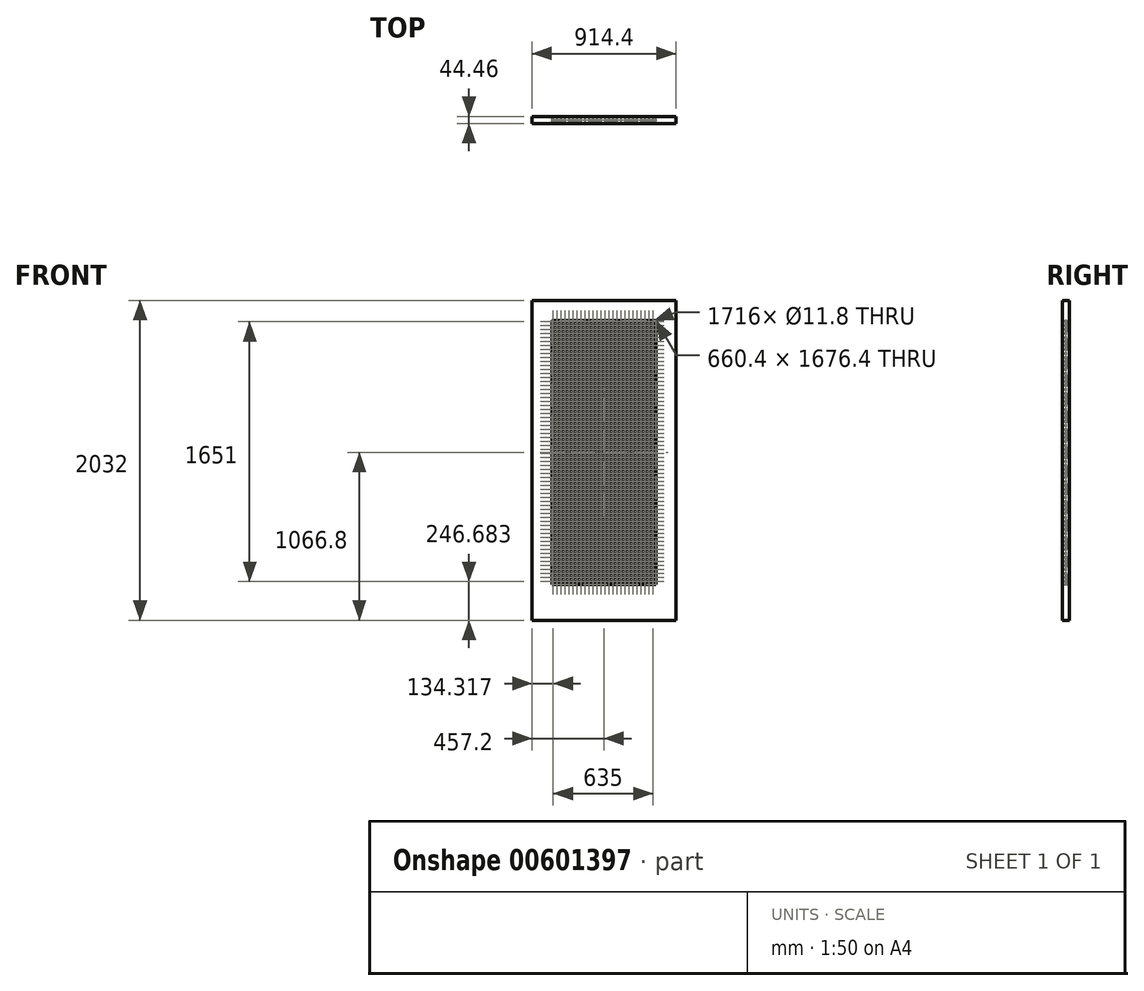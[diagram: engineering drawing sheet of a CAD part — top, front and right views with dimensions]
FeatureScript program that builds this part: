
annotation { "Feature Type Name" : "Feature", "Feature Type Description" : "" }
export const myFeature = defineFeature(function(context is Context, id is Id, definition is map)
    precondition{}
    {
        {
            var Q0;
            Q0=qCreatedBy(makeId("Front.planeOp"),FACE);
            var sketch = newSketch(context, id + "F0", { "sketchPlane" : qUnion([Q0])});
            skLineSegment(sketch, "E0.bottom", {"start": v(-457.2, 965.2) * mm, "end": v(457.2, 965.2) * mm});
            skLineSegment(sketch, "E0.top", {"start": v(-457.2, -1066.8) * mm, "end": v(457.2, -1066.8) * mm});
            skLineSegment(sketch, "E0.left", {"start": v(-457.2, 965.2) * mm, "end": v(-457.2, -1066.8) * mm});
            skLineSegment(sketch, "E0.right", {"start": v(457.2, 965.2) * mm, "end": v(457.2, -1066.8) * mm});
            skPoint(sketch, "E0.middle", {"position": v(0, 0) * mm});
            skLineSegment(sketch, "E1.bottom", {"start": v(-330.2, 838.2) * mm, "end": v(330.2, 838.2) * mm});
            skLineSegment(sketch, "E1.top", {"start": v(-330.2, -838.2) * mm, "end": v(330.2, -838.2) * mm});
            skLineSegment(sketch, "E1.left", {"start": v(-330.2, 838.2) * mm, "end": v(-330.2, -838.2) * mm});
            skLineSegment(sketch, "E1.right", {"start": v(330.2, 838.2) * mm, "end": v(330.2, -838.2) * mm});
            skSolve(sketch);
        }
        {
            var Q0;
            Q0=makeQuery(id+"F0.imprint","IMPRINT",FACE,{"disambiguationData":[TD([[makeQuery(id+"F0.imprint","IMPRINT",EDGE,{"derivedFrom":sQuery(id+"F0.wireOp",EDGE,"E1.bottom")}),-1.0]])]});
            extrude(context, id + "F1", {"entities" : qUnion([Q0]), "endBound" : BoundingType.SYMMETRIC, "oppositeDirection" : true, "depth" : 6.35 * mm, "offsetDistance" : 25.4 * mm});
        }
        {
            var Q0;
            Q0=makeQuery(id+"F1.opExtrude","CAP_FACE",FACE,{"disambiguationData":[OSD([sQuery(id+"F0.wireOp",EDGE,"E1.bottom"),sQuery(id+"F0.wireOp",EDGE,"E1.top"),sQuery(id+"F0.wireOp",EDGE,"E1.left"),sQuery(id+"F0.wireOp",EDGE,"E1.right")])],"isStart":true});
            var sketch = newSketch(context, id + "F2", { "sketchPlane" : qUnion([Q0])});
            skCircle(sketch, "E2.cCircle", {"center": v(-322.88, 830.88) * mm, "radius": 4.34 * mm, "construction": true});
            skLineSegment(sketch, "E2.0", {"start": v(-324.87, 836.02) * mm, "end": v(-319.43, 835.17) * mm});
            skLineSegment(sketch, "E2.1", {"start": v(-319.43, 835.17) * mm, "end": v(-317.44, 830.03) * mm});
            skLineSegment(sketch, "E2.2", {"start": v(-317.44, 830.03) * mm, "end": v(-320.9, 825.74) * mm});
            skLineSegment(sketch, "E2.3", {"start": v(-320.9, 825.74) * mm, "end": v(-326.34, 826.6) * mm});
            skLineSegment(sketch, "E2.4", {"start": v(-326.34, 826.6) * mm, "end": v(-328.33, 831.73) * mm});
            skLineSegment(sketch, "E2.5", {"start": v(-328.33, 831.73) * mm, "end": v(-324.87, 836.02) * mm});
            skPoint(sketch, "E2.0.midPoint", {"position": v(-322.15, 835.6) * mm});
            skCircle(sketch, "E3", {"center": v(-322.88, 830.88) * mm, "radius": 5.9 * mm});
            skCircle(sketch, "E4", {"center": v(-322.88, 830.88) * mm, "radius": 4.86 * mm});
            skCircle(sketch, "E5.0.1.0", {"center": v(-322.88, 805.48) * mm, "radius": 5.9 * mm});
            skCircle(sketch, "E5.0.2.0", {"center": v(-322.88, 780.08) * mm, "radius": 5.9 * mm});
            skCircle(sketch, "E5.0.3.0", {"center": v(-322.88, 754.68) * mm, "radius": 5.9 * mm});
            skCircle(sketch, "E5.0.4.0", {"center": v(-322.88, 729.28) * mm, "radius": 5.9 * mm});
            skCircle(sketch, "E5.0.5.0", {"center": v(-322.88, 703.88) * mm, "radius": 5.9 * mm});
            skCircle(sketch, "E5.0.6.0", {"center": v(-322.88, 678.48) * mm, "radius": 5.9 * mm});
            skCircle(sketch, "E5.0.7.0", {"center": v(-322.88, 653.08) * mm, "radius": 5.9 * mm});
            skCircle(sketch, "E5.0.8.0", {"center": v(-322.88, 627.68) * mm, "radius": 5.9 * mm});
            skCircle(sketch, "E5.0.9.0", {"center": v(-322.88, 602.28) * mm, "radius": 5.9 * mm});
            skCircle(sketch, "E5.0.10.0", {"center": v(-322.88, 576.88) * mm, "radius": 5.9 * mm});
            skCircle(sketch, "E5.0.11.0", {"center": v(-322.88, 551.48) * mm, "radius": 5.9 * mm});
            skCircle(sketch, "E5.0.12.0", {"center": v(-322.88, 526.08) * mm, "radius": 5.9 * mm});
            skCircle(sketch, "E5.0.13.0", {"center": v(-322.88, 500.68) * mm, "radius": 5.9 * mm});
            skCircle(sketch, "E5.0.14.0", {"center": v(-322.88, 475.28) * mm, "radius": 5.9 * mm});
            skCircle(sketch, "E5.0.15.0", {"center": v(-322.88, 449.88) * mm, "radius": 5.9 * mm});
            skCircle(sketch, "E5.0.16.0", {"center": v(-322.88, 424.48) * mm, "radius": 5.9 * mm});
            skCircle(sketch, "E5.0.17.0", {"center": v(-322.88, 399.08) * mm, "radius": 5.9 * mm});
            skCircle(sketch, "E5.0.18.0", {"center": v(-322.88, 373.68) * mm, "radius": 5.9 * mm});
            skCircle(sketch, "E5.0.19.0", {"center": v(-322.88, 348.28) * mm, "radius": 5.9 * mm});
            skCircle(sketch, "E5.0.20.0", {"center": v(-322.88, 322.88) * mm, "radius": 5.9 * mm});
            skCircle(sketch, "E5.0.21.0", {"center": v(-322.88, 297.48) * mm, "radius": 5.9 * mm});
            skCircle(sketch, "E5.0.22.0", {"center": v(-322.88, 272.08) * mm, "radius": 5.9 * mm});
            skCircle(sketch, "E5.0.23.0", {"center": v(-322.88, 246.68) * mm, "radius": 5.9 * mm});
            skCircle(sketch, "E5.0.24.0", {"center": v(-322.88, 221.28) * mm, "radius": 5.9 * mm});
            skCircle(sketch, "E5.1.0.0", {"center": v(-297.48, 830.88) * mm, "radius": 5.9 * mm});
            skCircle(sketch, "E5.1.1.0", {"center": v(-297.48, 805.48) * mm, "radius": 5.9 * mm});
            skCircle(sketch, "E5.1.2.0", {"center": v(-297.48, 780.08) * mm, "radius": 5.9 * mm});
            skCircle(sketch, "E5.1.3.0", {"center": v(-297.48, 754.68) * mm, "radius": 5.9 * mm});
            skCircle(sketch, "E5.1.4.0", {"center": v(-297.48, 729.28) * mm, "radius": 5.9 * mm});
            skCircle(sketch, "E5.1.5.0", {"center": v(-297.48, 703.88) * mm, "radius": 5.9 * mm});
            skCircle(sketch, "E5.1.6.0", {"center": v(-297.48, 678.48) * mm, "radius": 5.9 * mm});
            skCircle(sketch, "E5.1.7.0", {"center": v(-297.48, 653.08) * mm, "radius": 5.9 * mm});
            skCircle(sketch, "E5.1.8.0", {"center": v(-297.48, 627.68) * mm, "radius": 5.9 * mm});
            skCircle(sketch, "E5.1.9.0", {"center": v(-297.48, 602.28) * mm, "radius": 5.9 * mm});
            skCircle(sketch, "E5.1.10.0", {"center": v(-297.48, 576.88) * mm, "radius": 5.9 * mm});
            skCircle(sketch, "E5.1.11.0", {"center": v(-297.48, 551.48) * mm, "radius": 5.9 * mm});
            skCircle(sketch, "E5.1.12.0", {"center": v(-297.48, 526.08) * mm, "radius": 5.9 * mm});
            skCircle(sketch, "E5.1.13.0", {"center": v(-297.48, 500.68) * mm, "radius": 5.9 * mm});
            skCircle(sketch, "E5.1.14.0", {"center": v(-297.48, 475.28) * mm, "radius": 5.9 * mm});
            skCircle(sketch, "E5.1.15.0", {"center": v(-297.48, 449.88) * mm, "radius": 5.9 * mm});
            skCircle(sketch, "E5.1.16.0", {"center": v(-297.48, 424.48) * mm, "radius": 5.9 * mm});
            skCircle(sketch, "E5.1.17.0", {"center": v(-297.48, 399.08) * mm, "radius": 5.9 * mm});
            skCircle(sketch, "E5.1.18.0", {"center": v(-297.48, 373.68) * mm, "radius": 5.9 * mm});
            skCircle(sketch, "E5.1.19.0", {"center": v(-297.48, 348.28) * mm, "radius": 5.9 * mm});
            skCircle(sketch, "E5.1.20.0", {"center": v(-297.48, 322.88) * mm, "radius": 5.9 * mm});
            skCircle(sketch, "E5.1.21.0", {"center": v(-297.48, 297.48) * mm, "radius": 5.9 * mm});
            skCircle(sketch, "E5.1.22.0", {"center": v(-297.48, 272.08) * mm, "radius": 5.9 * mm});
            skCircle(sketch, "E5.1.23.0", {"center": v(-297.48, 246.68) * mm, "radius": 5.9 * mm});
            skCircle(sketch, "E5.1.24.0", {"center": v(-297.48, 221.28) * mm, "radius": 5.9 * mm});
            skCircle(sketch, "E5.2.0.0", {"center": v(-272.08, 830.88) * mm, "radius": 5.9 * mm});
            skCircle(sketch, "E5.2.1.0", {"center": v(-272.08, 805.48) * mm, "radius": 5.9 * mm});
            skCircle(sketch, "E5.2.2.0", {"center": v(-272.08, 780.08) * mm, "radius": 5.9 * mm});
            skCircle(sketch, "E5.2.3.0", {"center": v(-272.08, 754.68) * mm, "radius": 5.9 * mm});
            skCircle(sketch, "E5.2.4.0", {"center": v(-272.08, 729.28) * mm, "radius": 5.9 * mm});
            skCircle(sketch, "E5.2.5.0", {"center": v(-272.08, 703.88) * mm, "radius": 5.9 * mm});
            skCircle(sketch, "E5.2.6.0", {"center": v(-272.08, 678.48) * mm, "radius": 5.9 * mm});
            skCircle(sketch, "E5.2.7.0", {"center": v(-272.08, 653.08) * mm, "radius": 5.9 * mm});
            skCircle(sketch, "E5.2.8.0", {"center": v(-272.08, 627.68) * mm, "radius": 5.9 * mm});
            skCircle(sketch, "E5.2.9.0", {"center": v(-272.08, 602.28) * mm, "radius": 5.9 * mm});
            skCircle(sketch, "E5.2.10.0", {"center": v(-272.08, 576.88) * mm, "radius": 5.9 * mm});
            skCircle(sketch, "E5.2.11.0", {"center": v(-272.08, 551.48) * mm, "radius": 5.9 * mm});
            skCircle(sketch, "E5.2.12.0", {"center": v(-272.08, 526.08) * mm, "radius": 5.9 * mm});
            skCircle(sketch, "E5.2.13.0", {"center": v(-272.08, 500.68) * mm, "radius": 5.9 * mm});
            skCircle(sketch, "E5.2.14.0", {"center": v(-272.08, 475.28) * mm, "radius": 5.9 * mm});
            skCircle(sketch, "E5.2.15.0", {"center": v(-272.08, 449.88) * mm, "radius": 5.9 * mm});
            skCircle(sketch, "E5.2.16.0", {"center": v(-272.08, 424.48) * mm, "radius": 5.9 * mm});
            skCircle(sketch, "E5.2.17.0", {"center": v(-272.08, 399.08) * mm, "radius": 5.9 * mm});
            skCircle(sketch, "E5.2.18.0", {"center": v(-272.08, 373.68) * mm, "radius": 5.9 * mm});
            skCircle(sketch, "E5.2.19.0", {"center": v(-272.08, 348.28) * mm, "radius": 5.9 * mm});
            skCircle(sketch, "E5.2.20.0", {"center": v(-272.08, 322.88) * mm, "radius": 5.9 * mm});
            skCircle(sketch, "E5.2.21.0", {"center": v(-272.08, 297.48) * mm, "radius": 5.9 * mm});
            skCircle(sketch, "E5.2.22.0", {"center": v(-272.08, 272.08) * mm, "radius": 5.9 * mm});
            skCircle(sketch, "E5.2.23.0", {"center": v(-272.08, 246.68) * mm, "radius": 5.9 * mm});
            skCircle(sketch, "E5.2.24.0", {"center": v(-272.08, 221.28) * mm, "radius": 5.9 * mm});
            skCircle(sketch, "E5.3.0.0", {"center": v(-246.68, 830.88) * mm, "radius": 5.9 * mm});
            skCircle(sketch, "E5.3.1.0", {"center": v(-246.68, 805.48) * mm, "radius": 5.9 * mm});
            skCircle(sketch, "E5.3.2.0", {"center": v(-246.68, 780.08) * mm, "radius": 5.9 * mm});
            skCircle(sketch, "E5.3.3.0", {"center": v(-246.68, 754.68) * mm, "radius": 5.9 * mm});
            skCircle(sketch, "E5.3.4.0", {"center": v(-246.68, 729.28) * mm, "radius": 5.9 * mm});
            skCircle(sketch, "E5.3.5.0", {"center": v(-246.68, 703.88) * mm, "radius": 5.9 * mm});
            skCircle(sketch, "E5.3.6.0", {"center": v(-246.68, 678.48) * mm, "radius": 5.9 * mm});
            skCircle(sketch, "E5.3.7.0", {"center": v(-246.68, 653.08) * mm, "radius": 5.9 * mm});
            skCircle(sketch, "E5.3.8.0", {"center": v(-246.68, 627.68) * mm, "radius": 5.9 * mm});
            skCircle(sketch, "E5.3.9.0", {"center": v(-246.68, 602.28) * mm, "radius": 5.9 * mm});
            skCircle(sketch, "E5.3.10.0", {"center": v(-246.68, 576.88) * mm, "radius": 5.9 * mm});
            skCircle(sketch, "E5.3.11.0", {"center": v(-246.68, 551.48) * mm, "radius": 5.9 * mm});
            skCircle(sketch, "E5.3.12.0", {"center": v(-246.68, 526.08) * mm, "radius": 5.9 * mm});
            skCircle(sketch, "E5.3.13.0", {"center": v(-246.68, 500.68) * mm, "radius": 5.9 * mm});
            skCircle(sketch, "E5.3.14.0", {"center": v(-246.68, 475.28) * mm, "radius": 5.9 * mm});
            skCircle(sketch, "E5.3.15.0", {"center": v(-246.68, 449.88) * mm, "radius": 5.9 * mm});
            skCircle(sketch, "E5.3.16.0", {"center": v(-246.68, 424.48) * mm, "radius": 5.9 * mm});
            skCircle(sketch, "E5.3.17.0", {"center": v(-246.68, 399.08) * mm, "radius": 5.9 * mm});
            skCircle(sketch, "E5.3.18.0", {"center": v(-246.68, 373.68) * mm, "radius": 5.9 * mm});
            skCircle(sketch, "E5.3.19.0", {"center": v(-246.68, 348.28) * mm, "radius": 5.9 * mm});
            skCircle(sketch, "E5.3.20.0", {"center": v(-246.68, 322.88) * mm, "radius": 5.9 * mm});
            skCircle(sketch, "E5.3.21.0", {"center": v(-246.68, 297.48) * mm, "radius": 5.9 * mm});
            skCircle(sketch, "E5.3.22.0", {"center": v(-246.68, 272.08) * mm, "radius": 5.9 * mm});
            skCircle(sketch, "E5.3.23.0", {"center": v(-246.68, 246.68) * mm, "radius": 5.9 * mm});
            skCircle(sketch, "E5.3.24.0", {"center": v(-246.68, 221.28) * mm, "radius": 5.9 * mm});
            skCircle(sketch, "E5.4.0.0", {"center": v(-221.28, 830.88) * mm, "radius": 5.9 * mm});
            skCircle(sketch, "E5.4.1.0", {"center": v(-221.28, 805.48) * mm, "radius": 5.9 * mm});
            skCircle(sketch, "E5.4.2.0", {"center": v(-221.28, 780.08) * mm, "radius": 5.9 * mm});
            skCircle(sketch, "E5.4.3.0", {"center": v(-221.28, 754.68) * mm, "radius": 5.9 * mm});
            skCircle(sketch, "E5.4.4.0", {"center": v(-221.28, 729.28) * mm, "radius": 5.9 * mm});
            skCircle(sketch, "E5.4.5.0", {"center": v(-221.28, 703.88) * mm, "radius": 5.9 * mm});
            skCircle(sketch, "E5.4.6.0", {"center": v(-221.28, 678.48) * mm, "radius": 5.9 * mm});
            skCircle(sketch, "E5.4.7.0", {"center": v(-221.28, 653.08) * mm, "radius": 5.9 * mm});
            skCircle(sketch, "E5.4.8.0", {"center": v(-221.28, 627.68) * mm, "radius": 5.9 * mm});
            skCircle(sketch, "E5.4.9.0", {"center": v(-221.28, 602.28) * mm, "radius": 5.9 * mm});
            skCircle(sketch, "E5.4.10.0", {"center": v(-221.28, 576.88) * mm, "radius": 5.9 * mm});
            skCircle(sketch, "E5.4.11.0", {"center": v(-221.28, 551.48) * mm, "radius": 5.9 * mm});
            skCircle(sketch, "E5.4.12.0", {"center": v(-221.28, 526.08) * mm, "radius": 5.9 * mm});
            skCircle(sketch, "E5.4.13.0", {"center": v(-221.28, 500.68) * mm, "radius": 5.9 * mm});
            skCircle(sketch, "E5.4.14.0", {"center": v(-221.28, 475.28) * mm, "radius": 5.9 * mm});
            skCircle(sketch, "E5.4.15.0", {"center": v(-221.28, 449.88) * mm, "radius": 5.9 * mm});
            skCircle(sketch, "E5.4.16.0", {"center": v(-221.28, 424.48) * mm, "radius": 5.9 * mm});
            skCircle(sketch, "E5.4.17.0", {"center": v(-221.28, 399.08) * mm, "radius": 5.9 * mm});
            skCircle(sketch, "E5.4.18.0", {"center": v(-221.28, 373.68) * mm, "radius": 5.9 * mm});
            skCircle(sketch, "E5.4.19.0", {"center": v(-221.28, 348.28) * mm, "radius": 5.9 * mm});
            skCircle(sketch, "E5.4.20.0", {"center": v(-221.28, 322.88) * mm, "radius": 5.9 * mm});
            skCircle(sketch, "E5.4.21.0", {"center": v(-221.28, 297.48) * mm, "radius": 5.9 * mm});
            skCircle(sketch, "E5.4.22.0", {"center": v(-221.28, 272.08) * mm, "radius": 5.9 * mm});
            skCircle(sketch, "E5.4.23.0", {"center": v(-221.28, 246.68) * mm, "radius": 5.9 * mm});
            skCircle(sketch, "E5.4.24.0", {"center": v(-221.28, 221.28) * mm, "radius": 5.9 * mm});
            skCircle(sketch, "E5.5.0.0", {"center": v(-195.88, 830.88) * mm, "radius": 5.9 * mm});
            skCircle(sketch, "E5.5.1.0", {"center": v(-195.88, 805.48) * mm, "radius": 5.9 * mm});
            skCircle(sketch, "E5.5.2.0", {"center": v(-195.88, 780.08) * mm, "radius": 5.9 * mm});
            skCircle(sketch, "E5.5.3.0", {"center": v(-195.88, 754.68) * mm, "radius": 5.9 * mm});
            skCircle(sketch, "E5.5.4.0", {"center": v(-195.88, 729.28) * mm, "radius": 5.9 * mm});
            skCircle(sketch, "E5.5.5.0", {"center": v(-195.88, 703.88) * mm, "radius": 5.9 * mm});
            skCircle(sketch, "E5.5.6.0", {"center": v(-195.88, 678.48) * mm, "radius": 5.9 * mm});
            skCircle(sketch, "E5.5.7.0", {"center": v(-195.88, 653.08) * mm, "radius": 5.9 * mm});
            skCircle(sketch, "E5.5.8.0", {"center": v(-195.88, 627.68) * mm, "radius": 5.9 * mm});
            skCircle(sketch, "E5.5.9.0", {"center": v(-195.88, 602.28) * mm, "radius": 5.9 * mm});
            skCircle(sketch, "E5.5.10.0", {"center": v(-195.88, 576.88) * mm, "radius": 5.9 * mm});
            skCircle(sketch, "E5.5.11.0", {"center": v(-195.88, 551.48) * mm, "radius": 5.9 * mm});
            skCircle(sketch, "E5.5.12.0", {"center": v(-195.88, 526.08) * mm, "radius": 5.9 * mm});
            skCircle(sketch, "E5.5.13.0", {"center": v(-195.88, 500.68) * mm, "radius": 5.9 * mm});
            skCircle(sketch, "E5.5.14.0", {"center": v(-195.88, 475.28) * mm, "radius": 5.9 * mm});
            skCircle(sketch, "E5.5.15.0", {"center": v(-195.88, 449.88) * mm, "radius": 5.9 * mm});
            skCircle(sketch, "E5.5.16.0", {"center": v(-195.88, 424.48) * mm, "radius": 5.9 * mm});
            skCircle(sketch, "E5.5.17.0", {"center": v(-195.88, 399.08) * mm, "radius": 5.9 * mm});
            skCircle(sketch, "E5.5.18.0", {"center": v(-195.88, 373.68) * mm, "radius": 5.9 * mm});
            skCircle(sketch, "E5.5.19.0", {"center": v(-195.88, 348.28) * mm, "radius": 5.9 * mm});
            skCircle(sketch, "E5.5.20.0", {"center": v(-195.88, 322.88) * mm, "radius": 5.9 * mm});
            skCircle(sketch, "E5.5.21.0", {"center": v(-195.88, 297.48) * mm, "radius": 5.9 * mm});
            skCircle(sketch, "E5.5.22.0", {"center": v(-195.88, 272.08) * mm, "radius": 5.9 * mm});
            skCircle(sketch, "E5.5.23.0", {"center": v(-195.88, 246.68) * mm, "radius": 5.9 * mm});
            skCircle(sketch, "E5.5.24.0", {"center": v(-195.88, 221.28) * mm, "radius": 5.9 * mm});
            skCircle(sketch, "E5.6.0.0", {"center": v(-170.48, 830.88) * mm, "radius": 5.9 * mm});
            skCircle(sketch, "E5.6.1.0", {"center": v(-170.48, 805.48) * mm, "radius": 5.9 * mm});
            skCircle(sketch, "E5.6.2.0", {"center": v(-170.48, 780.08) * mm, "radius": 5.9 * mm});
            skCircle(sketch, "E5.6.3.0", {"center": v(-170.48, 754.68) * mm, "radius": 5.9 * mm});
            skCircle(sketch, "E5.6.4.0", {"center": v(-170.48, 729.28) * mm, "radius": 5.9 * mm});
            skCircle(sketch, "E5.6.5.0", {"center": v(-170.48, 703.88) * mm, "radius": 5.9 * mm});
            skCircle(sketch, "E5.6.6.0", {"center": v(-170.48, 678.48) * mm, "radius": 5.9 * mm});
            skCircle(sketch, "E5.6.7.0", {"center": v(-170.48, 653.08) * mm, "radius": 5.9 * mm});
            skCircle(sketch, "E5.6.8.0", {"center": v(-170.48, 627.68) * mm, "radius": 5.9 * mm});
            skCircle(sketch, "E5.6.9.0", {"center": v(-170.48, 602.28) * mm, "radius": 5.9 * mm});
            skCircle(sketch, "E5.6.10.0", {"center": v(-170.48, 576.88) * mm, "radius": 5.9 * mm});
            skCircle(sketch, "E5.6.11.0", {"center": v(-170.48, 551.48) * mm, "radius": 5.9 * mm});
            skCircle(sketch, "E5.6.12.0", {"center": v(-170.48, 526.08) * mm, "radius": 5.9 * mm});
            skCircle(sketch, "E5.6.13.0", {"center": v(-170.48, 500.68) * mm, "radius": 5.9 * mm});
            skCircle(sketch, "E5.6.14.0", {"center": v(-170.48, 475.28) * mm, "radius": 5.9 * mm});
            skCircle(sketch, "E5.6.15.0", {"center": v(-170.48, 449.88) * mm, "radius": 5.9 * mm});
            skCircle(sketch, "E5.6.16.0", {"center": v(-170.48, 424.48) * mm, "radius": 5.9 * mm});
            skCircle(sketch, "E5.6.17.0", {"center": v(-170.48, 399.08) * mm, "radius": 5.9 * mm});
            skCircle(sketch, "E5.6.18.0", {"center": v(-170.48, 373.68) * mm, "radius": 5.9 * mm});
            skCircle(sketch, "E5.6.19.0", {"center": v(-170.48, 348.28) * mm, "radius": 5.9 * mm});
            skCircle(sketch, "E5.6.20.0", {"center": v(-170.48, 322.88) * mm, "radius": 5.9 * mm});
            skCircle(sketch, "E5.6.21.0", {"center": v(-170.48, 297.48) * mm, "radius": 5.9 * mm});
            skCircle(sketch, "E5.6.22.0", {"center": v(-170.48, 272.08) * mm, "radius": 5.9 * mm});
            skCircle(sketch, "E5.6.23.0", {"center": v(-170.48, 246.68) * mm, "radius": 5.9 * mm});
            skCircle(sketch, "E5.6.24.0", {"center": v(-170.48, 221.28) * mm, "radius": 5.9 * mm});
            skCircle(sketch, "E5.7.0.0", {"center": v(-145.08, 830.88) * mm, "radius": 5.9 * mm});
            skCircle(sketch, "E5.7.1.0", {"center": v(-145.08, 805.48) * mm, "radius": 5.9 * mm});
            skCircle(sketch, "E5.7.2.0", {"center": v(-145.08, 780.08) * mm, "radius": 5.9 * mm});
            skCircle(sketch, "E5.7.3.0", {"center": v(-145.08, 754.68) * mm, "radius": 5.9 * mm});
            skCircle(sketch, "E5.7.4.0", {"center": v(-145.08, 729.28) * mm, "radius": 5.9 * mm});
            skCircle(sketch, "E5.7.5.0", {"center": v(-145.08, 703.88) * mm, "radius": 5.9 * mm});
            skCircle(sketch, "E5.7.6.0", {"center": v(-145.08, 678.48) * mm, "radius": 5.9 * mm});
            skCircle(sketch, "E5.7.7.0", {"center": v(-145.08, 653.08) * mm, "radius": 5.9 * mm});
            skCircle(sketch, "E5.7.8.0", {"center": v(-145.08, 627.68) * mm, "radius": 5.9 * mm});
            skCircle(sketch, "E5.7.9.0", {"center": v(-145.08, 602.28) * mm, "radius": 5.9 * mm});
            skCircle(sketch, "E5.7.10.0", {"center": v(-145.08, 576.88) * mm, "radius": 5.9 * mm});
            skCircle(sketch, "E5.7.11.0", {"center": v(-145.08, 551.48) * mm, "radius": 5.9 * mm});
            skCircle(sketch, "E5.7.12.0", {"center": v(-145.08, 526.08) * mm, "radius": 5.9 * mm});
            skCircle(sketch, "E5.7.13.0", {"center": v(-145.08, 500.68) * mm, "radius": 5.9 * mm});
            skCircle(sketch, "E5.7.14.0", {"center": v(-145.08, 475.28) * mm, "radius": 5.9 * mm});
            skCircle(sketch, "E5.7.15.0", {"center": v(-145.08, 449.88) * mm, "radius": 5.9 * mm});
            skCircle(sketch, "E5.7.16.0", {"center": v(-145.08, 424.48) * mm, "radius": 5.9 * mm});
            skCircle(sketch, "E5.7.17.0", {"center": v(-145.08, 399.08) * mm, "radius": 5.9 * mm});
            skCircle(sketch, "E5.7.18.0", {"center": v(-145.08, 373.68) * mm, "radius": 5.9 * mm});
            skCircle(sketch, "E5.7.19.0", {"center": v(-145.08, 348.28) * mm, "radius": 5.9 * mm});
            skCircle(sketch, "E5.7.20.0", {"center": v(-145.08, 322.88) * mm, "radius": 5.9 * mm});
            skCircle(sketch, "E5.7.21.0", {"center": v(-145.08, 297.48) * mm, "radius": 5.9 * mm});
            skCircle(sketch, "E5.7.22.0", {"center": v(-145.08, 272.08) * mm, "radius": 5.9 * mm});
            skCircle(sketch, "E5.7.23.0", {"center": v(-145.08, 246.68) * mm, "radius": 5.9 * mm});
            skCircle(sketch, "E5.7.24.0", {"center": v(-145.08, 221.28) * mm, "radius": 5.9 * mm});
            skCircle(sketch, "E5.8.0.0", {"center": v(-119.68, 830.88) * mm, "radius": 5.9 * mm});
            skCircle(sketch, "E5.8.1.0", {"center": v(-119.68, 805.48) * mm, "radius": 5.9 * mm});
            skCircle(sketch, "E5.8.2.0", {"center": v(-119.68, 780.08) * mm, "radius": 5.9 * mm});
            skCircle(sketch, "E5.8.3.0", {"center": v(-119.68, 754.68) * mm, "radius": 5.9 * mm});
            skCircle(sketch, "E5.8.4.0", {"center": v(-119.68, 729.28) * mm, "radius": 5.9 * mm});
            skCircle(sketch, "E5.8.5.0", {"center": v(-119.68, 703.88) * mm, "radius": 5.9 * mm});
            skCircle(sketch, "E5.8.6.0", {"center": v(-119.68, 678.48) * mm, "radius": 5.9 * mm});
            skCircle(sketch, "E5.8.7.0", {"center": v(-119.68, 653.08) * mm, "radius": 5.9 * mm});
            skCircle(sketch, "E5.8.8.0", {"center": v(-119.68, 627.68) * mm, "radius": 5.9 * mm});
            skCircle(sketch, "E5.8.9.0", {"center": v(-119.68, 602.28) * mm, "radius": 5.9 * mm});
            skCircle(sketch, "E5.8.10.0", {"center": v(-119.68, 576.88) * mm, "radius": 5.9 * mm});
            skCircle(sketch, "E5.8.11.0", {"center": v(-119.68, 551.48) * mm, "radius": 5.9 * mm});
            skCircle(sketch, "E5.8.12.0", {"center": v(-119.68, 526.08) * mm, "radius": 5.9 * mm});
            skCircle(sketch, "E5.8.13.0", {"center": v(-119.68, 500.68) * mm, "radius": 5.9 * mm});
            skCircle(sketch, "E5.8.14.0", {"center": v(-119.68, 475.28) * mm, "radius": 5.9 * mm});
            skCircle(sketch, "E5.8.15.0", {"center": v(-119.68, 449.88) * mm, "radius": 5.9 * mm});
            skCircle(sketch, "E5.8.16.0", {"center": v(-119.68, 424.48) * mm, "radius": 5.9 * mm});
            skCircle(sketch, "E5.8.17.0", {"center": v(-119.68, 399.08) * mm, "radius": 5.9 * mm});
            skCircle(sketch, "E5.8.18.0", {"center": v(-119.68, 373.68) * mm, "radius": 5.9 * mm});
            skCircle(sketch, "E5.8.19.0", {"center": v(-119.68, 348.28) * mm, "radius": 5.9 * mm});
            skCircle(sketch, "E5.8.20.0", {"center": v(-119.68, 322.88) * mm, "radius": 5.9 * mm});
            skCircle(sketch, "E5.8.21.0", {"center": v(-119.68, 297.48) * mm, "radius": 5.9 * mm});
            skCircle(sketch, "E5.8.22.0", {"center": v(-119.68, 272.08) * mm, "radius": 5.9 * mm});
            skCircle(sketch, "E5.8.23.0", {"center": v(-119.68, 246.68) * mm, "radius": 5.9 * mm});
            skCircle(sketch, "E5.8.24.0", {"center": v(-119.68, 221.28) * mm, "radius": 5.9 * mm});
            skCircle(sketch, "E5.9.0.0", {"center": v(-94.28, 830.88) * mm, "radius": 5.9 * mm});
            skCircle(sketch, "E5.9.1.0", {"center": v(-94.28, 805.48) * mm, "radius": 5.9 * mm});
            skCircle(sketch, "E5.9.2.0", {"center": v(-94.28, 780.08) * mm, "radius": 5.9 * mm});
            skCircle(sketch, "E5.9.3.0", {"center": v(-94.28, 754.68) * mm, "radius": 5.9 * mm});
            skCircle(sketch, "E5.9.4.0", {"center": v(-94.28, 729.28) * mm, "radius": 5.9 * mm});
            skCircle(sketch, "E5.9.5.0", {"center": v(-94.28, 703.88) * mm, "radius": 5.9 * mm});
            skCircle(sketch, "E5.9.6.0", {"center": v(-94.28, 678.48) * mm, "radius": 5.9 * mm});
            skCircle(sketch, "E5.9.7.0", {"center": v(-94.28, 653.08) * mm, "radius": 5.9 * mm});
            skCircle(sketch, "E5.9.8.0", {"center": v(-94.28, 627.68) * mm, "radius": 5.9 * mm});
            skCircle(sketch, "E5.9.9.0", {"center": v(-94.28, 602.28) * mm, "radius": 5.9 * mm});
            skCircle(sketch, "E5.9.10.0", {"center": v(-94.28, 576.88) * mm, "radius": 5.9 * mm});
            skCircle(sketch, "E5.9.11.0", {"center": v(-94.28, 551.48) * mm, "radius": 5.9 * mm});
            skCircle(sketch, "E5.9.12.0", {"center": v(-94.28, 526.08) * mm, "radius": 5.9 * mm});
            skCircle(sketch, "E5.9.13.0", {"center": v(-94.28, 500.68) * mm, "radius": 5.9 * mm});
            skCircle(sketch, "E5.9.14.0", {"center": v(-94.28, 475.28) * mm, "radius": 5.9 * mm});
            skCircle(sketch, "E5.9.15.0", {"center": v(-94.28, 449.88) * mm, "radius": 5.9 * mm});
            skCircle(sketch, "E5.9.16.0", {"center": v(-94.28, 424.48) * mm, "radius": 5.9 * mm});
            skCircle(sketch, "E5.9.17.0", {"center": v(-94.28, 399.08) * mm, "radius": 5.9 * mm});
            skCircle(sketch, "E5.9.18.0", {"center": v(-94.28, 373.68) * mm, "radius": 5.9 * mm});
            skCircle(sketch, "E5.9.19.0", {"center": v(-94.28, 348.28) * mm, "radius": 5.9 * mm});
            skCircle(sketch, "E5.9.20.0", {"center": v(-94.28, 322.88) * mm, "radius": 5.9 * mm});
            skCircle(sketch, "E5.9.21.0", {"center": v(-94.28, 297.48) * mm, "radius": 5.9 * mm});
            skCircle(sketch, "E5.9.22.0", {"center": v(-94.28, 272.08) * mm, "radius": 5.9 * mm});
            skCircle(sketch, "E5.9.23.0", {"center": v(-94.28, 246.68) * mm, "radius": 5.9 * mm});
            skCircle(sketch, "E5.9.24.0", {"center": v(-94.28, 221.28) * mm, "radius": 5.9 * mm});
            skCircle(sketch, "E5.10.0.0", {"center": v(-68.88, 830.88) * mm, "radius": 5.9 * mm});
            skCircle(sketch, "E5.10.1.0", {"center": v(-68.88, 805.48) * mm, "radius": 5.9 * mm});
            skCircle(sketch, "E5.10.2.0", {"center": v(-68.88, 780.08) * mm, "radius": 5.9 * mm});
            skCircle(sketch, "E5.10.3.0", {"center": v(-68.88, 754.68) * mm, "radius": 5.9 * mm});
            skCircle(sketch, "E5.10.4.0", {"center": v(-68.88, 729.28) * mm, "radius": 5.9 * mm});
            skCircle(sketch, "E5.10.5.0", {"center": v(-68.88, 703.88) * mm, "radius": 5.9 * mm});
            skCircle(sketch, "E5.10.6.0", {"center": v(-68.88, 678.48) * mm, "radius": 5.9 * mm});
            skCircle(sketch, "E5.10.7.0", {"center": v(-68.88, 653.08) * mm, "radius": 5.9 * mm});
            skCircle(sketch, "E5.10.8.0", {"center": v(-68.88, 627.68) * mm, "radius": 5.9 * mm});
            skCircle(sketch, "E5.10.9.0", {"center": v(-68.88, 602.28) * mm, "radius": 5.9 * mm});
            skCircle(sketch, "E5.10.10.0", {"center": v(-68.88, 576.88) * mm, "radius": 5.9 * mm});
            skCircle(sketch, "E5.10.11.0", {"center": v(-68.88, 551.48) * mm, "radius": 5.9 * mm});
            skCircle(sketch, "E5.10.12.0", {"center": v(-68.88, 526.08) * mm, "radius": 5.9 * mm});
            skCircle(sketch, "E5.10.13.0", {"center": v(-68.88, 500.68) * mm, "radius": 5.9 * mm});
            skCircle(sketch, "E5.10.14.0", {"center": v(-68.88, 475.28) * mm, "radius": 5.9 * mm});
            skCircle(sketch, "E5.10.15.0", {"center": v(-68.88, 449.88) * mm, "radius": 5.9 * mm});
            skCircle(sketch, "E5.10.16.0", {"center": v(-68.88, 424.48) * mm, "radius": 5.9 * mm});
            skCircle(sketch, "E5.10.17.0", {"center": v(-68.88, 399.08) * mm, "radius": 5.9 * mm});
            skCircle(sketch, "E5.10.18.0", {"center": v(-68.88, 373.68) * mm, "radius": 5.9 * mm});
            skCircle(sketch, "E5.10.19.0", {"center": v(-68.88, 348.28) * mm, "radius": 5.9 * mm});
            skCircle(sketch, "E5.10.20.0", {"center": v(-68.88, 322.88) * mm, "radius": 5.9 * mm});
            skCircle(sketch, "E5.10.21.0", {"center": v(-68.88, 297.48) * mm, "radius": 5.9 * mm});
            skCircle(sketch, "E5.10.22.0", {"center": v(-68.88, 272.08) * mm, "radius": 5.9 * mm});
            skCircle(sketch, "E5.10.23.0", {"center": v(-68.88, 246.68) * mm, "radius": 5.9 * mm});
            skCircle(sketch, "E5.10.24.0", {"center": v(-68.88, 221.28) * mm, "radius": 5.9 * mm});
            skCircle(sketch, "E5.11.0.0", {"center": v(-43.48, 830.88) * mm, "radius": 5.9 * mm});
            skCircle(sketch, "E5.11.1.0", {"center": v(-43.48, 805.48) * mm, "radius": 5.9 * mm});
            skCircle(sketch, "E5.11.2.0", {"center": v(-43.48, 780.08) * mm, "radius": 5.9 * mm});
            skCircle(sketch, "E5.11.3.0", {"center": v(-43.48, 754.68) * mm, "radius": 5.9 * mm});
            skCircle(sketch, "E5.11.4.0", {"center": v(-43.48, 729.28) * mm, "radius": 5.9 * mm});
            skCircle(sketch, "E5.11.5.0", {"center": v(-43.48, 703.88) * mm, "radius": 5.9 * mm});
            skCircle(sketch, "E5.11.6.0", {"center": v(-43.48, 678.48) * mm, "radius": 5.9 * mm});
            skCircle(sketch, "E5.11.7.0", {"center": v(-43.48, 653.08) * mm, "radius": 5.9 * mm});
            skCircle(sketch, "E5.11.8.0", {"center": v(-43.48, 627.68) * mm, "radius": 5.9 * mm});
            skCircle(sketch, "E5.11.9.0", {"center": v(-43.48, 602.28) * mm, "radius": 5.9 * mm});
            skCircle(sketch, "E5.11.10.0", {"center": v(-43.48, 576.88) * mm, "radius": 5.9 * mm});
            skCircle(sketch, "E5.11.11.0", {"center": v(-43.48, 551.48) * mm, "radius": 5.9 * mm});
            skCircle(sketch, "E5.11.12.0", {"center": v(-43.48, 526.08) * mm, "radius": 5.9 * mm});
            skCircle(sketch, "E5.11.13.0", {"center": v(-43.48, 500.68) * mm, "radius": 5.9 * mm});
            skCircle(sketch, "E5.11.14.0", {"center": v(-43.48, 475.28) * mm, "radius": 5.9 * mm});
            skCircle(sketch, "E5.11.15.0", {"center": v(-43.48, 449.88) * mm, "radius": 5.9 * mm});
            skCircle(sketch, "E5.11.16.0", {"center": v(-43.48, 424.48) * mm, "radius": 5.9 * mm});
            skCircle(sketch, "E5.11.17.0", {"center": v(-43.48, 399.08) * mm, "radius": 5.9 * mm});
            skCircle(sketch, "E5.11.18.0", {"center": v(-43.48, 373.68) * mm, "radius": 5.9 * mm});
            skCircle(sketch, "E5.11.19.0", {"center": v(-43.48, 348.28) * mm, "radius": 5.9 * mm});
            skCircle(sketch, "E5.11.20.0", {"center": v(-43.48, 322.88) * mm, "radius": 5.9 * mm});
            skCircle(sketch, "E5.11.21.0", {"center": v(-43.48, 297.48) * mm, "radius": 5.9 * mm});
            skCircle(sketch, "E5.11.22.0", {"center": v(-43.48, 272.08) * mm, "radius": 5.9 * mm});
            skCircle(sketch, "E5.11.23.0", {"center": v(-43.48, 246.68) * mm, "radius": 5.9 * mm});
            skCircle(sketch, "E5.11.24.0", {"center": v(-43.48, 221.28) * mm, "radius": 5.9 * mm});
            skCircle(sketch, "E5.12.0.0", {"center": v(-18.08, 830.88) * mm, "radius": 5.9 * mm});
            skCircle(sketch, "E5.12.1.0", {"center": v(-18.08, 805.48) * mm, "radius": 5.9 * mm});
            skCircle(sketch, "E5.12.2.0", {"center": v(-18.08, 780.08) * mm, "radius": 5.9 * mm});
            skCircle(sketch, "E5.12.3.0", {"center": v(-18.08, 754.68) * mm, "radius": 5.9 * mm});
            skCircle(sketch, "E5.12.4.0", {"center": v(-18.08, 729.28) * mm, "radius": 5.9 * mm});
            skCircle(sketch, "E5.12.5.0", {"center": v(-18.08, 703.88) * mm, "radius": 5.9 * mm});
            skCircle(sketch, "E5.12.6.0", {"center": v(-18.08, 678.48) * mm, "radius": 5.9 * mm});
            skCircle(sketch, "E5.12.7.0", {"center": v(-18.08, 653.08) * mm, "radius": 5.9 * mm});
            skCircle(sketch, "E5.12.8.0", {"center": v(-18.08, 627.68) * mm, "radius": 5.9 * mm});
            skCircle(sketch, "E5.12.9.0", {"center": v(-18.08, 602.28) * mm, "radius": 5.9 * mm});
            skCircle(sketch, "E5.12.10.0", {"center": v(-18.08, 576.88) * mm, "radius": 5.9 * mm});
            skCircle(sketch, "E5.12.11.0", {"center": v(-18.08, 551.48) * mm, "radius": 5.9 * mm});
            skCircle(sketch, "E5.12.12.0", {"center": v(-18.08, 526.08) * mm, "radius": 5.9 * mm});
            skCircle(sketch, "E5.12.13.0", {"center": v(-18.08, 500.68) * mm, "radius": 5.9 * mm});
            skCircle(sketch, "E5.12.14.0", {"center": v(-18.08, 475.28) * mm, "radius": 5.9 * mm});
            skCircle(sketch, "E5.12.15.0", {"center": v(-18.08, 449.88) * mm, "radius": 5.9 * mm});
            skCircle(sketch, "E5.12.16.0", {"center": v(-18.08, 424.48) * mm, "radius": 5.9 * mm});
            skCircle(sketch, "E5.12.17.0", {"center": v(-18.08, 399.08) * mm, "radius": 5.9 * mm});
            skCircle(sketch, "E5.12.18.0", {"center": v(-18.08, 373.68) * mm, "radius": 5.9 * mm});
            skCircle(sketch, "E5.12.19.0", {"center": v(-18.08, 348.28) * mm, "radius": 5.9 * mm});
            skCircle(sketch, "E5.12.20.0", {"center": v(-18.08, 322.88) * mm, "radius": 5.9 * mm});
            skCircle(sketch, "E5.12.21.0", {"center": v(-18.08, 297.48) * mm, "radius": 5.9 * mm});
            skCircle(sketch, "E5.12.22.0", {"center": v(-18.08, 272.08) * mm, "radius": 5.9 * mm});
            skCircle(sketch, "E5.12.23.0", {"center": v(-18.08, 246.68) * mm, "radius": 5.9 * mm});
            skCircle(sketch, "E5.12.24.0", {"center": v(-18.08, 221.28) * mm, "radius": 5.9 * mm});
            skCircle(sketch, "E5.13.0.0", {"center": v(7.32, 830.88) * mm, "radius": 5.9 * mm});
            skCircle(sketch, "E5.13.1.0", {"center": v(7.32, 805.48) * mm, "radius": 5.9 * mm});
            skCircle(sketch, "E5.13.2.0", {"center": v(7.32, 780.08) * mm, "radius": 5.9 * mm});
            skCircle(sketch, "E5.13.3.0", {"center": v(7.32, 754.68) * mm, "radius": 5.9 * mm});
            skCircle(sketch, "E5.13.4.0", {"center": v(7.32, 729.28) * mm, "radius": 5.9 * mm});
            skCircle(sketch, "E5.13.5.0", {"center": v(7.32, 703.88) * mm, "radius": 5.9 * mm});
            skCircle(sketch, "E5.13.6.0", {"center": v(7.32, 678.48) * mm, "radius": 5.9 * mm});
            skCircle(sketch, "E5.13.7.0", {"center": v(7.32, 653.08) * mm, "radius": 5.9 * mm});
            skCircle(sketch, "E5.13.8.0", {"center": v(7.32, 627.68) * mm, "radius": 5.9 * mm});
            skCircle(sketch, "E5.13.9.0", {"center": v(7.32, 602.28) * mm, "radius": 5.9 * mm});
            skCircle(sketch, "E5.13.10.0", {"center": v(7.32, 576.88) * mm, "radius": 5.9 * mm});
            skCircle(sketch, "E5.13.11.0", {"center": v(7.32, 551.48) * mm, "radius": 5.9 * mm});
            skCircle(sketch, "E5.13.12.0", {"center": v(7.32, 526.08) * mm, "radius": 5.9 * mm});
            skCircle(sketch, "E5.13.13.0", {"center": v(7.32, 500.68) * mm, "radius": 5.9 * mm});
            skCircle(sketch, "E5.13.14.0", {"center": v(7.32, 475.28) * mm, "radius": 5.9 * mm});
            skCircle(sketch, "E5.13.15.0", {"center": v(7.32, 449.88) * mm, "radius": 5.9 * mm});
            skCircle(sketch, "E5.13.16.0", {"center": v(7.32, 424.48) * mm, "radius": 5.9 * mm});
            skCircle(sketch, "E5.13.17.0", {"center": v(7.32, 399.08) * mm, "radius": 5.9 * mm});
            skCircle(sketch, "E5.13.18.0", {"center": v(7.32, 373.68) * mm, "radius": 5.9 * mm});
            skCircle(sketch, "E5.13.19.0", {"center": v(7.32, 348.28) * mm, "radius": 5.9 * mm});
            skCircle(sketch, "E5.13.20.0", {"center": v(7.32, 322.88) * mm, "radius": 5.9 * mm});
            skCircle(sketch, "E5.13.21.0", {"center": v(7.32, 297.48) * mm, "radius": 5.9 * mm});
            skCircle(sketch, "E5.13.22.0", {"center": v(7.32, 272.08) * mm, "radius": 5.9 * mm});
            skCircle(sketch, "E5.13.23.0", {"center": v(7.32, 246.68) * mm, "radius": 5.9 * mm});
            skCircle(sketch, "E5.13.24.0", {"center": v(7.32, 221.28) * mm, "radius": 5.9 * mm});
            skCircle(sketch, "E5.14.0.0", {"center": v(32.72, 830.88) * mm, "radius": 5.9 * mm});
            skCircle(sketch, "E5.14.1.0", {"center": v(32.72, 805.48) * mm, "radius": 5.9 * mm});
            skCircle(sketch, "E5.14.2.0", {"center": v(32.72, 780.08) * mm, "radius": 5.9 * mm});
            skCircle(sketch, "E5.14.3.0", {"center": v(32.72, 754.68) * mm, "radius": 5.9 * mm});
            skCircle(sketch, "E5.14.4.0", {"center": v(32.72, 729.28) * mm, "radius": 5.9 * mm});
            skCircle(sketch, "E5.14.5.0", {"center": v(32.72, 703.88) * mm, "radius": 5.9 * mm});
            skCircle(sketch, "E5.14.6.0", {"center": v(32.72, 678.48) * mm, "radius": 5.9 * mm});
            skCircle(sketch, "E5.14.7.0", {"center": v(32.72, 653.08) * mm, "radius": 5.9 * mm});
            skCircle(sketch, "E5.14.8.0", {"center": v(32.72, 627.68) * mm, "radius": 5.9 * mm});
            skCircle(sketch, "E5.14.9.0", {"center": v(32.72, 602.28) * mm, "radius": 5.9 * mm});
            skCircle(sketch, "E5.14.10.0", {"center": v(32.72, 576.88) * mm, "radius": 5.9 * mm});
            skCircle(sketch, "E5.14.11.0", {"center": v(32.72, 551.48) * mm, "radius": 5.9 * mm});
            skCircle(sketch, "E5.14.12.0", {"center": v(32.72, 526.08) * mm, "radius": 5.9 * mm});
            skCircle(sketch, "E5.14.13.0", {"center": v(32.72, 500.68) * mm, "radius": 5.9 * mm});
            skCircle(sketch, "E5.14.14.0", {"center": v(32.72, 475.28) * mm, "radius": 5.9 * mm});
            skCircle(sketch, "E5.14.15.0", {"center": v(32.72, 449.88) * mm, "radius": 5.9 * mm});
            skCircle(sketch, "E5.14.16.0", {"center": v(32.72, 424.48) * mm, "radius": 5.9 * mm});
            skCircle(sketch, "E5.14.17.0", {"center": v(32.72, 399.08) * mm, "radius": 5.9 * mm});
            skCircle(sketch, "E5.14.18.0", {"center": v(32.72, 373.68) * mm, "radius": 5.9 * mm});
            skCircle(sketch, "E5.14.19.0", {"center": v(32.72, 348.28) * mm, "radius": 5.9 * mm});
            skCircle(sketch, "E5.14.20.0", {"center": v(32.72, 322.88) * mm, "radius": 5.9 * mm});
            skCircle(sketch, "E5.14.21.0", {"center": v(32.72, 297.48) * mm, "radius": 5.9 * mm});
            skCircle(sketch, "E5.14.22.0", {"center": v(32.72, 272.08) * mm, "radius": 5.9 * mm});
            skCircle(sketch, "E5.14.23.0", {"center": v(32.72, 246.68) * mm, "radius": 5.9 * mm});
            skCircle(sketch, "E5.14.24.0", {"center": v(32.72, 221.28) * mm, "radius": 5.9 * mm});
            skCircle(sketch, "E5.15.0.0", {"center": v(58.12, 830.88) * mm, "radius": 5.9 * mm});
            skCircle(sketch, "E5.15.1.0", {"center": v(58.12, 805.48) * mm, "radius": 5.9 * mm});
            skCircle(sketch, "E5.15.2.0", {"center": v(58.12, 780.08) * mm, "radius": 5.9 * mm});
            skCircle(sketch, "E5.15.3.0", {"center": v(58.12, 754.68) * mm, "radius": 5.9 * mm});
            skCircle(sketch, "E5.15.4.0", {"center": v(58.12, 729.28) * mm, "radius": 5.9 * mm});
            skCircle(sketch, "E5.15.5.0", {"center": v(58.12, 703.88) * mm, "radius": 5.9 * mm});
            skCircle(sketch, "E5.15.6.0", {"center": v(58.12, 678.48) * mm, "radius": 5.9 * mm});
            skCircle(sketch, "E5.15.7.0", {"center": v(58.12, 653.08) * mm, "radius": 5.9 * mm});
            skCircle(sketch, "E5.15.8.0", {"center": v(58.12, 627.68) * mm, "radius": 5.9 * mm});
            skCircle(sketch, "E5.15.9.0", {"center": v(58.12, 602.28) * mm, "radius": 5.9 * mm});
            skCircle(sketch, "E5.15.10.0", {"center": v(58.12, 576.88) * mm, "radius": 5.9 * mm});
            skCircle(sketch, "E5.15.11.0", {"center": v(58.12, 551.48) * mm, "radius": 5.9 * mm});
            skCircle(sketch, "E5.15.12.0", {"center": v(58.12, 526.08) * mm, "radius": 5.9 * mm});
            skCircle(sketch, "E5.15.13.0", {"center": v(58.12, 500.68) * mm, "radius": 5.9 * mm});
            skCircle(sketch, "E5.15.14.0", {"center": v(58.12, 475.28) * mm, "radius": 5.9 * mm});
            skCircle(sketch, "E5.15.15.0", {"center": v(58.12, 449.88) * mm, "radius": 5.9 * mm});
            skCircle(sketch, "E5.15.16.0", {"center": v(58.12, 424.48) * mm, "radius": 5.9 * mm});
            skCircle(sketch, "E5.15.17.0", {"center": v(58.12, 399.08) * mm, "radius": 5.9 * mm});
            skCircle(sketch, "E5.15.18.0", {"center": v(58.12, 373.68) * mm, "radius": 5.9 * mm});
            skCircle(sketch, "E5.15.19.0", {"center": v(58.12, 348.28) * mm, "radius": 5.9 * mm});
            skCircle(sketch, "E5.15.20.0", {"center": v(58.12, 322.88) * mm, "radius": 5.9 * mm});
            skCircle(sketch, "E5.15.21.0", {"center": v(58.12, 297.48) * mm, "radius": 5.9 * mm});
            skCircle(sketch, "E5.15.22.0", {"center": v(58.12, 272.08) * mm, "radius": 5.9 * mm});
            skCircle(sketch, "E5.15.23.0", {"center": v(58.12, 246.68) * mm, "radius": 5.9 * mm});
            skCircle(sketch, "E5.15.24.0", {"center": v(58.12, 221.28) * mm, "radius": 5.9 * mm});
            skCircle(sketch, "E5.16.0.0", {"center": v(83.52, 830.88) * mm, "radius": 5.9 * mm});
            skCircle(sketch, "E5.16.1.0", {"center": v(83.52, 805.48) * mm, "radius": 5.9 * mm});
            skCircle(sketch, "E5.16.2.0", {"center": v(83.52, 780.08) * mm, "radius": 5.9 * mm});
            skCircle(sketch, "E5.16.3.0", {"center": v(83.52, 754.68) * mm, "radius": 5.9 * mm});
            skCircle(sketch, "E5.16.4.0", {"center": v(83.52, 729.28) * mm, "radius": 5.9 * mm});
            skCircle(sketch, "E5.16.5.0", {"center": v(83.52, 703.88) * mm, "radius": 5.9 * mm});
            skCircle(sketch, "E5.16.6.0", {"center": v(83.52, 678.48) * mm, "radius": 5.9 * mm});
            skCircle(sketch, "E5.16.7.0", {"center": v(83.52, 653.08) * mm, "radius": 5.9 * mm});
            skCircle(sketch, "E5.16.8.0", {"center": v(83.52, 627.68) * mm, "radius": 5.9 * mm});
            skCircle(sketch, "E5.16.9.0", {"center": v(83.52, 602.28) * mm, "radius": 5.9 * mm});
            skCircle(sketch, "E5.16.10.0", {"center": v(83.52, 576.88) * mm, "radius": 5.9 * mm});
            skCircle(sketch, "E5.16.11.0", {"center": v(83.52, 551.48) * mm, "radius": 5.9 * mm});
            skCircle(sketch, "E5.16.12.0", {"center": v(83.52, 526.08) * mm, "radius": 5.9 * mm});
            skCircle(sketch, "E5.16.13.0", {"center": v(83.52, 500.68) * mm, "radius": 5.9 * mm});
            skCircle(sketch, "E5.16.14.0", {"center": v(83.52, 475.28) * mm, "radius": 5.9 * mm});
            skCircle(sketch, "E5.16.15.0", {"center": v(83.52, 449.88) * mm, "radius": 5.9 * mm});
            skCircle(sketch, "E5.16.16.0", {"center": v(83.52, 424.48) * mm, "radius": 5.9 * mm});
            skCircle(sketch, "E5.16.17.0", {"center": v(83.52, 399.08) * mm, "radius": 5.9 * mm});
            skCircle(sketch, "E5.16.18.0", {"center": v(83.52, 373.68) * mm, "radius": 5.9 * mm});
            skCircle(sketch, "E5.16.19.0", {"center": v(83.52, 348.28) * mm, "radius": 5.9 * mm});
            skCircle(sketch, "E5.16.20.0", {"center": v(83.52, 322.88) * mm, "radius": 5.9 * mm});
            skCircle(sketch, "E5.16.21.0", {"center": v(83.52, 297.48) * mm, "radius": 5.9 * mm});
            skCircle(sketch, "E5.16.22.0", {"center": v(83.52, 272.08) * mm, "radius": 5.9 * mm});
            skCircle(sketch, "E5.16.23.0", {"center": v(83.52, 246.68) * mm, "radius": 5.9 * mm});
            skCircle(sketch, "E5.16.24.0", {"center": v(83.52, 221.28) * mm, "radius": 5.9 * mm});
            skCircle(sketch, "E5.17.0.0", {"center": v(108.92, 830.88) * mm, "radius": 5.9 * mm});
            skCircle(sketch, "E5.17.1.0", {"center": v(108.92, 805.48) * mm, "radius": 5.9 * mm});
            skCircle(sketch, "E5.17.2.0", {"center": v(108.92, 780.08) * mm, "radius": 5.9 * mm});
            skCircle(sketch, "E5.17.3.0", {"center": v(108.92, 754.68) * mm, "radius": 5.9 * mm});
            skCircle(sketch, "E5.17.4.0", {"center": v(108.92, 729.28) * mm, "radius": 5.9 * mm});
            skCircle(sketch, "E5.17.5.0", {"center": v(108.92, 703.88) * mm, "radius": 5.9 * mm});
            skCircle(sketch, "E5.17.6.0", {"center": v(108.92, 678.48) * mm, "radius": 5.9 * mm});
            skCircle(sketch, "E5.17.7.0", {"center": v(108.92, 653.08) * mm, "radius": 5.9 * mm});
            skCircle(sketch, "E5.17.8.0", {"center": v(108.92, 627.68) * mm, "radius": 5.9 * mm});
            skCircle(sketch, "E5.17.9.0", {"center": v(108.92, 602.28) * mm, "radius": 5.9 * mm});
            skCircle(sketch, "E5.17.10.0", {"center": v(108.92, 576.88) * mm, "radius": 5.9 * mm});
            skCircle(sketch, "E5.17.11.0", {"center": v(108.92, 551.48) * mm, "radius": 5.9 * mm});
            skCircle(sketch, "E5.17.12.0", {"center": v(108.92, 526.08) * mm, "radius": 5.9 * mm});
            skCircle(sketch, "E5.17.13.0", {"center": v(108.92, 500.68) * mm, "radius": 5.9 * mm});
            skCircle(sketch, "E5.17.14.0", {"center": v(108.92, 475.28) * mm, "radius": 5.9 * mm});
            skCircle(sketch, "E5.17.15.0", {"center": v(108.92, 449.88) * mm, "radius": 5.9 * mm});
            skCircle(sketch, "E5.17.16.0", {"center": v(108.92, 424.48) * mm, "radius": 5.9 * mm});
            skCircle(sketch, "E5.17.17.0", {"center": v(108.92, 399.08) * mm, "radius": 5.9 * mm});
            skCircle(sketch, "E5.17.18.0", {"center": v(108.92, 373.68) * mm, "radius": 5.9 * mm});
            skCircle(sketch, "E5.17.19.0", {"center": v(108.92, 348.28) * mm, "radius": 5.9 * mm});
            skCircle(sketch, "E5.17.20.0", {"center": v(108.92, 322.88) * mm, "radius": 5.9 * mm});
            skCircle(sketch, "E5.17.21.0", {"center": v(108.92, 297.48) * mm, "radius": 5.9 * mm});
            skCircle(sketch, "E5.17.22.0", {"center": v(108.92, 272.08) * mm, "radius": 5.9 * mm});
            skCircle(sketch, "E5.17.23.0", {"center": v(108.92, 246.68) * mm, "radius": 5.9 * mm});
            skCircle(sketch, "E5.17.24.0", {"center": v(108.92, 221.28) * mm, "radius": 5.9 * mm});
            skCircle(sketch, "E5.18.0.0", {"center": v(134.32, 830.88) * mm, "radius": 5.9 * mm});
            skCircle(sketch, "E5.18.1.0", {"center": v(134.32, 805.48) * mm, "radius": 5.9 * mm});
            skCircle(sketch, "E5.18.2.0", {"center": v(134.32, 780.08) * mm, "radius": 5.9 * mm});
            skCircle(sketch, "E5.18.3.0", {"center": v(134.32, 754.68) * mm, "radius": 5.9 * mm});
            skCircle(sketch, "E5.18.4.0", {"center": v(134.32, 729.28) * mm, "radius": 5.9 * mm});
            skCircle(sketch, "E5.18.5.0", {"center": v(134.32, 703.88) * mm, "radius": 5.9 * mm});
            skCircle(sketch, "E5.18.6.0", {"center": v(134.32, 678.48) * mm, "radius": 5.9 * mm});
            skCircle(sketch, "E5.18.7.0", {"center": v(134.32, 653.08) * mm, "radius": 5.9 * mm});
            skCircle(sketch, "E5.18.8.0", {"center": v(134.32, 627.68) * mm, "radius": 5.9 * mm});
            skCircle(sketch, "E5.18.9.0", {"center": v(134.32, 602.28) * mm, "radius": 5.9 * mm});
            skCircle(sketch, "E5.18.10.0", {"center": v(134.32, 576.88) * mm, "radius": 5.9 * mm});
            skCircle(sketch, "E5.18.11.0", {"center": v(134.32, 551.48) * mm, "radius": 5.9 * mm});
            skCircle(sketch, "E5.18.12.0", {"center": v(134.32, 526.08) * mm, "radius": 5.9 * mm});
            skCircle(sketch, "E5.18.13.0", {"center": v(134.32, 500.68) * mm, "radius": 5.9 * mm});
            skCircle(sketch, "E5.18.14.0", {"center": v(134.32, 475.28) * mm, "radius": 5.9 * mm});
            skCircle(sketch, "E5.18.15.0", {"center": v(134.32, 449.88) * mm, "radius": 5.9 * mm});
            skCircle(sketch, "E5.18.16.0", {"center": v(134.32, 424.48) * mm, "radius": 5.9 * mm});
            skCircle(sketch, "E5.18.17.0", {"center": v(134.32, 399.08) * mm, "radius": 5.9 * mm});
            skCircle(sketch, "E5.18.18.0", {"center": v(134.32, 373.68) * mm, "radius": 5.9 * mm});
            skCircle(sketch, "E5.18.19.0", {"center": v(134.32, 348.28) * mm, "radius": 5.9 * mm});
            skCircle(sketch, "E5.18.20.0", {"center": v(134.32, 322.88) * mm, "radius": 5.9 * mm});
            skCircle(sketch, "E5.18.21.0", {"center": v(134.32, 297.48) * mm, "radius": 5.9 * mm});
            skCircle(sketch, "E5.18.22.0", {"center": v(134.32, 272.08) * mm, "radius": 5.9 * mm});
            skCircle(sketch, "E5.18.23.0", {"center": v(134.32, 246.68) * mm, "radius": 5.9 * mm});
            skCircle(sketch, "E5.18.24.0", {"center": v(134.32, 221.28) * mm, "radius": 5.9 * mm});
            skCircle(sketch, "E5.19.0.0", {"center": v(159.72, 830.88) * mm, "radius": 5.9 * mm});
            skCircle(sketch, "E5.19.1.0", {"center": v(159.72, 805.48) * mm, "radius": 5.9 * mm});
            skCircle(sketch, "E5.19.2.0", {"center": v(159.72, 780.08) * mm, "radius": 5.9 * mm});
            skCircle(sketch, "E5.19.3.0", {"center": v(159.72, 754.68) * mm, "radius": 5.9 * mm});
            skCircle(sketch, "E5.19.4.0", {"center": v(159.72, 729.28) * mm, "radius": 5.9 * mm});
            skCircle(sketch, "E5.19.5.0", {"center": v(159.72, 703.88) * mm, "radius": 5.9 * mm});
            skCircle(sketch, "E5.19.6.0", {"center": v(159.72, 678.48) * mm, "radius": 5.9 * mm});
            skCircle(sketch, "E5.19.7.0", {"center": v(159.72, 653.08) * mm, "radius": 5.9 * mm});
            skCircle(sketch, "E5.19.8.0", {"center": v(159.72, 627.68) * mm, "radius": 5.9 * mm});
            skCircle(sketch, "E5.19.9.0", {"center": v(159.72, 602.28) * mm, "radius": 5.9 * mm});
            skCircle(sketch, "E5.19.10.0", {"center": v(159.72, 576.88) * mm, "radius": 5.9 * mm});
            skCircle(sketch, "E5.19.11.0", {"center": v(159.72, 551.48) * mm, "radius": 5.9 * mm});
            skCircle(sketch, "E5.19.12.0", {"center": v(159.72, 526.08) * mm, "radius": 5.9 * mm});
            skCircle(sketch, "E5.19.13.0", {"center": v(159.72, 500.68) * mm, "radius": 5.9 * mm});
            skCircle(sketch, "E5.19.14.0", {"center": v(159.72, 475.28) * mm, "radius": 5.9 * mm});
            skCircle(sketch, "E5.19.15.0", {"center": v(159.72, 449.88) * mm, "radius": 5.9 * mm});
            skCircle(sketch, "E5.19.16.0", {"center": v(159.72, 424.48) * mm, "radius": 5.9 * mm});
            skCircle(sketch, "E5.19.17.0", {"center": v(159.72, 399.08) * mm, "radius": 5.9 * mm});
            skCircle(sketch, "E5.19.18.0", {"center": v(159.72, 373.68) * mm, "radius": 5.9 * mm});
            skCircle(sketch, "E5.19.19.0", {"center": v(159.72, 348.28) * mm, "radius": 5.9 * mm});
            skCircle(sketch, "E5.19.20.0", {"center": v(159.72, 322.88) * mm, "radius": 5.9 * mm});
            skCircle(sketch, "E5.19.21.0", {"center": v(159.72, 297.48) * mm, "radius": 5.9 * mm});
            skCircle(sketch, "E5.19.22.0", {"center": v(159.72, 272.08) * mm, "radius": 5.9 * mm});
            skCircle(sketch, "E5.19.23.0", {"center": v(159.72, 246.68) * mm, "radius": 5.9 * mm});
            skCircle(sketch, "E5.19.24.0", {"center": v(159.72, 221.28) * mm, "radius": 5.9 * mm});
            skCircle(sketch, "E5.20.0.0", {"center": v(185.12, 830.88) * mm, "radius": 5.9 * mm});
            skCircle(sketch, "E5.20.1.0", {"center": v(185.12, 805.48) * mm, "radius": 5.9 * mm});
            skCircle(sketch, "E5.20.2.0", {"center": v(185.12, 780.08) * mm, "radius": 5.9 * mm});
            skCircle(sketch, "E5.20.3.0", {"center": v(185.12, 754.68) * mm, "radius": 5.9 * mm});
            skCircle(sketch, "E5.20.4.0", {"center": v(185.12, 729.28) * mm, "radius": 5.9 * mm});
            skCircle(sketch, "E5.20.5.0", {"center": v(185.12, 703.88) * mm, "radius": 5.9 * mm});
            skCircle(sketch, "E5.20.6.0", {"center": v(185.12, 678.48) * mm, "radius": 5.9 * mm});
            skCircle(sketch, "E5.20.7.0", {"center": v(185.12, 653.08) * mm, "radius": 5.9 * mm});
            skCircle(sketch, "E5.20.8.0", {"center": v(185.12, 627.68) * mm, "radius": 5.9 * mm});
            skCircle(sketch, "E5.20.9.0", {"center": v(185.12, 602.28) * mm, "radius": 5.9 * mm});
            skCircle(sketch, "E5.20.10.0", {"center": v(185.12, 576.88) * mm, "radius": 5.9 * mm});
            skCircle(sketch, "E5.20.11.0", {"center": v(185.12, 551.48) * mm, "radius": 5.9 * mm});
            skCircle(sketch, "E5.20.12.0", {"center": v(185.12, 526.08) * mm, "radius": 5.9 * mm});
            skCircle(sketch, "E5.20.13.0", {"center": v(185.12, 500.68) * mm, "radius": 5.9 * mm});
            skCircle(sketch, "E5.20.14.0", {"center": v(185.12, 475.28) * mm, "radius": 5.9 * mm});
            skCircle(sketch, "E5.20.15.0", {"center": v(185.12, 449.88) * mm, "radius": 5.9 * mm});
            skCircle(sketch, "E5.20.16.0", {"center": v(185.12, 424.48) * mm, "radius": 5.9 * mm});
            skCircle(sketch, "E5.20.17.0", {"center": v(185.12, 399.08) * mm, "radius": 5.9 * mm});
            skCircle(sketch, "E5.20.18.0", {"center": v(185.12, 373.68) * mm, "radius": 5.9 * mm});
            skCircle(sketch, "E5.20.19.0", {"center": v(185.12, 348.28) * mm, "radius": 5.9 * mm});
            skCircle(sketch, "E5.20.20.0", {"center": v(185.12, 322.88) * mm, "radius": 5.9 * mm});
            skCircle(sketch, "E5.20.21.0", {"center": v(185.12, 297.48) * mm, "radius": 5.9 * mm});
            skCircle(sketch, "E5.20.22.0", {"center": v(185.12, 272.08) * mm, "radius": 5.9 * mm});
            skCircle(sketch, "E5.20.23.0", {"center": v(185.12, 246.68) * mm, "radius": 5.9 * mm});
            skCircle(sketch, "E5.20.24.0", {"center": v(185.12, 221.28) * mm, "radius": 5.9 * mm});
            skCircle(sketch, "E5.21.0.0", {"center": v(210.52, 830.88) * mm, "radius": 5.9 * mm});
            skCircle(sketch, "E5.21.1.0", {"center": v(210.52, 805.48) * mm, "radius": 5.9 * mm});
            skCircle(sketch, "E5.21.2.0", {"center": v(210.52, 780.08) * mm, "radius": 5.9 * mm});
            skCircle(sketch, "E5.21.3.0", {"center": v(210.52, 754.68) * mm, "radius": 5.9 * mm});
            skCircle(sketch, "E5.21.4.0", {"center": v(210.52, 729.28) * mm, "radius": 5.9 * mm});
            skCircle(sketch, "E5.21.5.0", {"center": v(210.52, 703.88) * mm, "radius": 5.9 * mm});
            skCircle(sketch, "E5.21.6.0", {"center": v(210.52, 678.48) * mm, "radius": 5.9 * mm});
            skCircle(sketch, "E5.21.7.0", {"center": v(210.52, 653.08) * mm, "radius": 5.9 * mm});
            skCircle(sketch, "E5.21.8.0", {"center": v(210.52, 627.68) * mm, "radius": 5.9 * mm});
            skCircle(sketch, "E5.21.9.0", {"center": v(210.52, 602.28) * mm, "radius": 5.9 * mm});
            skCircle(sketch, "E5.21.10.0", {"center": v(210.52, 576.88) * mm, "radius": 5.9 * mm});
            skCircle(sketch, "E5.21.11.0", {"center": v(210.52, 551.48) * mm, "radius": 5.9 * mm});
            skCircle(sketch, "E5.21.12.0", {"center": v(210.52, 526.08) * mm, "radius": 5.9 * mm});
            skCircle(sketch, "E5.21.13.0", {"center": v(210.52, 500.68) * mm, "radius": 5.9 * mm});
            skCircle(sketch, "E5.21.14.0", {"center": v(210.52, 475.28) * mm, "radius": 5.9 * mm});
            skCircle(sketch, "E5.21.15.0", {"center": v(210.52, 449.88) * mm, "radius": 5.9 * mm});
            skCircle(sketch, "E5.21.16.0", {"center": v(210.52, 424.48) * mm, "radius": 5.9 * mm});
            skCircle(sketch, "E5.21.17.0", {"center": v(210.52, 399.08) * mm, "radius": 5.9 * mm});
            skCircle(sketch, "E5.21.18.0", {"center": v(210.52, 373.68) * mm, "radius": 5.9 * mm});
            skCircle(sketch, "E5.21.19.0", {"center": v(210.52, 348.28) * mm, "radius": 5.9 * mm});
            skCircle(sketch, "E5.21.20.0", {"center": v(210.52, 322.88) * mm, "radius": 5.9 * mm});
            skCircle(sketch, "E5.21.21.0", {"center": v(210.52, 297.48) * mm, "radius": 5.9 * mm});
            skCircle(sketch, "E5.21.22.0", {"center": v(210.52, 272.08) * mm, "radius": 5.9 * mm});
            skCircle(sketch, "E5.21.23.0", {"center": v(210.52, 246.68) * mm, "radius": 5.9 * mm});
            skCircle(sketch, "E5.21.24.0", {"center": v(210.52, 221.28) * mm, "radius": 5.9 * mm});
            skCircle(sketch, "E5.22.0.0", {"center": v(235.92, 830.88) * mm, "radius": 5.9 * mm});
            skCircle(sketch, "E5.22.1.0", {"center": v(235.92, 805.48) * mm, "radius": 5.9 * mm});
            skCircle(sketch, "E5.22.2.0", {"center": v(235.92, 780.08) * mm, "radius": 5.9 * mm});
            skCircle(sketch, "E5.22.3.0", {"center": v(235.92, 754.68) * mm, "radius": 5.9 * mm});
            skCircle(sketch, "E5.22.4.0", {"center": v(235.92, 729.28) * mm, "radius": 5.9 * mm});
            skCircle(sketch, "E5.22.5.0", {"center": v(235.92, 703.88) * mm, "radius": 5.9 * mm});
            skCircle(sketch, "E5.22.6.0", {"center": v(235.92, 678.48) * mm, "radius": 5.9 * mm});
            skCircle(sketch, "E5.22.7.0", {"center": v(235.92, 653.08) * mm, "radius": 5.9 * mm});
            skCircle(sketch, "E5.22.8.0", {"center": v(235.92, 627.68) * mm, "radius": 5.9 * mm});
            skCircle(sketch, "E5.22.9.0", {"center": v(235.92, 602.28) * mm, "radius": 5.9 * mm});
            skCircle(sketch, "E5.22.10.0", {"center": v(235.92, 576.88) * mm, "radius": 5.9 * mm});
            skCircle(sketch, "E5.22.11.0", {"center": v(235.92, 551.48) * mm, "radius": 5.9 * mm});
            skCircle(sketch, "E5.22.12.0", {"center": v(235.92, 526.08) * mm, "radius": 5.9 * mm});
            skCircle(sketch, "E5.22.13.0", {"center": v(235.92, 500.68) * mm, "radius": 5.9 * mm});
            skCircle(sketch, "E5.22.14.0", {"center": v(235.92, 475.28) * mm, "radius": 5.9 * mm});
            skCircle(sketch, "E5.22.15.0", {"center": v(235.92, 449.88) * mm, "radius": 5.9 * mm});
            skCircle(sketch, "E5.22.16.0", {"center": v(235.92, 424.48) * mm, "radius": 5.9 * mm});
            skCircle(sketch, "E5.22.17.0", {"center": v(235.92, 399.08) * mm, "radius": 5.9 * mm});
            skCircle(sketch, "E5.22.18.0", {"center": v(235.92, 373.68) * mm, "radius": 5.9 * mm});
            skCircle(sketch, "E5.22.19.0", {"center": v(235.92, 348.28) * mm, "radius": 5.9 * mm});
            skCircle(sketch, "E5.22.20.0", {"center": v(235.92, 322.88) * mm, "radius": 5.9 * mm});
            skCircle(sketch, "E5.22.21.0", {"center": v(235.92, 297.48) * mm, "radius": 5.9 * mm});
            skCircle(sketch, "E5.22.22.0", {"center": v(235.92, 272.08) * mm, "radius": 5.9 * mm});
            skCircle(sketch, "E5.22.23.0", {"center": v(235.92, 246.68) * mm, "radius": 5.9 * mm});
            skCircle(sketch, "E5.22.24.0", {"center": v(235.92, 221.28) * mm, "radius": 5.9 * mm});
            skCircle(sketch, "E5.23.0.0", {"center": v(261.32, 830.88) * mm, "radius": 5.9 * mm});
            skCircle(sketch, "E5.23.1.0", {"center": v(261.32, 805.48) * mm, "radius": 5.9 * mm});
            skCircle(sketch, "E5.23.2.0", {"center": v(261.32, 780.08) * mm, "radius": 5.9 * mm});
            skCircle(sketch, "E5.23.3.0", {"center": v(261.32, 754.68) * mm, "radius": 5.9 * mm});
            skCircle(sketch, "E5.23.4.0", {"center": v(261.32, 729.28) * mm, "radius": 5.9 * mm});
            skCircle(sketch, "E5.23.5.0", {"center": v(261.32, 703.88) * mm, "radius": 5.9 * mm});
            skCircle(sketch, "E5.23.6.0", {"center": v(261.32, 678.48) * mm, "radius": 5.9 * mm});
            skCircle(sketch, "E5.23.7.0", {"center": v(261.32, 653.08) * mm, "radius": 5.9 * mm});
            skCircle(sketch, "E5.23.8.0", {"center": v(261.32, 627.68) * mm, "radius": 5.9 * mm});
            skCircle(sketch, "E5.23.9.0", {"center": v(261.32, 602.28) * mm, "radius": 5.9 * mm});
            skCircle(sketch, "E5.23.10.0", {"center": v(261.32, 576.88) * mm, "radius": 5.9 * mm});
            skCircle(sketch, "E5.23.11.0", {"center": v(261.32, 551.48) * mm, "radius": 5.9 * mm});
            skCircle(sketch, "E5.23.12.0", {"center": v(261.32, 526.08) * mm, "radius": 5.9 * mm});
            skCircle(sketch, "E5.23.13.0", {"center": v(261.32, 500.68) * mm, "radius": 5.9 * mm});
            skCircle(sketch, "E5.23.14.0", {"center": v(261.32, 475.28) * mm, "radius": 5.9 * mm});
            skCircle(sketch, "E5.23.15.0", {"center": v(261.32, 449.88) * mm, "radius": 5.9 * mm});
            skCircle(sketch, "E5.23.16.0", {"center": v(261.32, 424.48) * mm, "radius": 5.9 * mm});
            skCircle(sketch, "E5.23.17.0", {"center": v(261.32, 399.08) * mm, "radius": 5.9 * mm});
            skCircle(sketch, "E5.23.18.0", {"center": v(261.32, 373.68) * mm, "radius": 5.9 * mm});
            skCircle(sketch, "E5.23.19.0", {"center": v(261.32, 348.28) * mm, "radius": 5.9 * mm});
            skCircle(sketch, "E5.23.20.0", {"center": v(261.32, 322.88) * mm, "radius": 5.9 * mm});
            skCircle(sketch, "E5.23.21.0", {"center": v(261.32, 297.48) * mm, "radius": 5.9 * mm});
            skCircle(sketch, "E5.23.22.0", {"center": v(261.32, 272.08) * mm, "radius": 5.9 * mm});
            skCircle(sketch, "E5.23.23.0", {"center": v(261.32, 246.68) * mm, "radius": 5.9 * mm});
            skCircle(sketch, "E5.23.24.0", {"center": v(261.32, 221.28) * mm, "radius": 5.9 * mm});
            skCircle(sketch, "E5.24.0.0", {"center": v(286.72, 830.88) * mm, "radius": 5.9 * mm});
            skCircle(sketch, "E5.24.1.0", {"center": v(286.72, 805.48) * mm, "radius": 5.9 * mm});
            skCircle(sketch, "E5.24.2.0", {"center": v(286.72, 780.08) * mm, "radius": 5.9 * mm});
            skCircle(sketch, "E5.24.3.0", {"center": v(286.72, 754.68) * mm, "radius": 5.9 * mm});
            skCircle(sketch, "E5.24.4.0", {"center": v(286.72, 729.28) * mm, "radius": 5.9 * mm});
            skCircle(sketch, "E5.24.5.0", {"center": v(286.72, 703.88) * mm, "radius": 5.9 * mm});
            skCircle(sketch, "E5.24.6.0", {"center": v(286.72, 678.48) * mm, "radius": 5.9 * mm});
            skCircle(sketch, "E5.24.7.0", {"center": v(286.72, 653.08) * mm, "radius": 5.9 * mm});
            skCircle(sketch, "E5.24.8.0", {"center": v(286.72, 627.68) * mm, "radius": 5.9 * mm});
            skCircle(sketch, "E5.24.9.0", {"center": v(286.72, 602.28) * mm, "radius": 5.9 * mm});
            skCircle(sketch, "E5.24.10.0", {"center": v(286.72, 576.88) * mm, "radius": 5.9 * mm});
            skCircle(sketch, "E5.24.11.0", {"center": v(286.72, 551.48) * mm, "radius": 5.9 * mm});
            skCircle(sketch, "E5.24.12.0", {"center": v(286.72, 526.08) * mm, "radius": 5.9 * mm});
            skCircle(sketch, "E5.24.13.0", {"center": v(286.72, 500.68) * mm, "radius": 5.9 * mm});
            skCircle(sketch, "E5.24.14.0", {"center": v(286.72, 475.28) * mm, "radius": 5.9 * mm});
            skCircle(sketch, "E5.24.15.0", {"center": v(286.72, 449.88) * mm, "radius": 5.9 * mm});
            skCircle(sketch, "E5.24.16.0", {"center": v(286.72, 424.48) * mm, "radius": 5.9 * mm});
            skCircle(sketch, "E5.24.17.0", {"center": v(286.72, 399.08) * mm, "radius": 5.9 * mm});
            skCircle(sketch, "E5.24.18.0", {"center": v(286.72, 373.68) * mm, "radius": 5.9 * mm});
            skCircle(sketch, "E5.24.19.0", {"center": v(286.72, 348.28) * mm, "radius": 5.9 * mm});
            skCircle(sketch, "E5.24.20.0", {"center": v(286.72, 322.88) * mm, "radius": 5.9 * mm});
            skCircle(sketch, "E5.24.21.0", {"center": v(286.72, 297.48) * mm, "radius": 5.9 * mm});
            skCircle(sketch, "E5.24.22.0", {"center": v(286.72, 272.08) * mm, "radius": 5.9 * mm});
            skCircle(sketch, "E5.24.23.0", {"center": v(286.72, 246.68) * mm, "radius": 5.9 * mm});
            skCircle(sketch, "E5.24.24.0", {"center": v(286.72, 221.28) * mm, "radius": 5.9 * mm});
            skLineSegment(sketch, "E5.direction1", {"start": v(-322.88, 830.88) * mm, "end": v(-297.48, 830.88) * mm, "construction": true});
            skLineSegment(sketch, "E5.direction2", {"start": v(-322.88, 830.88) * mm, "end": v(-322.88, 805.48) * mm, "construction": true});
            skCircle(sketch, "E6.0.25.0", {"center": v(312.12, 830.88) * mm, "radius": 5.9 * mm});
            skCircle(sketch, "E6.0.25.1", {"center": v(312.12, 805.48) * mm, "radius": 5.9 * mm});
            skCircle(sketch, "E6.0.25.2", {"center": v(312.12, 780.08) * mm, "radius": 5.9 * mm});
            skCircle(sketch, "E6.0.25.3", {"center": v(312.12, 754.68) * mm, "radius": 5.9 * mm});
            skCircle(sketch, "E6.0.25.4", {"center": v(312.12, 729.28) * mm, "radius": 5.9 * mm});
            skCircle(sketch, "E6.0.25.5", {"center": v(312.12, 703.88) * mm, "radius": 5.9 * mm});
            skCircle(sketch, "E6.0.25.6", {"center": v(312.12, 678.48) * mm, "radius": 5.9 * mm});
            skCircle(sketch, "E6.0.25.7", {"center": v(312.12, 653.08) * mm, "radius": 5.9 * mm});
            skCircle(sketch, "E6.0.25.8", {"center": v(312.12, 627.68) * mm, "radius": 5.9 * mm});
            skCircle(sketch, "E6.0.25.9", {"center": v(312.12, 602.28) * mm, "radius": 5.9 * mm});
            skCircle(sketch, "E6.0.25.10", {"center": v(312.12, 576.88) * mm, "radius": 5.9 * mm});
            skCircle(sketch, "E6.0.25.11", {"center": v(312.12, 551.48) * mm, "radius": 5.9 * mm});
            skCircle(sketch, "E6.0.25.12", {"center": v(312.12, 526.08) * mm, "radius": 5.9 * mm});
            skCircle(sketch, "E6.0.25.13", {"center": v(312.12, 500.68) * mm, "radius": 5.9 * mm});
            skCircle(sketch, "E6.0.25.14", {"center": v(312.12, 475.28) * mm, "radius": 5.9 * mm});
            skCircle(sketch, "E6.0.25.15", {"center": v(312.12, 449.88) * mm, "radius": 5.9 * mm});
            skCircle(sketch, "E6.0.25.16", {"center": v(312.12, 424.48) * mm, "radius": 5.9 * mm});
            skCircle(sketch, "E6.0.25.17", {"center": v(312.12, 399.08) * mm, "radius": 5.9 * mm});
            skCircle(sketch, "E6.0.25.18", {"center": v(312.12, 373.68) * mm, "radius": 5.9 * mm});
            skCircle(sketch, "E6.0.25.19", {"center": v(312.12, 348.28) * mm, "radius": 5.9 * mm});
            skCircle(sketch, "E6.0.25.20", {"center": v(312.12, 322.88) * mm, "radius": 5.9 * mm});
            skCircle(sketch, "E6.0.25.21", {"center": v(312.12, 297.48) * mm, "radius": 5.9 * mm});
            skCircle(sketch, "E6.0.25.22", {"center": v(312.12, 272.08) * mm, "radius": 5.9 * mm});
            skCircle(sketch, "E6.0.25.23", {"center": v(312.12, 246.68) * mm, "radius": 5.9 * mm});
            skCircle(sketch, "E6.0.25.24", {"center": v(312.12, 221.28) * mm, "radius": 5.9 * mm});
            skCircle(sketch, "E7.0.0.25", {"center": v(-322.88, 195.88) * mm, "radius": 5.9 * mm});
            skCircle(sketch, "E7.0.0.26", {"center": v(-322.88, 170.48) * mm, "radius": 5.9 * mm});
            skCircle(sketch, "E7.0.0.27", {"center": v(-322.88, 145.08) * mm, "radius": 5.9 * mm});
            skCircle(sketch, "E7.0.0.28", {"center": v(-322.88, 119.68) * mm, "radius": 5.9 * mm});
            skCircle(sketch, "E7.0.0.29", {"center": v(-322.88, 94.28) * mm, "radius": 5.9 * mm});
            skCircle(sketch, "E7.0.0.30", {"center": v(-322.88, 68.88) * mm, "radius": 5.9 * mm});
            skCircle(sketch, "E7.0.0.31", {"center": v(-322.88, 43.48) * mm, "radius": 5.9 * mm});
            skCircle(sketch, "E7.0.0.32", {"center": v(-322.88, 18.08) * mm, "radius": 5.9 * mm});
            skCircle(sketch, "E7.0.0.33", {"center": v(-322.88, -7.32) * mm, "radius": 5.9 * mm});
            skCircle(sketch, "E7.0.0.34", {"center": v(-322.88, -32.72) * mm, "radius": 5.9 * mm});
            skCircle(sketch, "E7.0.0.35", {"center": v(-322.88, -58.12) * mm, "radius": 5.9 * mm});
            skCircle(sketch, "E7.0.0.36", {"center": v(-322.88, -83.52) * mm, "radius": 5.9 * mm});
            skCircle(sketch, "E7.0.0.37", {"center": v(-322.88, -108.92) * mm, "radius": 5.9 * mm});
            skCircle(sketch, "E7.0.0.38", {"center": v(-322.88, -134.32) * mm, "radius": 5.9 * mm});
            skCircle(sketch, "E7.0.0.39", {"center": v(-322.88, -159.72) * mm, "radius": 5.9 * mm});
            skCircle(sketch, "E7.0.0.40", {"center": v(-322.88, -185.12) * mm, "radius": 5.9 * mm});
            skCircle(sketch, "E7.0.0.41", {"center": v(-322.88, -210.52) * mm, "radius": 5.9 * mm});
            skCircle(sketch, "E7.0.0.42", {"center": v(-322.88, -235.92) * mm, "radius": 5.9 * mm});
            skCircle(sketch, "E7.0.0.43", {"center": v(-322.88, -261.32) * mm, "radius": 5.9 * mm});
            skCircle(sketch, "E7.0.0.44", {"center": v(-322.88, -286.72) * mm, "radius": 5.9 * mm});
            skCircle(sketch, "E7.0.0.45", {"center": v(-322.88, -312.12) * mm, "radius": 5.9 * mm});
            skCircle(sketch, "E7.0.0.46", {"center": v(-322.88, -337.52) * mm, "radius": 5.9 * mm});
            skCircle(sketch, "E7.0.0.47", {"center": v(-322.88, -362.92) * mm, "radius": 5.9 * mm});
            skCircle(sketch, "E7.0.0.48", {"center": v(-322.88, -388.32) * mm, "radius": 5.9 * mm});
            skCircle(sketch, "E7.0.0.49", {"center": v(-322.88, -413.72) * mm, "radius": 5.9 * mm});
            skCircle(sketch, "E7.0.0.50", {"center": v(-322.88, -439.12) * mm, "radius": 5.9 * mm});
            skCircle(sketch, "E7.0.0.51", {"center": v(-322.88, -464.52) * mm, "radius": 5.9 * mm});
            skCircle(sketch, "E7.0.0.52", {"center": v(-322.88, -489.92) * mm, "radius": 5.9 * mm});
            skCircle(sketch, "E7.0.0.53", {"center": v(-322.88, -515.32) * mm, "radius": 5.9 * mm});
            skCircle(sketch, "E7.0.0.54", {"center": v(-322.88, -540.72) * mm, "radius": 5.9 * mm});
            skCircle(sketch, "E7.0.0.55", {"center": v(-322.88, -566.12) * mm, "radius": 5.9 * mm});
            skCircle(sketch, "E7.0.0.56", {"center": v(-322.88, -591.52) * mm, "radius": 5.9 * mm});
            skCircle(sketch, "E7.0.0.57", {"center": v(-322.88, -616.92) * mm, "radius": 5.9 * mm});
            skCircle(sketch, "E7.0.0.58", {"center": v(-322.88, -642.32) * mm, "radius": 5.9 * mm});
            skCircle(sketch, "E7.0.0.59", {"center": v(-322.88, -667.72) * mm, "radius": 5.9 * mm});
            skCircle(sketch, "E7.0.0.60", {"center": v(-322.88, -693.12) * mm, "radius": 5.9 * mm});
            skCircle(sketch, "E7.0.0.61", {"center": v(-322.88, -718.52) * mm, "radius": 5.9 * mm});
            skCircle(sketch, "E7.0.0.62", {"center": v(-322.88, -743.92) * mm, "radius": 5.9 * mm});
            skCircle(sketch, "E7.0.0.63", {"center": v(-322.88, -769.32) * mm, "radius": 5.9 * mm});
            skCircle(sketch, "E7.0.0.64", {"center": v(-322.88, -794.72) * mm, "radius": 5.9 * mm});
            skCircle(sketch, "E7.0.1.25", {"center": v(-297.48, 195.88) * mm, "radius": 5.9 * mm});
            skCircle(sketch, "E7.0.1.26", {"center": v(-297.48, 170.48) * mm, "radius": 5.9 * mm});
            skCircle(sketch, "E7.0.1.27", {"center": v(-297.48, 145.08) * mm, "radius": 5.9 * mm});
            skCircle(sketch, "E7.0.1.28", {"center": v(-297.48, 119.68) * mm, "radius": 5.9 * mm});
            skCircle(sketch, "E7.0.1.29", {"center": v(-297.48, 94.28) * mm, "radius": 5.9 * mm});
            skCircle(sketch, "E7.0.1.30", {"center": v(-297.48, 68.88) * mm, "radius": 5.9 * mm});
            skCircle(sketch, "E7.0.1.31", {"center": v(-297.48, 43.48) * mm, "radius": 5.9 * mm});
            skCircle(sketch, "E7.0.1.32", {"center": v(-297.48, 18.08) * mm, "radius": 5.9 * mm});
            skCircle(sketch, "E7.0.1.33", {"center": v(-297.48, -7.32) * mm, "radius": 5.9 * mm});
            skCircle(sketch, "E7.0.1.34", {"center": v(-297.48, -32.72) * mm, "radius": 5.9 * mm});
            skCircle(sketch, "E7.0.1.35", {"center": v(-297.48, -58.12) * mm, "radius": 5.9 * mm});
            skCircle(sketch, "E7.0.1.36", {"center": v(-297.48, -83.52) * mm, "radius": 5.9 * mm});
            skCircle(sketch, "E7.0.1.37", {"center": v(-297.48, -108.92) * mm, "radius": 5.9 * mm});
            skCircle(sketch, "E7.0.1.38", {"center": v(-297.48, -134.32) * mm, "radius": 5.9 * mm});
            skCircle(sketch, "E7.0.1.39", {"center": v(-297.48, -159.72) * mm, "radius": 5.9 * mm});
            skCircle(sketch, "E7.0.1.40", {"center": v(-297.48, -185.12) * mm, "radius": 5.9 * mm});
            skCircle(sketch, "E7.0.1.41", {"center": v(-297.48, -210.52) * mm, "radius": 5.9 * mm});
            skCircle(sketch, "E7.0.1.42", {"center": v(-297.48, -235.92) * mm, "radius": 5.9 * mm});
            skCircle(sketch, "E7.0.1.43", {"center": v(-297.48, -261.32) * mm, "radius": 5.9 * mm});
            skCircle(sketch, "E7.0.1.44", {"center": v(-297.48, -286.72) * mm, "radius": 5.9 * mm});
            skCircle(sketch, "E7.0.1.45", {"center": v(-297.48, -312.12) * mm, "radius": 5.9 * mm});
            skCircle(sketch, "E7.0.1.46", {"center": v(-297.48, -337.52) * mm, "radius": 5.9 * mm});
            skCircle(sketch, "E7.0.1.47", {"center": v(-297.48, -362.92) * mm, "radius": 5.9 * mm});
            skCircle(sketch, "E7.0.1.48", {"center": v(-297.48, -388.32) * mm, "radius": 5.9 * mm});
            skCircle(sketch, "E7.0.1.49", {"center": v(-297.48, -413.72) * mm, "radius": 5.9 * mm});
            skCircle(sketch, "E7.0.1.50", {"center": v(-297.48, -439.12) * mm, "radius": 5.9 * mm});
            skCircle(sketch, "E7.0.1.51", {"center": v(-297.48, -464.52) * mm, "radius": 5.9 * mm});
            skCircle(sketch, "E7.0.1.52", {"center": v(-297.48, -489.92) * mm, "radius": 5.9 * mm});
            skCircle(sketch, "E7.0.1.53", {"center": v(-297.48, -515.32) * mm, "radius": 5.9 * mm});
            skCircle(sketch, "E7.0.1.54", {"center": v(-297.48, -540.72) * mm, "radius": 5.9 * mm});
            skCircle(sketch, "E7.0.1.55", {"center": v(-297.48, -566.12) * mm, "radius": 5.9 * mm});
            skCircle(sketch, "E7.0.1.56", {"center": v(-297.48, -591.52) * mm, "radius": 5.9 * mm});
            skCircle(sketch, "E7.0.1.57", {"center": v(-297.48, -616.92) * mm, "radius": 5.9 * mm});
            skCircle(sketch, "E7.0.1.58", {"center": v(-297.48, -642.32) * mm, "radius": 5.9 * mm});
            skCircle(sketch, "E7.0.1.59", {"center": v(-297.48, -667.72) * mm, "radius": 5.9 * mm});
            skCircle(sketch, "E7.0.1.60", {"center": v(-297.48, -693.12) * mm, "radius": 5.9 * mm});
            skCircle(sketch, "E7.0.1.61", {"center": v(-297.48, -718.52) * mm, "radius": 5.9 * mm});
            skCircle(sketch, "E7.0.1.62", {"center": v(-297.48, -743.92) * mm, "radius": 5.9 * mm});
            skCircle(sketch, "E7.0.1.63", {"center": v(-297.48, -769.32) * mm, "radius": 5.9 * mm});
            skCircle(sketch, "E7.0.1.64", {"center": v(-297.48, -794.72) * mm, "radius": 5.9 * mm});
            skCircle(sketch, "E7.0.2.25", {"center": v(-272.08, 195.88) * mm, "radius": 5.9 * mm});
            skCircle(sketch, "E7.0.2.26", {"center": v(-272.08, 170.48) * mm, "radius": 5.9 * mm});
            skCircle(sketch, "E7.0.2.27", {"center": v(-272.08, 145.08) * mm, "radius": 5.9 * mm});
            skCircle(sketch, "E7.0.2.28", {"center": v(-272.08, 119.68) * mm, "radius": 5.9 * mm});
            skCircle(sketch, "E7.0.2.29", {"center": v(-272.08, 94.28) * mm, "radius": 5.9 * mm});
            skCircle(sketch, "E7.0.2.30", {"center": v(-272.08, 68.88) * mm, "radius": 5.9 * mm});
            skCircle(sketch, "E7.0.2.31", {"center": v(-272.08, 43.48) * mm, "radius": 5.9 * mm});
            skCircle(sketch, "E7.0.2.32", {"center": v(-272.08, 18.08) * mm, "radius": 5.9 * mm});
            skCircle(sketch, "E7.0.2.33", {"center": v(-272.08, -7.32) * mm, "radius": 5.9 * mm});
            skCircle(sketch, "E7.0.2.34", {"center": v(-272.08, -32.72) * mm, "radius": 5.9 * mm});
            skCircle(sketch, "E7.0.2.35", {"center": v(-272.08, -58.12) * mm, "radius": 5.9 * mm});
            skCircle(sketch, "E7.0.2.36", {"center": v(-272.08, -83.52) * mm, "radius": 5.9 * mm});
            skCircle(sketch, "E7.0.2.37", {"center": v(-272.08, -108.92) * mm, "radius": 5.9 * mm});
            skCircle(sketch, "E7.0.2.38", {"center": v(-272.08, -134.32) * mm, "radius": 5.9 * mm});
            skCircle(sketch, "E7.0.2.39", {"center": v(-272.08, -159.72) * mm, "radius": 5.9 * mm});
            skCircle(sketch, "E7.0.2.40", {"center": v(-272.08, -185.12) * mm, "radius": 5.9 * mm});
            skCircle(sketch, "E7.0.2.41", {"center": v(-272.08, -210.52) * mm, "radius": 5.9 * mm});
            skCircle(sketch, "E7.0.2.42", {"center": v(-272.08, -235.92) * mm, "radius": 5.9 * mm});
            skCircle(sketch, "E7.0.2.43", {"center": v(-272.08, -261.32) * mm, "radius": 5.9 * mm});
            skCircle(sketch, "E7.0.2.44", {"center": v(-272.08, -286.72) * mm, "radius": 5.9 * mm});
            skCircle(sketch, "E7.0.2.45", {"center": v(-272.08, -312.12) * mm, "radius": 5.9 * mm});
            skCircle(sketch, "E7.0.2.46", {"center": v(-272.08, -337.52) * mm, "radius": 5.9 * mm});
            skCircle(sketch, "E7.0.2.47", {"center": v(-272.08, -362.92) * mm, "radius": 5.9 * mm});
            skCircle(sketch, "E7.0.2.48", {"center": v(-272.08, -388.32) * mm, "radius": 5.9 * mm});
            skCircle(sketch, "E7.0.2.49", {"center": v(-272.08, -413.72) * mm, "radius": 5.9 * mm});
            skCircle(sketch, "E7.0.2.50", {"center": v(-272.08, -439.12) * mm, "radius": 5.9 * mm});
            skCircle(sketch, "E7.0.2.51", {"center": v(-272.08, -464.52) * mm, "radius": 5.9 * mm});
            skCircle(sketch, "E7.0.2.52", {"center": v(-272.08, -489.92) * mm, "radius": 5.9 * mm});
            skCircle(sketch, "E7.0.2.53", {"center": v(-272.08, -515.32) * mm, "radius": 5.9 * mm});
            skCircle(sketch, "E7.0.2.54", {"center": v(-272.08, -540.72) * mm, "radius": 5.9 * mm});
            skCircle(sketch, "E7.0.2.55", {"center": v(-272.08, -566.12) * mm, "radius": 5.9 * mm});
            skCircle(sketch, "E7.0.2.56", {"center": v(-272.08, -591.52) * mm, "radius": 5.9 * mm});
            skCircle(sketch, "E7.0.2.57", {"center": v(-272.08, -616.92) * mm, "radius": 5.9 * mm});
            skCircle(sketch, "E7.0.2.58", {"center": v(-272.08, -642.32) * mm, "radius": 5.9 * mm});
            skCircle(sketch, "E7.0.2.59", {"center": v(-272.08, -667.72) * mm, "radius": 5.9 * mm});
            skCircle(sketch, "E7.0.2.60", {"center": v(-272.08, -693.12) * mm, "radius": 5.9 * mm});
            skCircle(sketch, "E7.0.2.61", {"center": v(-272.08, -718.52) * mm, "radius": 5.9 * mm});
            skCircle(sketch, "E7.0.2.62", {"center": v(-272.08, -743.92) * mm, "radius": 5.9 * mm});
            skCircle(sketch, "E7.0.2.63", {"center": v(-272.08, -769.32) * mm, "radius": 5.9 * mm});
            skCircle(sketch, "E7.0.2.64", {"center": v(-272.08, -794.72) * mm, "radius": 5.9 * mm});
            skCircle(sketch, "E7.0.3.25", {"center": v(-246.68, 195.88) * mm, "radius": 5.9 * mm});
            skCircle(sketch, "E7.0.3.26", {"center": v(-246.68, 170.48) * mm, "radius": 5.9 * mm});
            skCircle(sketch, "E7.0.3.27", {"center": v(-246.68, 145.08) * mm, "radius": 5.9 * mm});
            skCircle(sketch, "E7.0.3.28", {"center": v(-246.68, 119.68) * mm, "radius": 5.9 * mm});
            skCircle(sketch, "E7.0.3.29", {"center": v(-246.68, 94.28) * mm, "radius": 5.9 * mm});
            skCircle(sketch, "E7.0.3.30", {"center": v(-246.68, 68.88) * mm, "radius": 5.9 * mm});
            skCircle(sketch, "E7.0.3.31", {"center": v(-246.68, 43.48) * mm, "radius": 5.9 * mm});
            skCircle(sketch, "E7.0.3.32", {"center": v(-246.68, 18.08) * mm, "radius": 5.9 * mm});
            skCircle(sketch, "E7.0.3.33", {"center": v(-246.68, -7.32) * mm, "radius": 5.9 * mm});
            skCircle(sketch, "E7.0.3.34", {"center": v(-246.68, -32.72) * mm, "radius": 5.9 * mm});
            skCircle(sketch, "E7.0.3.35", {"center": v(-246.68, -58.12) * mm, "radius": 5.9 * mm});
            skCircle(sketch, "E7.0.3.36", {"center": v(-246.68, -83.52) * mm, "radius": 5.9 * mm});
            skCircle(sketch, "E7.0.3.37", {"center": v(-246.68, -108.92) * mm, "radius": 5.9 * mm});
            skCircle(sketch, "E7.0.3.38", {"center": v(-246.68, -134.32) * mm, "radius": 5.9 * mm});
            skCircle(sketch, "E7.0.3.39", {"center": v(-246.68, -159.72) * mm, "radius": 5.9 * mm});
            skCircle(sketch, "E7.0.3.40", {"center": v(-246.68, -185.12) * mm, "radius": 5.9 * mm});
            skCircle(sketch, "E7.0.3.41", {"center": v(-246.68, -210.52) * mm, "radius": 5.9 * mm});
            skCircle(sketch, "E7.0.3.42", {"center": v(-246.68, -235.92) * mm, "radius": 5.9 * mm});
            skCircle(sketch, "E7.0.3.43", {"center": v(-246.68, -261.32) * mm, "radius": 5.9 * mm});
            skCircle(sketch, "E7.0.3.44", {"center": v(-246.68, -286.72) * mm, "radius": 5.9 * mm});
            skCircle(sketch, "E7.0.3.45", {"center": v(-246.68, -312.12) * mm, "radius": 5.9 * mm});
            skCircle(sketch, "E7.0.3.46", {"center": v(-246.68, -337.52) * mm, "radius": 5.9 * mm});
            skCircle(sketch, "E7.0.3.47", {"center": v(-246.68, -362.92) * mm, "radius": 5.9 * mm});
            skCircle(sketch, "E7.0.3.48", {"center": v(-246.68, -388.32) * mm, "radius": 5.9 * mm});
            skCircle(sketch, "E7.0.3.49", {"center": v(-246.68, -413.72) * mm, "radius": 5.9 * mm});
            skCircle(sketch, "E7.0.3.50", {"center": v(-246.68, -439.12) * mm, "radius": 5.9 * mm});
            skCircle(sketch, "E7.0.3.51", {"center": v(-246.68, -464.52) * mm, "radius": 5.9 * mm});
            skCircle(sketch, "E7.0.3.52", {"center": v(-246.68, -489.92) * mm, "radius": 5.9 * mm});
            skCircle(sketch, "E7.0.3.53", {"center": v(-246.68, -515.32) * mm, "radius": 5.9 * mm});
            skCircle(sketch, "E7.0.3.54", {"center": v(-246.68, -540.72) * mm, "radius": 5.9 * mm});
            skCircle(sketch, "E7.0.3.55", {"center": v(-246.68, -566.12) * mm, "radius": 5.9 * mm});
            skCircle(sketch, "E7.0.3.56", {"center": v(-246.68, -591.52) * mm, "radius": 5.9 * mm});
            skCircle(sketch, "E7.0.3.57", {"center": v(-246.68, -616.92) * mm, "radius": 5.9 * mm});
            skCircle(sketch, "E7.0.3.58", {"center": v(-246.68, -642.32) * mm, "radius": 5.9 * mm});
            skCircle(sketch, "E7.0.3.59", {"center": v(-246.68, -667.72) * mm, "radius": 5.9 * mm});
            skCircle(sketch, "E7.0.3.60", {"center": v(-246.68, -693.12) * mm, "radius": 5.9 * mm});
            skCircle(sketch, "E7.0.3.61", {"center": v(-246.68, -718.52) * mm, "radius": 5.9 * mm});
            skCircle(sketch, "E7.0.3.62", {"center": v(-246.68, -743.92) * mm, "radius": 5.9 * mm});
            skCircle(sketch, "E7.0.3.63", {"center": v(-246.68, -769.32) * mm, "radius": 5.9 * mm});
            skCircle(sketch, "E7.0.3.64", {"center": v(-246.68, -794.72) * mm, "radius": 5.9 * mm});
            skCircle(sketch, "E7.0.4.25", {"center": v(-221.28, 195.88) * mm, "radius": 5.9 * mm});
            skCircle(sketch, "E7.0.4.26", {"center": v(-221.28, 170.48) * mm, "radius": 5.9 * mm});
            skCircle(sketch, "E7.0.4.27", {"center": v(-221.28, 145.08) * mm, "radius": 5.9 * mm});
            skCircle(sketch, "E7.0.4.28", {"center": v(-221.28, 119.68) * mm, "radius": 5.9 * mm});
            skCircle(sketch, "E7.0.4.29", {"center": v(-221.28, 94.28) * mm, "radius": 5.9 * mm});
            skCircle(sketch, "E7.0.4.30", {"center": v(-221.28, 68.88) * mm, "radius": 5.9 * mm});
            skCircle(sketch, "E7.0.4.31", {"center": v(-221.28, 43.48) * mm, "radius": 5.9 * mm});
            skCircle(sketch, "E7.0.4.32", {"center": v(-221.28, 18.08) * mm, "radius": 5.9 * mm});
            skCircle(sketch, "E7.0.4.33", {"center": v(-221.28, -7.32) * mm, "radius": 5.9 * mm});
            skCircle(sketch, "E7.0.4.34", {"center": v(-221.28, -32.72) * mm, "radius": 5.9 * mm});
            skCircle(sketch, "E7.0.4.35", {"center": v(-221.28, -58.12) * mm, "radius": 5.9 * mm});
            skCircle(sketch, "E7.0.4.36", {"center": v(-221.28, -83.52) * mm, "radius": 5.9 * mm});
            skCircle(sketch, "E7.0.4.37", {"center": v(-221.28, -108.92) * mm, "radius": 5.9 * mm});
            skCircle(sketch, "E7.0.4.38", {"center": v(-221.28, -134.32) * mm, "radius": 5.9 * mm});
            skCircle(sketch, "E7.0.4.39", {"center": v(-221.28, -159.72) * mm, "radius": 5.9 * mm});
            skCircle(sketch, "E7.0.4.40", {"center": v(-221.28, -185.12) * mm, "radius": 5.9 * mm});
            skCircle(sketch, "E7.0.4.41", {"center": v(-221.28, -210.52) * mm, "radius": 5.9 * mm});
            skCircle(sketch, "E7.0.4.42", {"center": v(-221.28, -235.92) * mm, "radius": 5.9 * mm});
            skCircle(sketch, "E7.0.4.43", {"center": v(-221.28, -261.32) * mm, "radius": 5.9 * mm});
            skCircle(sketch, "E7.0.4.44", {"center": v(-221.28, -286.72) * mm, "radius": 5.9 * mm});
            skCircle(sketch, "E7.0.4.45", {"center": v(-221.28, -312.12) * mm, "radius": 5.9 * mm});
            skCircle(sketch, "E7.0.4.46", {"center": v(-221.28, -337.52) * mm, "radius": 5.9 * mm});
            skCircle(sketch, "E7.0.4.47", {"center": v(-221.28, -362.92) * mm, "radius": 5.9 * mm});
            skCircle(sketch, "E7.0.4.48", {"center": v(-221.28, -388.32) * mm, "radius": 5.9 * mm});
            skCircle(sketch, "E7.0.4.49", {"center": v(-221.28, -413.72) * mm, "radius": 5.9 * mm});
            skCircle(sketch, "E7.0.4.50", {"center": v(-221.28, -439.12) * mm, "radius": 5.9 * mm});
            skCircle(sketch, "E7.0.4.51", {"center": v(-221.28, -464.52) * mm, "radius": 5.9 * mm});
            skCircle(sketch, "E7.0.4.52", {"center": v(-221.28, -489.92) * mm, "radius": 5.9 * mm});
            skCircle(sketch, "E7.0.4.53", {"center": v(-221.28, -515.32) * mm, "radius": 5.9 * mm});
            skCircle(sketch, "E7.0.4.54", {"center": v(-221.28, -540.72) * mm, "radius": 5.9 * mm});
            skCircle(sketch, "E7.0.4.55", {"center": v(-221.28, -566.12) * mm, "radius": 5.9 * mm});
            skCircle(sketch, "E7.0.4.56", {"center": v(-221.28, -591.52) * mm, "radius": 5.9 * mm});
            skCircle(sketch, "E7.0.4.57", {"center": v(-221.28, -616.92) * mm, "radius": 5.9 * mm});
            skCircle(sketch, "E7.0.4.58", {"center": v(-221.28, -642.32) * mm, "radius": 5.9 * mm});
            skCircle(sketch, "E7.0.4.59", {"center": v(-221.28, -667.72) * mm, "radius": 5.9 * mm});
            skCircle(sketch, "E7.0.4.60", {"center": v(-221.28, -693.12) * mm, "radius": 5.9 * mm});
            skCircle(sketch, "E7.0.4.61", {"center": v(-221.28, -718.52) * mm, "radius": 5.9 * mm});
            skCircle(sketch, "E7.0.4.62", {"center": v(-221.28, -743.92) * mm, "radius": 5.9 * mm});
            skCircle(sketch, "E7.0.4.63", {"center": v(-221.28, -769.32) * mm, "radius": 5.9 * mm});
            skCircle(sketch, "E7.0.4.64", {"center": v(-221.28, -794.72) * mm, "radius": 5.9 * mm});
            skCircle(sketch, "E7.0.5.25", {"center": v(-195.88, 195.88) * mm, "radius": 5.9 * mm});
            skCircle(sketch, "E7.0.5.26", {"center": v(-195.88, 170.48) * mm, "radius": 5.9 * mm});
            skCircle(sketch, "E7.0.5.27", {"center": v(-195.88, 145.08) * mm, "radius": 5.9 * mm});
            skCircle(sketch, "E7.0.5.28", {"center": v(-195.88, 119.68) * mm, "radius": 5.9 * mm});
            skCircle(sketch, "E7.0.5.29", {"center": v(-195.88, 94.28) * mm, "radius": 5.9 * mm});
            skCircle(sketch, "E7.0.5.30", {"center": v(-195.88, 68.88) * mm, "radius": 5.9 * mm});
            skCircle(sketch, "E7.0.5.31", {"center": v(-195.88, 43.48) * mm, "radius": 5.9 * mm});
            skCircle(sketch, "E7.0.5.32", {"center": v(-195.88, 18.08) * mm, "radius": 5.9 * mm});
            skCircle(sketch, "E7.0.5.33", {"center": v(-195.88, -7.32) * mm, "radius": 5.9 * mm});
            skCircle(sketch, "E7.0.5.34", {"center": v(-195.88, -32.72) * mm, "radius": 5.9 * mm});
            skCircle(sketch, "E7.0.5.35", {"center": v(-195.88, -58.12) * mm, "radius": 5.9 * mm});
            skCircle(sketch, "E7.0.5.36", {"center": v(-195.88, -83.52) * mm, "radius": 5.9 * mm});
            skCircle(sketch, "E7.0.5.37", {"center": v(-195.88, -108.92) * mm, "radius": 5.9 * mm});
            skCircle(sketch, "E7.0.5.38", {"center": v(-195.88, -134.32) * mm, "radius": 5.9 * mm});
            skCircle(sketch, "E7.0.5.39", {"center": v(-195.88, -159.72) * mm, "radius": 5.9 * mm});
            skCircle(sketch, "E7.0.5.40", {"center": v(-195.88, -185.12) * mm, "radius": 5.9 * mm});
            skCircle(sketch, "E7.0.5.41", {"center": v(-195.88, -210.52) * mm, "radius": 5.9 * mm});
            skCircle(sketch, "E7.0.5.42", {"center": v(-195.88, -235.92) * mm, "radius": 5.9 * mm});
            skCircle(sketch, "E7.0.5.43", {"center": v(-195.88, -261.32) * mm, "radius": 5.9 * mm});
            skCircle(sketch, "E7.0.5.44", {"center": v(-195.88, -286.72) * mm, "radius": 5.9 * mm});
            skCircle(sketch, "E7.0.5.45", {"center": v(-195.88, -312.12) * mm, "radius": 5.9 * mm});
            skCircle(sketch, "E7.0.5.46", {"center": v(-195.88, -337.52) * mm, "radius": 5.9 * mm});
            skCircle(sketch, "E7.0.5.47", {"center": v(-195.88, -362.92) * mm, "radius": 5.9 * mm});
            skCircle(sketch, "E7.0.5.48", {"center": v(-195.88, -388.32) * mm, "radius": 5.9 * mm});
            skCircle(sketch, "E7.0.5.49", {"center": v(-195.88, -413.72) * mm, "radius": 5.9 * mm});
            skCircle(sketch, "E7.0.5.50", {"center": v(-195.88, -439.12) * mm, "radius": 5.9 * mm});
            skCircle(sketch, "E7.0.5.51", {"center": v(-195.88, -464.52) * mm, "radius": 5.9 * mm});
            skCircle(sketch, "E7.0.5.52", {"center": v(-195.88, -489.92) * mm, "radius": 5.9 * mm});
            skCircle(sketch, "E7.0.5.53", {"center": v(-195.88, -515.32) * mm, "radius": 5.9 * mm});
            skCircle(sketch, "E7.0.5.54", {"center": v(-195.88, -540.72) * mm, "radius": 5.9 * mm});
            skCircle(sketch, "E7.0.5.55", {"center": v(-195.88, -566.12) * mm, "radius": 5.9 * mm});
            skCircle(sketch, "E7.0.5.56", {"center": v(-195.88, -591.52) * mm, "radius": 5.9 * mm});
            skCircle(sketch, "E7.0.5.57", {"center": v(-195.88, -616.92) * mm, "radius": 5.9 * mm});
            skCircle(sketch, "E7.0.5.58", {"center": v(-195.88, -642.32) * mm, "radius": 5.9 * mm});
            skCircle(sketch, "E7.0.5.59", {"center": v(-195.88, -667.72) * mm, "radius": 5.9 * mm});
            skCircle(sketch, "E7.0.5.60", {"center": v(-195.88, -693.12) * mm, "radius": 5.9 * mm});
            skCircle(sketch, "E7.0.5.61", {"center": v(-195.88, -718.52) * mm, "radius": 5.9 * mm});
            skCircle(sketch, "E7.0.5.62", {"center": v(-195.88, -743.92) * mm, "radius": 5.9 * mm});
            skCircle(sketch, "E7.0.5.63", {"center": v(-195.88, -769.32) * mm, "radius": 5.9 * mm});
            skCircle(sketch, "E7.0.5.64", {"center": v(-195.88, -794.72) * mm, "radius": 5.9 * mm});
            skCircle(sketch, "E7.0.6.25", {"center": v(-170.48, 195.88) * mm, "radius": 5.9 * mm});
            skCircle(sketch, "E7.0.6.26", {"center": v(-170.48, 170.48) * mm, "radius": 5.9 * mm});
            skCircle(sketch, "E7.0.6.27", {"center": v(-170.48, 145.08) * mm, "radius": 5.9 * mm});
            skCircle(sketch, "E7.0.6.28", {"center": v(-170.48, 119.68) * mm, "radius": 5.9 * mm});
            skCircle(sketch, "E7.0.6.29", {"center": v(-170.48, 94.28) * mm, "radius": 5.9 * mm});
            skCircle(sketch, "E7.0.6.30", {"center": v(-170.48, 68.88) * mm, "radius": 5.9 * mm});
            skCircle(sketch, "E7.0.6.31", {"center": v(-170.48, 43.48) * mm, "radius": 5.9 * mm});
            skCircle(sketch, "E7.0.6.32", {"center": v(-170.48, 18.08) * mm, "radius": 5.9 * mm});
            skCircle(sketch, "E7.0.6.33", {"center": v(-170.48, -7.32) * mm, "radius": 5.9 * mm});
            skCircle(sketch, "E7.0.6.34", {"center": v(-170.48, -32.72) * mm, "radius": 5.9 * mm});
            skCircle(sketch, "E7.0.6.35", {"center": v(-170.48, -58.12) * mm, "radius": 5.9 * mm});
            skCircle(sketch, "E7.0.6.36", {"center": v(-170.48, -83.52) * mm, "radius": 5.9 * mm});
            skCircle(sketch, "E7.0.6.37", {"center": v(-170.48, -108.92) * mm, "radius": 5.9 * mm});
            skCircle(sketch, "E7.0.6.38", {"center": v(-170.48, -134.32) * mm, "radius": 5.9 * mm});
            skCircle(sketch, "E7.0.6.39", {"center": v(-170.48, -159.72) * mm, "radius": 5.9 * mm});
            skCircle(sketch, "E7.0.6.40", {"center": v(-170.48, -185.12) * mm, "radius": 5.9 * mm});
            skCircle(sketch, "E7.0.6.41", {"center": v(-170.48, -210.52) * mm, "radius": 5.9 * mm});
            skCircle(sketch, "E7.0.6.42", {"center": v(-170.48, -235.92) * mm, "radius": 5.9 * mm});
            skCircle(sketch, "E7.0.6.43", {"center": v(-170.48, -261.32) * mm, "radius": 5.9 * mm});
            skCircle(sketch, "E7.0.6.44", {"center": v(-170.48, -286.72) * mm, "radius": 5.9 * mm});
            skCircle(sketch, "E7.0.6.45", {"center": v(-170.48, -312.12) * mm, "radius": 5.9 * mm});
            skCircle(sketch, "E7.0.6.46", {"center": v(-170.48, -337.52) * mm, "radius": 5.9 * mm});
            skCircle(sketch, "E7.0.6.47", {"center": v(-170.48, -362.92) * mm, "radius": 5.9 * mm});
            skCircle(sketch, "E7.0.6.48", {"center": v(-170.48, -388.32) * mm, "radius": 5.9 * mm});
            skCircle(sketch, "E7.0.6.49", {"center": v(-170.48, -413.72) * mm, "radius": 5.9 * mm});
            skCircle(sketch, "E7.0.6.50", {"center": v(-170.48, -439.12) * mm, "radius": 5.9 * mm});
            skCircle(sketch, "E7.0.6.51", {"center": v(-170.48, -464.52) * mm, "radius": 5.9 * mm});
            skCircle(sketch, "E7.0.6.52", {"center": v(-170.48, -489.92) * mm, "radius": 5.9 * mm});
            skCircle(sketch, "E7.0.6.53", {"center": v(-170.48, -515.32) * mm, "radius": 5.9 * mm});
            skCircle(sketch, "E7.0.6.54", {"center": v(-170.48, -540.72) * mm, "radius": 5.9 * mm});
            skCircle(sketch, "E7.0.6.55", {"center": v(-170.48, -566.12) * mm, "radius": 5.9 * mm});
            skCircle(sketch, "E7.0.6.56", {"center": v(-170.48, -591.52) * mm, "radius": 5.9 * mm});
            skCircle(sketch, "E7.0.6.57", {"center": v(-170.48, -616.92) * mm, "radius": 5.9 * mm});
            skCircle(sketch, "E7.0.6.58", {"center": v(-170.48, -642.32) * mm, "radius": 5.9 * mm});
            skCircle(sketch, "E7.0.6.59", {"center": v(-170.48, -667.72) * mm, "radius": 5.9 * mm});
            skCircle(sketch, "E7.0.6.60", {"center": v(-170.48, -693.12) * mm, "radius": 5.9 * mm});
            skCircle(sketch, "E7.0.6.61", {"center": v(-170.48, -718.52) * mm, "radius": 5.9 * mm});
            skCircle(sketch, "E7.0.6.62", {"center": v(-170.48, -743.92) * mm, "radius": 5.9 * mm});
            skCircle(sketch, "E7.0.6.63", {"center": v(-170.48, -769.32) * mm, "radius": 5.9 * mm});
            skCircle(sketch, "E7.0.6.64", {"center": v(-170.48, -794.72) * mm, "radius": 5.9 * mm});
            skCircle(sketch, "E7.0.7.25", {"center": v(-145.08, 195.88) * mm, "radius": 5.9 * mm});
            skCircle(sketch, "E7.0.7.26", {"center": v(-145.08, 170.48) * mm, "radius": 5.9 * mm});
            skCircle(sketch, "E7.0.7.27", {"center": v(-145.08, 145.08) * mm, "radius": 5.9 * mm});
            skCircle(sketch, "E7.0.7.28", {"center": v(-145.08, 119.68) * mm, "radius": 5.9 * mm});
            skCircle(sketch, "E7.0.7.29", {"center": v(-145.08, 94.28) * mm, "radius": 5.9 * mm});
            skCircle(sketch, "E7.0.7.30", {"center": v(-145.08, 68.88) * mm, "radius": 5.9 * mm});
            skCircle(sketch, "E7.0.7.31", {"center": v(-145.08, 43.48) * mm, "radius": 5.9 * mm});
            skCircle(sketch, "E7.0.7.32", {"center": v(-145.08, 18.08) * mm, "radius": 5.9 * mm});
            skCircle(sketch, "E7.0.7.33", {"center": v(-145.08, -7.32) * mm, "radius": 5.9 * mm});
            skCircle(sketch, "E7.0.7.34", {"center": v(-145.08, -32.72) * mm, "radius": 5.9 * mm});
            skCircle(sketch, "E7.0.7.35", {"center": v(-145.08, -58.12) * mm, "radius": 5.9 * mm});
            skCircle(sketch, "E7.0.7.36", {"center": v(-145.08, -83.52) * mm, "radius": 5.9 * mm});
            skCircle(sketch, "E7.0.7.37", {"center": v(-145.08, -108.92) * mm, "radius": 5.9 * mm});
            skCircle(sketch, "E7.0.7.38", {"center": v(-145.08, -134.32) * mm, "radius": 5.9 * mm});
            skCircle(sketch, "E7.0.7.39", {"center": v(-145.08, -159.72) * mm, "radius": 5.9 * mm});
            skCircle(sketch, "E7.0.7.40", {"center": v(-145.08, -185.12) * mm, "radius": 5.9 * mm});
            skCircle(sketch, "E7.0.7.41", {"center": v(-145.08, -210.52) * mm, "radius": 5.9 * mm});
            skCircle(sketch, "E7.0.7.42", {"center": v(-145.08, -235.92) * mm, "radius": 5.9 * mm});
            skCircle(sketch, "E7.0.7.43", {"center": v(-145.08, -261.32) * mm, "radius": 5.9 * mm});
            skCircle(sketch, "E7.0.7.44", {"center": v(-145.08, -286.72) * mm, "radius": 5.9 * mm});
            skCircle(sketch, "E7.0.7.45", {"center": v(-145.08, -312.12) * mm, "radius": 5.9 * mm});
            skCircle(sketch, "E7.0.7.46", {"center": v(-145.08, -337.52) * mm, "radius": 5.9 * mm});
            skCircle(sketch, "E7.0.7.47", {"center": v(-145.08, -362.92) * mm, "radius": 5.9 * mm});
            skCircle(sketch, "E7.0.7.48", {"center": v(-145.08, -388.32) * mm, "radius": 5.9 * mm});
            skCircle(sketch, "E7.0.7.49", {"center": v(-145.08, -413.72) * mm, "radius": 5.9 * mm});
            skCircle(sketch, "E7.0.7.50", {"center": v(-145.08, -439.12) * mm, "radius": 5.9 * mm});
            skCircle(sketch, "E7.0.7.51", {"center": v(-145.08, -464.52) * mm, "radius": 5.9 * mm});
            skCircle(sketch, "E7.0.7.52", {"center": v(-145.08, -489.92) * mm, "radius": 5.9 * mm});
            skCircle(sketch, "E7.0.7.53", {"center": v(-145.08, -515.32) * mm, "radius": 5.9 * mm});
            skCircle(sketch, "E7.0.7.54", {"center": v(-145.08, -540.72) * mm, "radius": 5.9 * mm});
            skCircle(sketch, "E7.0.7.55", {"center": v(-145.08, -566.12) * mm, "radius": 5.9 * mm});
            skCircle(sketch, "E7.0.7.56", {"center": v(-145.08, -591.52) * mm, "radius": 5.9 * mm});
            skCircle(sketch, "E7.0.7.57", {"center": v(-145.08, -616.92) * mm, "radius": 5.9 * mm});
            skCircle(sketch, "E7.0.7.58", {"center": v(-145.08, -642.32) * mm, "radius": 5.9 * mm});
            skCircle(sketch, "E7.0.7.59", {"center": v(-145.08, -667.72) * mm, "radius": 5.9 * mm});
            skCircle(sketch, "E7.0.7.60", {"center": v(-145.08, -693.12) * mm, "radius": 5.9 * mm});
            skCircle(sketch, "E7.0.7.61", {"center": v(-145.08, -718.52) * mm, "radius": 5.9 * mm});
            skCircle(sketch, "E7.0.7.62", {"center": v(-145.08, -743.92) * mm, "radius": 5.9 * mm});
            skCircle(sketch, "E7.0.7.63", {"center": v(-145.08, -769.32) * mm, "radius": 5.9 * mm});
            skCircle(sketch, "E7.0.7.64", {"center": v(-145.08, -794.72) * mm, "radius": 5.9 * mm});
            skCircle(sketch, "E7.0.8.25", {"center": v(-119.68, 195.88) * mm, "radius": 5.9 * mm});
            skCircle(sketch, "E7.0.8.26", {"center": v(-119.68, 170.48) * mm, "radius": 5.9 * mm});
            skCircle(sketch, "E7.0.8.27", {"center": v(-119.68, 145.08) * mm, "radius": 5.9 * mm});
            skCircle(sketch, "E7.0.8.28", {"center": v(-119.68, 119.68) * mm, "radius": 5.9 * mm});
            skCircle(sketch, "E7.0.8.29", {"center": v(-119.68, 94.28) * mm, "radius": 5.9 * mm});
            skCircle(sketch, "E7.0.8.30", {"center": v(-119.68, 68.88) * mm, "radius": 5.9 * mm});
            skCircle(sketch, "E7.0.8.31", {"center": v(-119.68, 43.48) * mm, "radius": 5.9 * mm});
            skCircle(sketch, "E7.0.8.32", {"center": v(-119.68, 18.08) * mm, "radius": 5.9 * mm});
            skCircle(sketch, "E7.0.8.33", {"center": v(-119.68, -7.32) * mm, "radius": 5.9 * mm});
            skCircle(sketch, "E7.0.8.34", {"center": v(-119.68, -32.72) * mm, "radius": 5.9 * mm});
            skCircle(sketch, "E7.0.8.35", {"center": v(-119.68, -58.12) * mm, "radius": 5.9 * mm});
            skCircle(sketch, "E7.0.8.36", {"center": v(-119.68, -83.52) * mm, "radius": 5.9 * mm});
            skCircle(sketch, "E7.0.8.37", {"center": v(-119.68, -108.92) * mm, "radius": 5.9 * mm});
            skCircle(sketch, "E7.0.8.38", {"center": v(-119.68, -134.32) * mm, "radius": 5.9 * mm});
            skCircle(sketch, "E7.0.8.39", {"center": v(-119.68, -159.72) * mm, "radius": 5.9 * mm});
            skCircle(sketch, "E7.0.8.40", {"center": v(-119.68, -185.12) * mm, "radius": 5.9 * mm});
            skCircle(sketch, "E7.0.8.41", {"center": v(-119.68, -210.52) * mm, "radius": 5.9 * mm});
            skCircle(sketch, "E7.0.8.42", {"center": v(-119.68, -235.92) * mm, "radius": 5.9 * mm});
            skCircle(sketch, "E7.0.8.43", {"center": v(-119.68, -261.32) * mm, "radius": 5.9 * mm});
            skCircle(sketch, "E7.0.8.44", {"center": v(-119.68, -286.72) * mm, "radius": 5.9 * mm});
            skCircle(sketch, "E7.0.8.45", {"center": v(-119.68, -312.12) * mm, "radius": 5.9 * mm});
            skCircle(sketch, "E7.0.8.46", {"center": v(-119.68, -337.52) * mm, "radius": 5.9 * mm});
            skCircle(sketch, "E7.0.8.47", {"center": v(-119.68, -362.92) * mm, "radius": 5.9 * mm});
            skCircle(sketch, "E7.0.8.48", {"center": v(-119.68, -388.32) * mm, "radius": 5.9 * mm});
            skCircle(sketch, "E7.0.8.49", {"center": v(-119.68, -413.72) * mm, "radius": 5.9 * mm});
            skCircle(sketch, "E7.0.8.50", {"center": v(-119.68, -439.12) * mm, "radius": 5.9 * mm});
            skCircle(sketch, "E7.0.8.51", {"center": v(-119.68, -464.52) * mm, "radius": 5.9 * mm});
            skCircle(sketch, "E7.0.8.52", {"center": v(-119.68, -489.92) * mm, "radius": 5.9 * mm});
            skCircle(sketch, "E7.0.8.53", {"center": v(-119.68, -515.32) * mm, "radius": 5.9 * mm});
            skCircle(sketch, "E7.0.8.54", {"center": v(-119.68, -540.72) * mm, "radius": 5.9 * mm});
            skCircle(sketch, "E7.0.8.55", {"center": v(-119.68, -566.12) * mm, "radius": 5.9 * mm});
            skCircle(sketch, "E7.0.8.56", {"center": v(-119.68, -591.52) * mm, "radius": 5.9 * mm});
            skCircle(sketch, "E7.0.8.57", {"center": v(-119.68, -616.92) * mm, "radius": 5.9 * mm});
            skCircle(sketch, "E7.0.8.58", {"center": v(-119.68, -642.32) * mm, "radius": 5.9 * mm});
            skCircle(sketch, "E7.0.8.59", {"center": v(-119.68, -667.72) * mm, "radius": 5.9 * mm});
            skCircle(sketch, "E7.0.8.60", {"center": v(-119.68, -693.12) * mm, "radius": 5.9 * mm});
            skCircle(sketch, "E7.0.8.61", {"center": v(-119.68, -718.52) * mm, "radius": 5.9 * mm});
            skCircle(sketch, "E7.0.8.62", {"center": v(-119.68, -743.92) * mm, "radius": 5.9 * mm});
            skCircle(sketch, "E7.0.8.63", {"center": v(-119.68, -769.32) * mm, "radius": 5.9 * mm});
            skCircle(sketch, "E7.0.8.64", {"center": v(-119.68, -794.72) * mm, "radius": 5.9 * mm});
            skCircle(sketch, "E7.0.9.25", {"center": v(-94.28, 195.88) * mm, "radius": 5.9 * mm});
            skCircle(sketch, "E7.0.9.26", {"center": v(-94.28, 170.48) * mm, "radius": 5.9 * mm});
            skCircle(sketch, "E7.0.9.27", {"center": v(-94.28, 145.08) * mm, "radius": 5.9 * mm});
            skCircle(sketch, "E7.0.9.28", {"center": v(-94.28, 119.68) * mm, "radius": 5.9 * mm});
            skCircle(sketch, "E7.0.9.29", {"center": v(-94.28, 94.28) * mm, "radius": 5.9 * mm});
            skCircle(sketch, "E7.0.9.30", {"center": v(-94.28, 68.88) * mm, "radius": 5.9 * mm});
            skCircle(sketch, "E7.0.9.31", {"center": v(-94.28, 43.48) * mm, "radius": 5.9 * mm});
            skCircle(sketch, "E7.0.9.32", {"center": v(-94.28, 18.08) * mm, "radius": 5.9 * mm});
            skCircle(sketch, "E7.0.9.33", {"center": v(-94.28, -7.32) * mm, "radius": 5.9 * mm});
            skCircle(sketch, "E7.0.9.34", {"center": v(-94.28, -32.72) * mm, "radius": 5.9 * mm});
            skCircle(sketch, "E7.0.9.35", {"center": v(-94.28, -58.12) * mm, "radius": 5.9 * mm});
            skCircle(sketch, "E7.0.9.36", {"center": v(-94.28, -83.52) * mm, "radius": 5.9 * mm});
            skCircle(sketch, "E7.0.9.37", {"center": v(-94.28, -108.92) * mm, "radius": 5.9 * mm});
            skCircle(sketch, "E7.0.9.38", {"center": v(-94.28, -134.32) * mm, "radius": 5.9 * mm});
            skCircle(sketch, "E7.0.9.39", {"center": v(-94.28, -159.72) * mm, "radius": 5.9 * mm});
            skCircle(sketch, "E7.0.9.40", {"center": v(-94.28, -185.12) * mm, "radius": 5.9 * mm});
            skCircle(sketch, "E7.0.9.41", {"center": v(-94.28, -210.52) * mm, "radius": 5.9 * mm});
            skCircle(sketch, "E7.0.9.42", {"center": v(-94.28, -235.92) * mm, "radius": 5.9 * mm});
            skCircle(sketch, "E7.0.9.43", {"center": v(-94.28, -261.32) * mm, "radius": 5.9 * mm});
            skCircle(sketch, "E7.0.9.44", {"center": v(-94.28, -286.72) * mm, "radius": 5.9 * mm});
            skCircle(sketch, "E7.0.9.45", {"center": v(-94.28, -312.12) * mm, "radius": 5.9 * mm});
            skCircle(sketch, "E7.0.9.46", {"center": v(-94.28, -337.52) * mm, "radius": 5.9 * mm});
            skCircle(sketch, "E7.0.9.47", {"center": v(-94.28, -362.92) * mm, "radius": 5.9 * mm});
            skCircle(sketch, "E7.0.9.48", {"center": v(-94.28, -388.32) * mm, "radius": 5.9 * mm});
            skCircle(sketch, "E7.0.9.49", {"center": v(-94.28, -413.72) * mm, "radius": 5.9 * mm});
            skCircle(sketch, "E7.0.9.50", {"center": v(-94.28, -439.12) * mm, "radius": 5.9 * mm});
            skCircle(sketch, "E7.0.9.51", {"center": v(-94.28, -464.52) * mm, "radius": 5.9 * mm});
            skCircle(sketch, "E7.0.9.52", {"center": v(-94.28, -489.92) * mm, "radius": 5.9 * mm});
            skCircle(sketch, "E7.0.9.53", {"center": v(-94.28, -515.32) * mm, "radius": 5.9 * mm});
            skCircle(sketch, "E7.0.9.54", {"center": v(-94.28, -540.72) * mm, "radius": 5.9 * mm});
            skCircle(sketch, "E7.0.9.55", {"center": v(-94.28, -566.12) * mm, "radius": 5.9 * mm});
            skCircle(sketch, "E7.0.9.56", {"center": v(-94.28, -591.52) * mm, "radius": 5.9 * mm});
            skCircle(sketch, "E7.0.9.57", {"center": v(-94.28, -616.92) * mm, "radius": 5.9 * mm});
            skCircle(sketch, "E7.0.9.58", {"center": v(-94.28, -642.32) * mm, "radius": 5.9 * mm});
            skCircle(sketch, "E7.0.9.59", {"center": v(-94.28, -667.72) * mm, "radius": 5.9 * mm});
            skCircle(sketch, "E7.0.9.60", {"center": v(-94.28, -693.12) * mm, "radius": 5.9 * mm});
            skCircle(sketch, "E7.0.9.61", {"center": v(-94.28, -718.52) * mm, "radius": 5.9 * mm});
            skCircle(sketch, "E7.0.9.62", {"center": v(-94.28, -743.92) * mm, "radius": 5.9 * mm});
            skCircle(sketch, "E7.0.9.63", {"center": v(-94.28, -769.32) * mm, "radius": 5.9 * mm});
            skCircle(sketch, "E7.0.9.64", {"center": v(-94.28, -794.72) * mm, "radius": 5.9 * mm});
            skCircle(sketch, "E7.0.10.25", {"center": v(-68.88, 195.88) * mm, "radius": 5.9 * mm});
            skCircle(sketch, "E7.0.10.26", {"center": v(-68.88, 170.48) * mm, "radius": 5.9 * mm});
            skCircle(sketch, "E7.0.10.27", {"center": v(-68.88, 145.08) * mm, "radius": 5.9 * mm});
            skCircle(sketch, "E7.0.10.28", {"center": v(-68.88, 119.68) * mm, "radius": 5.9 * mm});
            skCircle(sketch, "E7.0.10.29", {"center": v(-68.88, 94.28) * mm, "radius": 5.9 * mm});
            skCircle(sketch, "E7.0.10.30", {"center": v(-68.88, 68.88) * mm, "radius": 5.9 * mm});
            skCircle(sketch, "E7.0.10.31", {"center": v(-68.88, 43.48) * mm, "radius": 5.9 * mm});
            skCircle(sketch, "E7.0.10.32", {"center": v(-68.88, 18.08) * mm, "radius": 5.9 * mm});
            skCircle(sketch, "E7.0.10.33", {"center": v(-68.88, -7.32) * mm, "radius": 5.9 * mm});
            skCircle(sketch, "E7.0.10.34", {"center": v(-68.88, -32.72) * mm, "radius": 5.9 * mm});
            skCircle(sketch, "E7.0.10.35", {"center": v(-68.88, -58.12) * mm, "radius": 5.9 * mm});
            skCircle(sketch, "E7.0.10.36", {"center": v(-68.88, -83.52) * mm, "radius": 5.9 * mm});
            skCircle(sketch, "E7.0.10.37", {"center": v(-68.88, -108.92) * mm, "radius": 5.9 * mm});
            skCircle(sketch, "E7.0.10.38", {"center": v(-68.88, -134.32) * mm, "radius": 5.9 * mm});
            skCircle(sketch, "E7.0.10.39", {"center": v(-68.88, -159.72) * mm, "radius": 5.9 * mm});
            skCircle(sketch, "E7.0.10.40", {"center": v(-68.88, -185.12) * mm, "radius": 5.9 * mm});
            skCircle(sketch, "E7.0.10.41", {"center": v(-68.88, -210.52) * mm, "radius": 5.9 * mm});
            skCircle(sketch, "E7.0.10.42", {"center": v(-68.88, -235.92) * mm, "radius": 5.9 * mm});
            skCircle(sketch, "E7.0.10.43", {"center": v(-68.88, -261.32) * mm, "radius": 5.9 * mm});
            skCircle(sketch, "E7.0.10.44", {"center": v(-68.88, -286.72) * mm, "radius": 5.9 * mm});
            skCircle(sketch, "E7.0.10.45", {"center": v(-68.88, -312.12) * mm, "radius": 5.9 * mm});
            skCircle(sketch, "E7.0.10.46", {"center": v(-68.88, -337.52) * mm, "radius": 5.9 * mm});
            skCircle(sketch, "E7.0.10.47", {"center": v(-68.88, -362.92) * mm, "radius": 5.9 * mm});
            skCircle(sketch, "E7.0.10.48", {"center": v(-68.88, -388.32) * mm, "radius": 5.9 * mm});
            skCircle(sketch, "E7.0.10.49", {"center": v(-68.88, -413.72) * mm, "radius": 5.9 * mm});
            skCircle(sketch, "E7.0.10.50", {"center": v(-68.88, -439.12) * mm, "radius": 5.9 * mm});
            skCircle(sketch, "E7.0.10.51", {"center": v(-68.88, -464.52) * mm, "radius": 5.9 * mm});
            skCircle(sketch, "E7.0.10.52", {"center": v(-68.88, -489.92) * mm, "radius": 5.9 * mm});
            skCircle(sketch, "E7.0.10.53", {"center": v(-68.88, -515.32) * mm, "radius": 5.9 * mm});
            skCircle(sketch, "E7.0.10.54", {"center": v(-68.88, -540.72) * mm, "radius": 5.9 * mm});
            skCircle(sketch, "E7.0.10.55", {"center": v(-68.88, -566.12) * mm, "radius": 5.9 * mm});
            skCircle(sketch, "E7.0.10.56", {"center": v(-68.88, -591.52) * mm, "radius": 5.9 * mm});
            skCircle(sketch, "E7.0.10.57", {"center": v(-68.88, -616.92) * mm, "radius": 5.9 * mm});
            skCircle(sketch, "E7.0.10.58", {"center": v(-68.88, -642.32) * mm, "radius": 5.9 * mm});
            skCircle(sketch, "E7.0.10.59", {"center": v(-68.88, -667.72) * mm, "radius": 5.9 * mm});
            skCircle(sketch, "E7.0.10.60", {"center": v(-68.88, -693.12) * mm, "radius": 5.9 * mm});
            skCircle(sketch, "E7.0.10.61", {"center": v(-68.88, -718.52) * mm, "radius": 5.9 * mm});
            skCircle(sketch, "E7.0.10.62", {"center": v(-68.88, -743.92) * mm, "radius": 5.9 * mm});
            skCircle(sketch, "E7.0.10.63", {"center": v(-68.88, -769.32) * mm, "radius": 5.9 * mm});
            skCircle(sketch, "E7.0.10.64", {"center": v(-68.88, -794.72) * mm, "radius": 5.9 * mm});
            skCircle(sketch, "E7.0.11.25", {"center": v(-43.48, 195.88) * mm, "radius": 5.9 * mm});
            skCircle(sketch, "E7.0.11.26", {"center": v(-43.48, 170.48) * mm, "radius": 5.9 * mm});
            skCircle(sketch, "E7.0.11.27", {"center": v(-43.48, 145.08) * mm, "radius": 5.9 * mm});
            skCircle(sketch, "E7.0.11.28", {"center": v(-43.48, 119.68) * mm, "radius": 5.9 * mm});
            skCircle(sketch, "E7.0.11.29", {"center": v(-43.48, 94.28) * mm, "radius": 5.9 * mm});
            skCircle(sketch, "E7.0.11.30", {"center": v(-43.48, 68.88) * mm, "radius": 5.9 * mm});
            skCircle(sketch, "E7.0.11.31", {"center": v(-43.48, 43.48) * mm, "radius": 5.9 * mm});
            skCircle(sketch, "E7.0.11.32", {"center": v(-43.48, 18.08) * mm, "radius": 5.9 * mm});
            skCircle(sketch, "E7.0.11.33", {"center": v(-43.48, -7.32) * mm, "radius": 5.9 * mm});
            skCircle(sketch, "E7.0.11.34", {"center": v(-43.48, -32.72) * mm, "radius": 5.9 * mm});
            skCircle(sketch, "E7.0.11.35", {"center": v(-43.48, -58.12) * mm, "radius": 5.9 * mm});
            skCircle(sketch, "E7.0.11.36", {"center": v(-43.48, -83.52) * mm, "radius": 5.9 * mm});
            skCircle(sketch, "E7.0.11.37", {"center": v(-43.48, -108.92) * mm, "radius": 5.9 * mm});
            skCircle(sketch, "E7.0.11.38", {"center": v(-43.48, -134.32) * mm, "radius": 5.9 * mm});
            skCircle(sketch, "E7.0.11.39", {"center": v(-43.48, -159.72) * mm, "radius": 5.9 * mm});
            skCircle(sketch, "E7.0.11.40", {"center": v(-43.48, -185.12) * mm, "radius": 5.9 * mm});
            skCircle(sketch, "E7.0.11.41", {"center": v(-43.48, -210.52) * mm, "radius": 5.9 * mm});
            skCircle(sketch, "E7.0.11.42", {"center": v(-43.48, -235.92) * mm, "radius": 5.9 * mm});
            skCircle(sketch, "E7.0.11.43", {"center": v(-43.48, -261.32) * mm, "radius": 5.9 * mm});
            skCircle(sketch, "E7.0.11.44", {"center": v(-43.48, -286.72) * mm, "radius": 5.9 * mm});
            skCircle(sketch, "E7.0.11.45", {"center": v(-43.48, -312.12) * mm, "radius": 5.9 * mm});
            skCircle(sketch, "E7.0.11.46", {"center": v(-43.48, -337.52) * mm, "radius": 5.9 * mm});
            skCircle(sketch, "E7.0.11.47", {"center": v(-43.48, -362.92) * mm, "radius": 5.9 * mm});
            skCircle(sketch, "E7.0.11.48", {"center": v(-43.48, -388.32) * mm, "radius": 5.9 * mm});
            skCircle(sketch, "E7.0.11.49", {"center": v(-43.48, -413.72) * mm, "radius": 5.9 * mm});
            skCircle(sketch, "E7.0.11.50", {"center": v(-43.48, -439.12) * mm, "radius": 5.9 * mm});
            skCircle(sketch, "E7.0.11.51", {"center": v(-43.48, -464.52) * mm, "radius": 5.9 * mm});
            skCircle(sketch, "E7.0.11.52", {"center": v(-43.48, -489.92) * mm, "radius": 5.9 * mm});
            skCircle(sketch, "E7.0.11.53", {"center": v(-43.48, -515.32) * mm, "radius": 5.9 * mm});
            skCircle(sketch, "E7.0.11.54", {"center": v(-43.48, -540.72) * mm, "radius": 5.9 * mm});
            skCircle(sketch, "E7.0.11.55", {"center": v(-43.48, -566.12) * mm, "radius": 5.9 * mm});
            skCircle(sketch, "E7.0.11.56", {"center": v(-43.48, -591.52) * mm, "radius": 5.9 * mm});
            skCircle(sketch, "E7.0.11.57", {"center": v(-43.48, -616.92) * mm, "radius": 5.9 * mm});
            skCircle(sketch, "E7.0.11.58", {"center": v(-43.48, -642.32) * mm, "radius": 5.9 * mm});
            skCircle(sketch, "E7.0.11.59", {"center": v(-43.48, -667.72) * mm, "radius": 5.9 * mm});
            skCircle(sketch, "E7.0.11.60", {"center": v(-43.48, -693.12) * mm, "radius": 5.9 * mm});
            skCircle(sketch, "E7.0.11.61", {"center": v(-43.48, -718.52) * mm, "radius": 5.9 * mm});
            skCircle(sketch, "E7.0.11.62", {"center": v(-43.48, -743.92) * mm, "radius": 5.9 * mm});
            skCircle(sketch, "E7.0.11.63", {"center": v(-43.48, -769.32) * mm, "radius": 5.9 * mm});
            skCircle(sketch, "E7.0.11.64", {"center": v(-43.48, -794.72) * mm, "radius": 5.9 * mm});
            skCircle(sketch, "E7.0.12.25", {"center": v(-18.08, 195.88) * mm, "radius": 5.9 * mm});
            skCircle(sketch, "E7.0.12.26", {"center": v(-18.08, 170.48) * mm, "radius": 5.9 * mm});
            skCircle(sketch, "E7.0.12.27", {"center": v(-18.08, 145.08) * mm, "radius": 5.9 * mm});
            skCircle(sketch, "E7.0.12.28", {"center": v(-18.08, 119.68) * mm, "radius": 5.9 * mm});
            skCircle(sketch, "E7.0.12.29", {"center": v(-18.08, 94.28) * mm, "radius": 5.9 * mm});
            skCircle(sketch, "E7.0.12.30", {"center": v(-18.08, 68.88) * mm, "radius": 5.9 * mm});
            skCircle(sketch, "E7.0.12.31", {"center": v(-18.08, 43.48) * mm, "radius": 5.9 * mm});
            skCircle(sketch, "E7.0.12.32", {"center": v(-18.08, 18.08) * mm, "radius": 5.9 * mm});
            skCircle(sketch, "E7.0.12.33", {"center": v(-18.08, -7.32) * mm, "radius": 5.9 * mm});
            skCircle(sketch, "E7.0.12.34", {"center": v(-18.08, -32.72) * mm, "radius": 5.9 * mm});
            skCircle(sketch, "E7.0.12.35", {"center": v(-18.08, -58.12) * mm, "radius": 5.9 * mm});
            skCircle(sketch, "E7.0.12.36", {"center": v(-18.08, -83.52) * mm, "radius": 5.9 * mm});
            skCircle(sketch, "E7.0.12.37", {"center": v(-18.08, -108.92) * mm, "radius": 5.9 * mm});
            skCircle(sketch, "E7.0.12.38", {"center": v(-18.08, -134.32) * mm, "radius": 5.9 * mm});
            skCircle(sketch, "E7.0.12.39", {"center": v(-18.08, -159.72) * mm, "radius": 5.9 * mm});
            skCircle(sketch, "E7.0.12.40", {"center": v(-18.08, -185.12) * mm, "radius": 5.9 * mm});
            skCircle(sketch, "E7.0.12.41", {"center": v(-18.08, -210.52) * mm, "radius": 5.9 * mm});
            skCircle(sketch, "E7.0.12.42", {"center": v(-18.08, -235.92) * mm, "radius": 5.9 * mm});
            skCircle(sketch, "E7.0.12.43", {"center": v(-18.08, -261.32) * mm, "radius": 5.9 * mm});
            skCircle(sketch, "E7.0.12.44", {"center": v(-18.08, -286.72) * mm, "radius": 5.9 * mm});
            skCircle(sketch, "E7.0.12.45", {"center": v(-18.08, -312.12) * mm, "radius": 5.9 * mm});
            skCircle(sketch, "E7.0.12.46", {"center": v(-18.08, -337.52) * mm, "radius": 5.9 * mm});
            skCircle(sketch, "E7.0.12.47", {"center": v(-18.08, -362.92) * mm, "radius": 5.9 * mm});
            skCircle(sketch, "E7.0.12.48", {"center": v(-18.08, -388.32) * mm, "radius": 5.9 * mm});
            skCircle(sketch, "E7.0.12.49", {"center": v(-18.08, -413.72) * mm, "radius": 5.9 * mm});
            skCircle(sketch, "E7.0.12.50", {"center": v(-18.08, -439.12) * mm, "radius": 5.9 * mm});
            skCircle(sketch, "E7.0.12.51", {"center": v(-18.08, -464.52) * mm, "radius": 5.9 * mm});
            skCircle(sketch, "E7.0.12.52", {"center": v(-18.08, -489.92) * mm, "radius": 5.9 * mm});
            skCircle(sketch, "E7.0.12.53", {"center": v(-18.08, -515.32) * mm, "radius": 5.9 * mm});
            skCircle(sketch, "E7.0.12.54", {"center": v(-18.08, -540.72) * mm, "radius": 5.9 * mm});
            skCircle(sketch, "E7.0.12.55", {"center": v(-18.08, -566.12) * mm, "radius": 5.9 * mm});
            skCircle(sketch, "E7.0.12.56", {"center": v(-18.08, -591.52) * mm, "radius": 5.9 * mm});
            skCircle(sketch, "E7.0.12.57", {"center": v(-18.08, -616.92) * mm, "radius": 5.9 * mm});
            skCircle(sketch, "E7.0.12.58", {"center": v(-18.08, -642.32) * mm, "radius": 5.9 * mm});
            skCircle(sketch, "E7.0.12.59", {"center": v(-18.08, -667.72) * mm, "radius": 5.9 * mm});
            skCircle(sketch, "E7.0.12.60", {"center": v(-18.08, -693.12) * mm, "radius": 5.9 * mm});
            skCircle(sketch, "E7.0.12.61", {"center": v(-18.08, -718.52) * mm, "radius": 5.9 * mm});
            skCircle(sketch, "E7.0.12.62", {"center": v(-18.08, -743.92) * mm, "radius": 5.9 * mm});
            skCircle(sketch, "E7.0.12.63", {"center": v(-18.08, -769.32) * mm, "radius": 5.9 * mm});
            skCircle(sketch, "E7.0.12.64", {"center": v(-18.08, -794.72) * mm, "radius": 5.9 * mm});
            skCircle(sketch, "E7.0.13.25", {"center": v(7.32, 195.88) * mm, "radius": 5.9 * mm});
            skCircle(sketch, "E7.0.13.26", {"center": v(7.32, 170.48) * mm, "radius": 5.9 * mm});
            skCircle(sketch, "E7.0.13.27", {"center": v(7.32, 145.08) * mm, "radius": 5.9 * mm});
            skCircle(sketch, "E7.0.13.28", {"center": v(7.32, 119.68) * mm, "radius": 5.9 * mm});
            skCircle(sketch, "E7.0.13.29", {"center": v(7.32, 94.28) * mm, "radius": 5.9 * mm});
            skCircle(sketch, "E7.0.13.30", {"center": v(7.32, 68.88) * mm, "radius": 5.9 * mm});
            skCircle(sketch, "E7.0.13.31", {"center": v(7.32, 43.48) * mm, "radius": 5.9 * mm});
            skCircle(sketch, "E7.0.13.32", {"center": v(7.32, 18.08) * mm, "radius": 5.9 * mm});
            skCircle(sketch, "E7.0.13.33", {"center": v(7.32, -7.32) * mm, "radius": 5.9 * mm});
            skCircle(sketch, "E7.0.13.34", {"center": v(7.32, -32.72) * mm, "radius": 5.9 * mm});
            skCircle(sketch, "E7.0.13.35", {"center": v(7.32, -58.12) * mm, "radius": 5.9 * mm});
            skCircle(sketch, "E7.0.13.36", {"center": v(7.32, -83.52) * mm, "radius": 5.9 * mm});
            skCircle(sketch, "E7.0.13.37", {"center": v(7.32, -108.92) * mm, "radius": 5.9 * mm});
            skCircle(sketch, "E7.0.13.38", {"center": v(7.32, -134.32) * mm, "radius": 5.9 * mm});
            skCircle(sketch, "E7.0.13.39", {"center": v(7.32, -159.72) * mm, "radius": 5.9 * mm});
            skCircle(sketch, "E7.0.13.40", {"center": v(7.32, -185.12) * mm, "radius": 5.9 * mm});
            skCircle(sketch, "E7.0.13.41", {"center": v(7.32, -210.52) * mm, "radius": 5.9 * mm});
            skCircle(sketch, "E7.0.13.42", {"center": v(7.32, -235.92) * mm, "radius": 5.9 * mm});
            skCircle(sketch, "E7.0.13.43", {"center": v(7.32, -261.32) * mm, "radius": 5.9 * mm});
            skCircle(sketch, "E7.0.13.44", {"center": v(7.32, -286.72) * mm, "radius": 5.9 * mm});
            skCircle(sketch, "E7.0.13.45", {"center": v(7.32, -312.12) * mm, "radius": 5.9 * mm});
            skCircle(sketch, "E7.0.13.46", {"center": v(7.32, -337.52) * mm, "radius": 5.9 * mm});
            skCircle(sketch, "E7.0.13.47", {"center": v(7.32, -362.92) * mm, "radius": 5.9 * mm});
            skCircle(sketch, "E7.0.13.48", {"center": v(7.32, -388.32) * mm, "radius": 5.9 * mm});
            skCircle(sketch, "E7.0.13.49", {"center": v(7.32, -413.72) * mm, "radius": 5.9 * mm});
            skCircle(sketch, "E7.0.13.50", {"center": v(7.32, -439.12) * mm, "radius": 5.9 * mm});
            skCircle(sketch, "E7.0.13.51", {"center": v(7.32, -464.52) * mm, "radius": 5.9 * mm});
            skCircle(sketch, "E7.0.13.52", {"center": v(7.32, -489.92) * mm, "radius": 5.9 * mm});
            skCircle(sketch, "E7.0.13.53", {"center": v(7.32, -515.32) * mm, "radius": 5.9 * mm});
            skCircle(sketch, "E7.0.13.54", {"center": v(7.32, -540.72) * mm, "radius": 5.9 * mm});
            skCircle(sketch, "E7.0.13.55", {"center": v(7.32, -566.12) * mm, "radius": 5.9 * mm});
            skCircle(sketch, "E7.0.13.56", {"center": v(7.32, -591.52) * mm, "radius": 5.9 * mm});
            skCircle(sketch, "E7.0.13.57", {"center": v(7.32, -616.92) * mm, "radius": 5.9 * mm});
            skCircle(sketch, "E7.0.13.58", {"center": v(7.32, -642.32) * mm, "radius": 5.9 * mm});
            skCircle(sketch, "E7.0.13.59", {"center": v(7.32, -667.72) * mm, "radius": 5.9 * mm});
            skCircle(sketch, "E7.0.13.60", {"center": v(7.32, -693.12) * mm, "radius": 5.9 * mm});
            skCircle(sketch, "E7.0.13.61", {"center": v(7.32, -718.52) * mm, "radius": 5.9 * mm});
            skCircle(sketch, "E7.0.13.62", {"center": v(7.32, -743.92) * mm, "radius": 5.9 * mm});
            skCircle(sketch, "E7.0.13.63", {"center": v(7.32, -769.32) * mm, "radius": 5.9 * mm});
            skCircle(sketch, "E7.0.13.64", {"center": v(7.32, -794.72) * mm, "radius": 5.9 * mm});
            skCircle(sketch, "E7.0.14.25", {"center": v(32.72, 195.88) * mm, "radius": 5.9 * mm});
            skCircle(sketch, "E7.0.14.26", {"center": v(32.72, 170.48) * mm, "radius": 5.9 * mm});
            skCircle(sketch, "E7.0.14.27", {"center": v(32.72, 145.08) * mm, "radius": 5.9 * mm});
            skCircle(sketch, "E7.0.14.28", {"center": v(32.72, 119.68) * mm, "radius": 5.9 * mm});
            skCircle(sketch, "E7.0.14.29", {"center": v(32.72, 94.28) * mm, "radius": 5.9 * mm});
            skCircle(sketch, "E7.0.14.30", {"center": v(32.72, 68.88) * mm, "radius": 5.9 * mm});
            skCircle(sketch, "E7.0.14.31", {"center": v(32.72, 43.48) * mm, "radius": 5.9 * mm});
            skCircle(sketch, "E7.0.14.32", {"center": v(32.72, 18.08) * mm, "radius": 5.9 * mm});
            skCircle(sketch, "E7.0.14.33", {"center": v(32.72, -7.32) * mm, "radius": 5.9 * mm});
            skCircle(sketch, "E7.0.14.34", {"center": v(32.72, -32.72) * mm, "radius": 5.9 * mm});
            skCircle(sketch, "E7.0.14.35", {"center": v(32.72, -58.12) * mm, "radius": 5.9 * mm});
            skCircle(sketch, "E7.0.14.36", {"center": v(32.72, -83.52) * mm, "radius": 5.9 * mm});
            skCircle(sketch, "E7.0.14.37", {"center": v(32.72, -108.92) * mm, "radius": 5.9 * mm});
            skCircle(sketch, "E7.0.14.38", {"center": v(32.72, -134.32) * mm, "radius": 5.9 * mm});
            skCircle(sketch, "E7.0.14.39", {"center": v(32.72, -159.72) * mm, "radius": 5.9 * mm});
            skCircle(sketch, "E7.0.14.40", {"center": v(32.72, -185.12) * mm, "radius": 5.9 * mm});
            skCircle(sketch, "E7.0.14.41", {"center": v(32.72, -210.52) * mm, "radius": 5.9 * mm});
            skCircle(sketch, "E7.0.14.42", {"center": v(32.72, -235.92) * mm, "radius": 5.9 * mm});
            skCircle(sketch, "E7.0.14.43", {"center": v(32.72, -261.32) * mm, "radius": 5.9 * mm});
            skCircle(sketch, "E7.0.14.44", {"center": v(32.72, -286.72) * mm, "radius": 5.9 * mm});
            skCircle(sketch, "E7.0.14.45", {"center": v(32.72, -312.12) * mm, "radius": 5.9 * mm});
            skCircle(sketch, "E7.0.14.46", {"center": v(32.72, -337.52) * mm, "radius": 5.9 * mm});
            skCircle(sketch, "E7.0.14.47", {"center": v(32.72, -362.92) * mm, "radius": 5.9 * mm});
            skCircle(sketch, "E7.0.14.48", {"center": v(32.72, -388.32) * mm, "radius": 5.9 * mm});
            skCircle(sketch, "E7.0.14.49", {"center": v(32.72, -413.72) * mm, "radius": 5.9 * mm});
            skCircle(sketch, "E7.0.14.50", {"center": v(32.72, -439.12) * mm, "radius": 5.9 * mm});
            skCircle(sketch, "E7.0.14.51", {"center": v(32.72, -464.52) * mm, "radius": 5.9 * mm});
            skCircle(sketch, "E7.0.14.52", {"center": v(32.72, -489.92) * mm, "radius": 5.9 * mm});
            skCircle(sketch, "E7.0.14.53", {"center": v(32.72, -515.32) * mm, "radius": 5.9 * mm});
            skCircle(sketch, "E7.0.14.54", {"center": v(32.72, -540.72) * mm, "radius": 5.9 * mm});
            skCircle(sketch, "E7.0.14.55", {"center": v(32.72, -566.12) * mm, "radius": 5.9 * mm});
            skCircle(sketch, "E7.0.14.56", {"center": v(32.72, -591.52) * mm, "radius": 5.9 * mm});
            skCircle(sketch, "E7.0.14.57", {"center": v(32.72, -616.92) * mm, "radius": 5.9 * mm});
            skCircle(sketch, "E7.0.14.58", {"center": v(32.72, -642.32) * mm, "radius": 5.9 * mm});
            skCircle(sketch, "E7.0.14.59", {"center": v(32.72, -667.72) * mm, "radius": 5.9 * mm});
            skCircle(sketch, "E7.0.14.60", {"center": v(32.72, -693.12) * mm, "radius": 5.9 * mm});
            skCircle(sketch, "E7.0.14.61", {"center": v(32.72, -718.52) * mm, "radius": 5.9 * mm});
            skCircle(sketch, "E7.0.14.62", {"center": v(32.72, -743.92) * mm, "radius": 5.9 * mm});
            skCircle(sketch, "E7.0.14.63", {"center": v(32.72, -769.32) * mm, "radius": 5.9 * mm});
            skCircle(sketch, "E7.0.14.64", {"center": v(32.72, -794.72) * mm, "radius": 5.9 * mm});
            skCircle(sketch, "E7.0.15.25", {"center": v(58.12, 195.88) * mm, "radius": 5.9 * mm});
            skCircle(sketch, "E7.0.15.26", {"center": v(58.12, 170.48) * mm, "radius": 5.9 * mm});
            skCircle(sketch, "E7.0.15.27", {"center": v(58.12, 145.08) * mm, "radius": 5.9 * mm});
            skCircle(sketch, "E7.0.15.28", {"center": v(58.12, 119.68) * mm, "radius": 5.9 * mm});
            skCircle(sketch, "E7.0.15.29", {"center": v(58.12, 94.28) * mm, "radius": 5.9 * mm});
            skCircle(sketch, "E7.0.15.30", {"center": v(58.12, 68.88) * mm, "radius": 5.9 * mm});
            skCircle(sketch, "E7.0.15.31", {"center": v(58.12, 43.48) * mm, "radius": 5.9 * mm});
            skCircle(sketch, "E7.0.15.32", {"center": v(58.12, 18.08) * mm, "radius": 5.9 * mm});
            skCircle(sketch, "E7.0.15.33", {"center": v(58.12, -7.32) * mm, "radius": 5.9 * mm});
            skCircle(sketch, "E7.0.15.34", {"center": v(58.12, -32.72) * mm, "radius": 5.9 * mm});
            skCircle(sketch, "E7.0.15.35", {"center": v(58.12, -58.12) * mm, "radius": 5.9 * mm});
            skCircle(sketch, "E7.0.15.36", {"center": v(58.12, -83.52) * mm, "radius": 5.9 * mm});
            skCircle(sketch, "E7.0.15.37", {"center": v(58.12, -108.92) * mm, "radius": 5.9 * mm});
            skCircle(sketch, "E7.0.15.38", {"center": v(58.12, -134.32) * mm, "radius": 5.9 * mm});
            skCircle(sketch, "E7.0.15.39", {"center": v(58.12, -159.72) * mm, "radius": 5.9 * mm});
            skCircle(sketch, "E7.0.15.40", {"center": v(58.12, -185.12) * mm, "radius": 5.9 * mm});
            skCircle(sketch, "E7.0.15.41", {"center": v(58.12, -210.52) * mm, "radius": 5.9 * mm});
            skCircle(sketch, "E7.0.15.42", {"center": v(58.12, -235.92) * mm, "radius": 5.9 * mm});
            skCircle(sketch, "E7.0.15.43", {"center": v(58.12, -261.32) * mm, "radius": 5.9 * mm});
            skCircle(sketch, "E7.0.15.44", {"center": v(58.12, -286.72) * mm, "radius": 5.9 * mm});
            skCircle(sketch, "E7.0.15.45", {"center": v(58.12, -312.12) * mm, "radius": 5.9 * mm});
            skCircle(sketch, "E7.0.15.46", {"center": v(58.12, -337.52) * mm, "radius": 5.9 * mm});
            skCircle(sketch, "E7.0.15.47", {"center": v(58.12, -362.92) * mm, "radius": 5.9 * mm});
            skCircle(sketch, "E7.0.15.48", {"center": v(58.12, -388.32) * mm, "radius": 5.9 * mm});
            skCircle(sketch, "E7.0.15.49", {"center": v(58.12, -413.72) * mm, "radius": 5.9 * mm});
            skCircle(sketch, "E7.0.15.50", {"center": v(58.12, -439.12) * mm, "radius": 5.9 * mm});
            skCircle(sketch, "E7.0.15.51", {"center": v(58.12, -464.52) * mm, "radius": 5.9 * mm});
            skCircle(sketch, "E7.0.15.52", {"center": v(58.12, -489.92) * mm, "radius": 5.9 * mm});
            skCircle(sketch, "E7.0.15.53", {"center": v(58.12, -515.32) * mm, "radius": 5.9 * mm});
            skCircle(sketch, "E7.0.15.54", {"center": v(58.12, -540.72) * mm, "radius": 5.9 * mm});
            skCircle(sketch, "E7.0.15.55", {"center": v(58.12, -566.12) * mm, "radius": 5.9 * mm});
            skCircle(sketch, "E7.0.15.56", {"center": v(58.12, -591.52) * mm, "radius": 5.9 * mm});
            skCircle(sketch, "E7.0.15.57", {"center": v(58.12, -616.92) * mm, "radius": 5.9 * mm});
            skCircle(sketch, "E7.0.15.58", {"center": v(58.12, -642.32) * mm, "radius": 5.9 * mm});
            skCircle(sketch, "E7.0.15.59", {"center": v(58.12, -667.72) * mm, "radius": 5.9 * mm});
            skCircle(sketch, "E7.0.15.60", {"center": v(58.12, -693.12) * mm, "radius": 5.9 * mm});
            skCircle(sketch, "E7.0.15.61", {"center": v(58.12, -718.52) * mm, "radius": 5.9 * mm});
            skCircle(sketch, "E7.0.15.62", {"center": v(58.12, -743.92) * mm, "radius": 5.9 * mm});
            skCircle(sketch, "E7.0.15.63", {"center": v(58.12, -769.32) * mm, "radius": 5.9 * mm});
            skCircle(sketch, "E7.0.15.64", {"center": v(58.12, -794.72) * mm, "radius": 5.9 * mm});
            skCircle(sketch, "E7.0.16.25", {"center": v(83.52, 195.88) * mm, "radius": 5.9 * mm});
            skCircle(sketch, "E7.0.16.26", {"center": v(83.52, 170.48) * mm, "radius": 5.9 * mm});
            skCircle(sketch, "E7.0.16.27", {"center": v(83.52, 145.08) * mm, "radius": 5.9 * mm});
            skCircle(sketch, "E7.0.16.28", {"center": v(83.52, 119.68) * mm, "radius": 5.9 * mm});
            skCircle(sketch, "E7.0.16.29", {"center": v(83.52, 94.28) * mm, "radius": 5.9 * mm});
            skCircle(sketch, "E7.0.16.30", {"center": v(83.52, 68.88) * mm, "radius": 5.9 * mm});
            skCircle(sketch, "E7.0.16.31", {"center": v(83.52, 43.48) * mm, "radius": 5.9 * mm});
            skCircle(sketch, "E7.0.16.32", {"center": v(83.52, 18.08) * mm, "radius": 5.9 * mm});
            skCircle(sketch, "E7.0.16.33", {"center": v(83.52, -7.32) * mm, "radius": 5.9 * mm});
            skCircle(sketch, "E7.0.16.34", {"center": v(83.52, -32.72) * mm, "radius": 5.9 * mm});
            skCircle(sketch, "E7.0.16.35", {"center": v(83.52, -58.12) * mm, "radius": 5.9 * mm});
            skCircle(sketch, "E7.0.16.36", {"center": v(83.52, -83.52) * mm, "radius": 5.9 * mm});
            skCircle(sketch, "E7.0.16.37", {"center": v(83.52, -108.92) * mm, "radius": 5.9 * mm});
            skCircle(sketch, "E7.0.16.38", {"center": v(83.52, -134.32) * mm, "radius": 5.9 * mm});
            skCircle(sketch, "E7.0.16.39", {"center": v(83.52, -159.72) * mm, "radius": 5.9 * mm});
            skCircle(sketch, "E7.0.16.40", {"center": v(83.52, -185.12) * mm, "radius": 5.9 * mm});
            skCircle(sketch, "E7.0.16.41", {"center": v(83.52, -210.52) * mm, "radius": 5.9 * mm});
            skCircle(sketch, "E7.0.16.42", {"center": v(83.52, -235.92) * mm, "radius": 5.9 * mm});
            skCircle(sketch, "E7.0.16.43", {"center": v(83.52, -261.32) * mm, "radius": 5.9 * mm});
            skCircle(sketch, "E7.0.16.44", {"center": v(83.52, -286.72) * mm, "radius": 5.9 * mm});
            skCircle(sketch, "E7.0.16.45", {"center": v(83.52, -312.12) * mm, "radius": 5.9 * mm});
            skCircle(sketch, "E7.0.16.46", {"center": v(83.52, -337.52) * mm, "radius": 5.9 * mm});
            skCircle(sketch, "E7.0.16.47", {"center": v(83.52, -362.92) * mm, "radius": 5.9 * mm});
            skCircle(sketch, "E7.0.16.48", {"center": v(83.52, -388.32) * mm, "radius": 5.9 * mm});
            skCircle(sketch, "E7.0.16.49", {"center": v(83.52, -413.72) * mm, "radius": 5.9 * mm});
            skCircle(sketch, "E7.0.16.50", {"center": v(83.52, -439.12) * mm, "radius": 5.9 * mm});
            skCircle(sketch, "E7.0.16.51", {"center": v(83.52, -464.52) * mm, "radius": 5.9 * mm});
            skCircle(sketch, "E7.0.16.52", {"center": v(83.52, -489.92) * mm, "radius": 5.9 * mm});
            skCircle(sketch, "E7.0.16.53", {"center": v(83.52, -515.32) * mm, "radius": 5.9 * mm});
            skCircle(sketch, "E7.0.16.54", {"center": v(83.52, -540.72) * mm, "radius": 5.9 * mm});
            skCircle(sketch, "E7.0.16.55", {"center": v(83.52, -566.12) * mm, "radius": 5.9 * mm});
            skCircle(sketch, "E7.0.16.56", {"center": v(83.52, -591.52) * mm, "radius": 5.9 * mm});
            skCircle(sketch, "E7.0.16.57", {"center": v(83.52, -616.92) * mm, "radius": 5.9 * mm});
            skCircle(sketch, "E7.0.16.58", {"center": v(83.52, -642.32) * mm, "radius": 5.9 * mm});
            skCircle(sketch, "E7.0.16.59", {"center": v(83.52, -667.72) * mm, "radius": 5.9 * mm});
            skCircle(sketch, "E7.0.16.60", {"center": v(83.52, -693.12) * mm, "radius": 5.9 * mm});
            skCircle(sketch, "E7.0.16.61", {"center": v(83.52, -718.52) * mm, "radius": 5.9 * mm});
            skCircle(sketch, "E7.0.16.62", {"center": v(83.52, -743.92) * mm, "radius": 5.9 * mm});
            skCircle(sketch, "E7.0.16.63", {"center": v(83.52, -769.32) * mm, "radius": 5.9 * mm});
            skCircle(sketch, "E7.0.16.64", {"center": v(83.52, -794.72) * mm, "radius": 5.9 * mm});
            skCircle(sketch, "E7.0.17.25", {"center": v(108.92, 195.88) * mm, "radius": 5.9 * mm});
            skCircle(sketch, "E7.0.17.26", {"center": v(108.92, 170.48) * mm, "radius": 5.9 * mm});
            skCircle(sketch, "E7.0.17.27", {"center": v(108.92, 145.08) * mm, "radius": 5.9 * mm});
            skCircle(sketch, "E7.0.17.28", {"center": v(108.92, 119.68) * mm, "radius": 5.9 * mm});
            skCircle(sketch, "E7.0.17.29", {"center": v(108.92, 94.28) * mm, "radius": 5.9 * mm});
            skCircle(sketch, "E7.0.17.30", {"center": v(108.92, 68.88) * mm, "radius": 5.9 * mm});
            skCircle(sketch, "E7.0.17.31", {"center": v(108.92, 43.48) * mm, "radius": 5.9 * mm});
            skCircle(sketch, "E7.0.17.32", {"center": v(108.92, 18.08) * mm, "radius": 5.9 * mm});
            skCircle(sketch, "E7.0.17.33", {"center": v(108.92, -7.32) * mm, "radius": 5.9 * mm});
            skCircle(sketch, "E7.0.17.34", {"center": v(108.92, -32.72) * mm, "radius": 5.9 * mm});
            skCircle(sketch, "E7.0.17.35", {"center": v(108.92, -58.12) * mm, "radius": 5.9 * mm});
            skCircle(sketch, "E7.0.17.36", {"center": v(108.92, -83.52) * mm, "radius": 5.9 * mm});
            skCircle(sketch, "E7.0.17.37", {"center": v(108.92, -108.92) * mm, "radius": 5.9 * mm});
            skCircle(sketch, "E7.0.17.38", {"center": v(108.92, -134.32) * mm, "radius": 5.9 * mm});
            skCircle(sketch, "E7.0.17.39", {"center": v(108.92, -159.72) * mm, "radius": 5.9 * mm});
            skCircle(sketch, "E7.0.17.40", {"center": v(108.92, -185.12) * mm, "radius": 5.9 * mm});
            skCircle(sketch, "E7.0.17.41", {"center": v(108.92, -210.52) * mm, "radius": 5.9 * mm});
            skCircle(sketch, "E7.0.17.42", {"center": v(108.92, -235.92) * mm, "radius": 5.9 * mm});
            skCircle(sketch, "E7.0.17.43", {"center": v(108.92, -261.32) * mm, "radius": 5.9 * mm});
            skCircle(sketch, "E7.0.17.44", {"center": v(108.92, -286.72) * mm, "radius": 5.9 * mm});
            skCircle(sketch, "E7.0.17.45", {"center": v(108.92, -312.12) * mm, "radius": 5.9 * mm});
            skCircle(sketch, "E7.0.17.46", {"center": v(108.92, -337.52) * mm, "radius": 5.9 * mm});
            skCircle(sketch, "E7.0.17.47", {"center": v(108.92, -362.92) * mm, "radius": 5.9 * mm});
            skCircle(sketch, "E7.0.17.48", {"center": v(108.92, -388.32) * mm, "radius": 5.9 * mm});
            skCircle(sketch, "E7.0.17.49", {"center": v(108.92, -413.72) * mm, "radius": 5.9 * mm});
            skCircle(sketch, "E7.0.17.50", {"center": v(108.92, -439.12) * mm, "radius": 5.9 * mm});
            skCircle(sketch, "E7.0.17.51", {"center": v(108.92, -464.52) * mm, "radius": 5.9 * mm});
            skCircle(sketch, "E7.0.17.52", {"center": v(108.92, -489.92) * mm, "radius": 5.9 * mm});
            skCircle(sketch, "E7.0.17.53", {"center": v(108.92, -515.32) * mm, "radius": 5.9 * mm});
            skCircle(sketch, "E7.0.17.54", {"center": v(108.92, -540.72) * mm, "radius": 5.9 * mm});
            skCircle(sketch, "E7.0.17.55", {"center": v(108.92, -566.12) * mm, "radius": 5.9 * mm});
            skCircle(sketch, "E7.0.17.56", {"center": v(108.92, -591.52) * mm, "radius": 5.9 * mm});
            skCircle(sketch, "E7.0.17.57", {"center": v(108.92, -616.92) * mm, "radius": 5.9 * mm});
            skCircle(sketch, "E7.0.17.58", {"center": v(108.92, -642.32) * mm, "radius": 5.9 * mm});
            skCircle(sketch, "E7.0.17.59", {"center": v(108.92, -667.72) * mm, "radius": 5.9 * mm});
            skCircle(sketch, "E7.0.17.60", {"center": v(108.92, -693.12) * mm, "radius": 5.9 * mm});
            skCircle(sketch, "E7.0.17.61", {"center": v(108.92, -718.52) * mm, "radius": 5.9 * mm});
            skCircle(sketch, "E7.0.17.62", {"center": v(108.92, -743.92) * mm, "radius": 5.9 * mm});
            skCircle(sketch, "E7.0.17.63", {"center": v(108.92, -769.32) * mm, "radius": 5.9 * mm});
            skCircle(sketch, "E7.0.17.64", {"center": v(108.92, -794.72) * mm, "radius": 5.9 * mm});
            skCircle(sketch, "E7.0.18.25", {"center": v(134.32, 195.88) * mm, "radius": 5.9 * mm});
            skCircle(sketch, "E7.0.18.26", {"center": v(134.32, 170.48) * mm, "radius": 5.9 * mm});
            skCircle(sketch, "E7.0.18.27", {"center": v(134.32, 145.08) * mm, "radius": 5.9 * mm});
            skCircle(sketch, "E7.0.18.28", {"center": v(134.32, 119.68) * mm, "radius": 5.9 * mm});
            skCircle(sketch, "E7.0.18.29", {"center": v(134.32, 94.28) * mm, "radius": 5.9 * mm});
            skCircle(sketch, "E7.0.18.30", {"center": v(134.32, 68.88) * mm, "radius": 5.9 * mm});
            skCircle(sketch, "E7.0.18.31", {"center": v(134.32, 43.48) * mm, "radius": 5.9 * mm});
            skCircle(sketch, "E7.0.18.32", {"center": v(134.32, 18.08) * mm, "radius": 5.9 * mm});
            skCircle(sketch, "E7.0.18.33", {"center": v(134.32, -7.32) * mm, "radius": 5.9 * mm});
            skCircle(sketch, "E7.0.18.34", {"center": v(134.32, -32.72) * mm, "radius": 5.9 * mm});
            skCircle(sketch, "E7.0.18.35", {"center": v(134.32, -58.12) * mm, "radius": 5.9 * mm});
            skCircle(sketch, "E7.0.18.36", {"center": v(134.32, -83.52) * mm, "radius": 5.9 * mm});
            skCircle(sketch, "E7.0.18.37", {"center": v(134.32, -108.92) * mm, "radius": 5.9 * mm});
            skCircle(sketch, "E7.0.18.38", {"center": v(134.32, -134.32) * mm, "radius": 5.9 * mm});
            skCircle(sketch, "E7.0.18.39", {"center": v(134.32, -159.72) * mm, "radius": 5.9 * mm});
            skCircle(sketch, "E7.0.18.40", {"center": v(134.32, -185.12) * mm, "radius": 5.9 * mm});
            skCircle(sketch, "E7.0.18.41", {"center": v(134.32, -210.52) * mm, "radius": 5.9 * mm});
            skCircle(sketch, "E7.0.18.42", {"center": v(134.32, -235.92) * mm, "radius": 5.9 * mm});
            skCircle(sketch, "E7.0.18.43", {"center": v(134.32, -261.32) * mm, "radius": 5.9 * mm});
            skCircle(sketch, "E7.0.18.44", {"center": v(134.32, -286.72) * mm, "radius": 5.9 * mm});
            skCircle(sketch, "E7.0.18.45", {"center": v(134.32, -312.12) * mm, "radius": 5.9 * mm});
            skCircle(sketch, "E7.0.18.46", {"center": v(134.32, -337.52) * mm, "radius": 5.9 * mm});
            skCircle(sketch, "E7.0.18.47", {"center": v(134.32, -362.92) * mm, "radius": 5.9 * mm});
            skCircle(sketch, "E7.0.18.48", {"center": v(134.32, -388.32) * mm, "radius": 5.9 * mm});
            skCircle(sketch, "E7.0.18.49", {"center": v(134.32, -413.72) * mm, "radius": 5.9 * mm});
            skCircle(sketch, "E7.0.18.50", {"center": v(134.32, -439.12) * mm, "radius": 5.9 * mm});
            skCircle(sketch, "E7.0.18.51", {"center": v(134.32, -464.52) * mm, "radius": 5.9 * mm});
            skCircle(sketch, "E7.0.18.52", {"center": v(134.32, -489.92) * mm, "radius": 5.9 * mm});
            skCircle(sketch, "E7.0.18.53", {"center": v(134.32, -515.32) * mm, "radius": 5.9 * mm});
            skCircle(sketch, "E7.0.18.54", {"center": v(134.32, -540.72) * mm, "radius": 5.9 * mm});
            skCircle(sketch, "E7.0.18.55", {"center": v(134.32, -566.12) * mm, "radius": 5.9 * mm});
            skCircle(sketch, "E7.0.18.56", {"center": v(134.32, -591.52) * mm, "radius": 5.9 * mm});
            skCircle(sketch, "E7.0.18.57", {"center": v(134.32, -616.92) * mm, "radius": 5.9 * mm});
            skCircle(sketch, "E7.0.18.58", {"center": v(134.32, -642.32) * mm, "radius": 5.9 * mm});
            skCircle(sketch, "E7.0.18.59", {"center": v(134.32, -667.72) * mm, "radius": 5.9 * mm});
            skCircle(sketch, "E7.0.18.60", {"center": v(134.32, -693.12) * mm, "radius": 5.9 * mm});
            skCircle(sketch, "E7.0.18.61", {"center": v(134.32, -718.52) * mm, "radius": 5.9 * mm});
            skCircle(sketch, "E7.0.18.62", {"center": v(134.32, -743.92) * mm, "radius": 5.9 * mm});
            skCircle(sketch, "E7.0.18.63", {"center": v(134.32, -769.32) * mm, "radius": 5.9 * mm});
            skCircle(sketch, "E7.0.18.64", {"center": v(134.32, -794.72) * mm, "radius": 5.9 * mm});
            skCircle(sketch, "E7.0.19.25", {"center": v(159.72, 195.88) * mm, "radius": 5.9 * mm});
            skCircle(sketch, "E7.0.19.26", {"center": v(159.72, 170.48) * mm, "radius": 5.9 * mm});
            skCircle(sketch, "E7.0.19.27", {"center": v(159.72, 145.08) * mm, "radius": 5.9 * mm});
            skCircle(sketch, "E7.0.19.28", {"center": v(159.72, 119.68) * mm, "radius": 5.9 * mm});
            skCircle(sketch, "E7.0.19.29", {"center": v(159.72, 94.28) * mm, "radius": 5.9 * mm});
            skCircle(sketch, "E7.0.19.30", {"center": v(159.72, 68.88) * mm, "radius": 5.9 * mm});
            skCircle(sketch, "E7.0.19.31", {"center": v(159.72, 43.48) * mm, "radius": 5.9 * mm});
            skCircle(sketch, "E7.0.19.32", {"center": v(159.72, 18.08) * mm, "radius": 5.9 * mm});
            skCircle(sketch, "E7.0.19.33", {"center": v(159.72, -7.32) * mm, "radius": 5.9 * mm});
            skCircle(sketch, "E7.0.19.34", {"center": v(159.72, -32.72) * mm, "radius": 5.9 * mm});
            skCircle(sketch, "E7.0.19.35", {"center": v(159.72, -58.12) * mm, "radius": 5.9 * mm});
            skCircle(sketch, "E7.0.19.36", {"center": v(159.72, -83.52) * mm, "radius": 5.9 * mm});
            skCircle(sketch, "E7.0.19.37", {"center": v(159.72, -108.92) * mm, "radius": 5.9 * mm});
            skCircle(sketch, "E7.0.19.38", {"center": v(159.72, -134.32) * mm, "radius": 5.9 * mm});
            skCircle(sketch, "E7.0.19.39", {"center": v(159.72, -159.72) * mm, "radius": 5.9 * mm});
            skCircle(sketch, "E7.0.19.40", {"center": v(159.72, -185.12) * mm, "radius": 5.9 * mm});
            skCircle(sketch, "E7.0.19.41", {"center": v(159.72, -210.52) * mm, "radius": 5.9 * mm});
            skCircle(sketch, "E7.0.19.42", {"center": v(159.72, -235.92) * mm, "radius": 5.9 * mm});
            skCircle(sketch, "E7.0.19.43", {"center": v(159.72, -261.32) * mm, "radius": 5.9 * mm});
            skCircle(sketch, "E7.0.19.44", {"center": v(159.72, -286.72) * mm, "radius": 5.9 * mm});
            skCircle(sketch, "E7.0.19.45", {"center": v(159.72, -312.12) * mm, "radius": 5.9 * mm});
            skCircle(sketch, "E7.0.19.46", {"center": v(159.72, -337.52) * mm, "radius": 5.9 * mm});
            skCircle(sketch, "E7.0.19.47", {"center": v(159.72, -362.92) * mm, "radius": 5.9 * mm});
            skCircle(sketch, "E7.0.19.48", {"center": v(159.72, -388.32) * mm, "radius": 5.9 * mm});
            skCircle(sketch, "E7.0.19.49", {"center": v(159.72, -413.72) * mm, "radius": 5.9 * mm});
            skCircle(sketch, "E7.0.19.50", {"center": v(159.72, -439.12) * mm, "radius": 5.9 * mm});
            skCircle(sketch, "E7.0.19.51", {"center": v(159.72, -464.52) * mm, "radius": 5.9 * mm});
            skCircle(sketch, "E7.0.19.52", {"center": v(159.72, -489.92) * mm, "radius": 5.9 * mm});
            skCircle(sketch, "E7.0.19.53", {"center": v(159.72, -515.32) * mm, "radius": 5.9 * mm});
            skCircle(sketch, "E7.0.19.54", {"center": v(159.72, -540.72) * mm, "radius": 5.9 * mm});
            skCircle(sketch, "E7.0.19.55", {"center": v(159.72, -566.12) * mm, "radius": 5.9 * mm});
            skCircle(sketch, "E7.0.19.56", {"center": v(159.72, -591.52) * mm, "radius": 5.9 * mm});
            skCircle(sketch, "E7.0.19.57", {"center": v(159.72, -616.92) * mm, "radius": 5.9 * mm});
            skCircle(sketch, "E7.0.19.58", {"center": v(159.72, -642.32) * mm, "radius": 5.9 * mm});
            skCircle(sketch, "E7.0.19.59", {"center": v(159.72, -667.72) * mm, "radius": 5.9 * mm});
            skCircle(sketch, "E7.0.19.60", {"center": v(159.72, -693.12) * mm, "radius": 5.9 * mm});
            skCircle(sketch, "E7.0.19.61", {"center": v(159.72, -718.52) * mm, "radius": 5.9 * mm});
            skCircle(sketch, "E7.0.19.62", {"center": v(159.72, -743.92) * mm, "radius": 5.9 * mm});
            skCircle(sketch, "E7.0.19.63", {"center": v(159.72, -769.32) * mm, "radius": 5.9 * mm});
            skCircle(sketch, "E7.0.19.64", {"center": v(159.72, -794.72) * mm, "radius": 5.9 * mm});
            skCircle(sketch, "E7.0.20.25", {"center": v(185.12, 195.88) * mm, "radius": 5.9 * mm});
            skCircle(sketch, "E7.0.20.26", {"center": v(185.12, 170.48) * mm, "radius": 5.9 * mm});
            skCircle(sketch, "E7.0.20.27", {"center": v(185.12, 145.08) * mm, "radius": 5.9 * mm});
            skCircle(sketch, "E7.0.20.28", {"center": v(185.12, 119.68) * mm, "radius": 5.9 * mm});
            skCircle(sketch, "E7.0.20.29", {"center": v(185.12, 94.28) * mm, "radius": 5.9 * mm});
            skCircle(sketch, "E7.0.20.30", {"center": v(185.12, 68.88) * mm, "radius": 5.9 * mm});
            skCircle(sketch, "E7.0.20.31", {"center": v(185.12, 43.48) * mm, "radius": 5.9 * mm});
            skCircle(sketch, "E7.0.20.32", {"center": v(185.12, 18.08) * mm, "radius": 5.9 * mm});
            skCircle(sketch, "E7.0.20.33", {"center": v(185.12, -7.32) * mm, "radius": 5.9 * mm});
            skCircle(sketch, "E7.0.20.34", {"center": v(185.12, -32.72) * mm, "radius": 5.9 * mm});
            skCircle(sketch, "E7.0.20.35", {"center": v(185.12, -58.12) * mm, "radius": 5.9 * mm});
            skCircle(sketch, "E7.0.20.36", {"center": v(185.12, -83.52) * mm, "radius": 5.9 * mm});
            skCircle(sketch, "E7.0.20.37", {"center": v(185.12, -108.92) * mm, "radius": 5.9 * mm});
            skCircle(sketch, "E7.0.20.38", {"center": v(185.12, -134.32) * mm, "radius": 5.9 * mm});
            skCircle(sketch, "E7.0.20.39", {"center": v(185.12, -159.72) * mm, "radius": 5.9 * mm});
            skCircle(sketch, "E7.0.20.40", {"center": v(185.12, -185.12) * mm, "radius": 5.9 * mm});
            skCircle(sketch, "E7.0.20.41", {"center": v(185.12, -210.52) * mm, "radius": 5.9 * mm});
            skCircle(sketch, "E7.0.20.42", {"center": v(185.12, -235.92) * mm, "radius": 5.9 * mm});
            skCircle(sketch, "E7.0.20.43", {"center": v(185.12, -261.32) * mm, "radius": 5.9 * mm});
            skCircle(sketch, "E7.0.20.44", {"center": v(185.12, -286.72) * mm, "radius": 5.9 * mm});
            skCircle(sketch, "E7.0.20.45", {"center": v(185.12, -312.12) * mm, "radius": 5.9 * mm});
            skCircle(sketch, "E7.0.20.46", {"center": v(185.12, -337.52) * mm, "radius": 5.9 * mm});
            skCircle(sketch, "E7.0.20.47", {"center": v(185.12, -362.92) * mm, "radius": 5.9 * mm});
            skCircle(sketch, "E7.0.20.48", {"center": v(185.12, -388.32) * mm, "radius": 5.9 * mm});
            skCircle(sketch, "E7.0.20.49", {"center": v(185.12, -413.72) * mm, "radius": 5.9 * mm});
            skCircle(sketch, "E7.0.20.50", {"center": v(185.12, -439.12) * mm, "radius": 5.9 * mm});
            skCircle(sketch, "E7.0.20.51", {"center": v(185.12, -464.52) * mm, "radius": 5.9 * mm});
            skCircle(sketch, "E7.0.20.52", {"center": v(185.12, -489.92) * mm, "radius": 5.9 * mm});
            skCircle(sketch, "E7.0.20.53", {"center": v(185.12, -515.32) * mm, "radius": 5.9 * mm});
            skCircle(sketch, "E7.0.20.54", {"center": v(185.12, -540.72) * mm, "radius": 5.9 * mm});
            skCircle(sketch, "E7.0.20.55", {"center": v(185.12, -566.12) * mm, "radius": 5.9 * mm});
            skCircle(sketch, "E7.0.20.56", {"center": v(185.12, -591.52) * mm, "radius": 5.9 * mm});
            skCircle(sketch, "E7.0.20.57", {"center": v(185.12, -616.92) * mm, "radius": 5.9 * mm});
            skCircle(sketch, "E7.0.20.58", {"center": v(185.12, -642.32) * mm, "radius": 5.9 * mm});
            skCircle(sketch, "E7.0.20.59", {"center": v(185.12, -667.72) * mm, "radius": 5.9 * mm});
            skCircle(sketch, "E7.0.20.60", {"center": v(185.12, -693.12) * mm, "radius": 5.9 * mm});
            skCircle(sketch, "E7.0.20.61", {"center": v(185.12, -718.52) * mm, "radius": 5.9 * mm});
            skCircle(sketch, "E7.0.20.62", {"center": v(185.12, -743.92) * mm, "radius": 5.9 * mm});
            skCircle(sketch, "E7.0.20.63", {"center": v(185.12, -769.32) * mm, "radius": 5.9 * mm});
            skCircle(sketch, "E7.0.20.64", {"center": v(185.12, -794.72) * mm, "radius": 5.9 * mm});
            skCircle(sketch, "E7.0.21.25", {"center": v(210.52, 195.88) * mm, "radius": 5.9 * mm});
            skCircle(sketch, "E7.0.21.26", {"center": v(210.52, 170.48) * mm, "radius": 5.9 * mm});
            skCircle(sketch, "E7.0.21.27", {"center": v(210.52, 145.08) * mm, "radius": 5.9 * mm});
            skCircle(sketch, "E7.0.21.28", {"center": v(210.52, 119.68) * mm, "radius": 5.9 * mm});
            skCircle(sketch, "E7.0.21.29", {"center": v(210.52, 94.28) * mm, "radius": 5.9 * mm});
            skCircle(sketch, "E7.0.21.30", {"center": v(210.52, 68.88) * mm, "radius": 5.9 * mm});
            skCircle(sketch, "E7.0.21.31", {"center": v(210.52, 43.48) * mm, "radius": 5.9 * mm});
            skCircle(sketch, "E7.0.21.32", {"center": v(210.52, 18.08) * mm, "radius": 5.9 * mm});
            skCircle(sketch, "E7.0.21.33", {"center": v(210.52, -7.32) * mm, "radius": 5.9 * mm});
            skCircle(sketch, "E7.0.21.34", {"center": v(210.52, -32.72) * mm, "radius": 5.9 * mm});
            skCircle(sketch, "E7.0.21.35", {"center": v(210.52, -58.12) * mm, "radius": 5.9 * mm});
            skCircle(sketch, "E7.0.21.36", {"center": v(210.52, -83.52) * mm, "radius": 5.9 * mm});
            skCircle(sketch, "E7.0.21.37", {"center": v(210.52, -108.92) * mm, "radius": 5.9 * mm});
            skCircle(sketch, "E7.0.21.38", {"center": v(210.52, -134.32) * mm, "radius": 5.9 * mm});
            skCircle(sketch, "E7.0.21.39", {"center": v(210.52, -159.72) * mm, "radius": 5.9 * mm});
            skCircle(sketch, "E7.0.21.40", {"center": v(210.52, -185.12) * mm, "radius": 5.9 * mm});
            skCircle(sketch, "E7.0.21.41", {"center": v(210.52, -210.52) * mm, "radius": 5.9 * mm});
            skCircle(sketch, "E7.0.21.42", {"center": v(210.52, -235.92) * mm, "radius": 5.9 * mm});
            skCircle(sketch, "E7.0.21.43", {"center": v(210.52, -261.32) * mm, "radius": 5.9 * mm});
            skCircle(sketch, "E7.0.21.44", {"center": v(210.52, -286.72) * mm, "radius": 5.9 * mm});
            skCircle(sketch, "E7.0.21.45", {"center": v(210.52, -312.12) * mm, "radius": 5.9 * mm});
            skCircle(sketch, "E7.0.21.46", {"center": v(210.52, -337.52) * mm, "radius": 5.9 * mm});
            skCircle(sketch, "E7.0.21.47", {"center": v(210.52, -362.92) * mm, "radius": 5.9 * mm});
            skCircle(sketch, "E7.0.21.48", {"center": v(210.52, -388.32) * mm, "radius": 5.9 * mm});
            skCircle(sketch, "E7.0.21.49", {"center": v(210.52, -413.72) * mm, "radius": 5.9 * mm});
            skCircle(sketch, "E7.0.21.50", {"center": v(210.52, -439.12) * mm, "radius": 5.9 * mm});
            skCircle(sketch, "E7.0.21.51", {"center": v(210.52, -464.52) * mm, "radius": 5.9 * mm});
            skCircle(sketch, "E7.0.21.52", {"center": v(210.52, -489.92) * mm, "radius": 5.9 * mm});
            skCircle(sketch, "E7.0.21.53", {"center": v(210.52, -515.32) * mm, "radius": 5.9 * mm});
            skCircle(sketch, "E7.0.21.54", {"center": v(210.52, -540.72) * mm, "radius": 5.9 * mm});
            skCircle(sketch, "E7.0.21.55", {"center": v(210.52, -566.12) * mm, "radius": 5.9 * mm});
            skCircle(sketch, "E7.0.21.56", {"center": v(210.52, -591.52) * mm, "radius": 5.9 * mm});
            skCircle(sketch, "E7.0.21.57", {"center": v(210.52, -616.92) * mm, "radius": 5.9 * mm});
            skCircle(sketch, "E7.0.21.58", {"center": v(210.52, -642.32) * mm, "radius": 5.9 * mm});
            skCircle(sketch, "E7.0.21.59", {"center": v(210.52, -667.72) * mm, "radius": 5.9 * mm});
            skCircle(sketch, "E7.0.21.60", {"center": v(210.52, -693.12) * mm, "radius": 5.9 * mm});
            skCircle(sketch, "E7.0.21.61", {"center": v(210.52, -718.52) * mm, "radius": 5.9 * mm});
            skCircle(sketch, "E7.0.21.62", {"center": v(210.52, -743.92) * mm, "radius": 5.9 * mm});
            skCircle(sketch, "E7.0.21.63", {"center": v(210.52, -769.32) * mm, "radius": 5.9 * mm});
            skCircle(sketch, "E7.0.21.64", {"center": v(210.52, -794.72) * mm, "radius": 5.9 * mm});
            skCircle(sketch, "E7.0.22.25", {"center": v(235.92, 195.88) * mm, "radius": 5.9 * mm});
            skCircle(sketch, "E7.0.22.26", {"center": v(235.92, 170.48) * mm, "radius": 5.9 * mm});
            skCircle(sketch, "E7.0.22.27", {"center": v(235.92, 145.08) * mm, "radius": 5.9 * mm});
            skCircle(sketch, "E7.0.22.28", {"center": v(235.92, 119.68) * mm, "radius": 5.9 * mm});
            skCircle(sketch, "E7.0.22.29", {"center": v(235.92, 94.28) * mm, "radius": 5.9 * mm});
            skCircle(sketch, "E7.0.22.30", {"center": v(235.92, 68.88) * mm, "radius": 5.9 * mm});
            skCircle(sketch, "E7.0.22.31", {"center": v(235.92, 43.48) * mm, "radius": 5.9 * mm});
            skCircle(sketch, "E7.0.22.32", {"center": v(235.92, 18.08) * mm, "radius": 5.9 * mm});
            skCircle(sketch, "E7.0.22.33", {"center": v(235.92, -7.32) * mm, "radius": 5.9 * mm});
            skCircle(sketch, "E7.0.22.34", {"center": v(235.92, -32.72) * mm, "radius": 5.9 * mm});
            skCircle(sketch, "E7.0.22.35", {"center": v(235.92, -58.12) * mm, "radius": 5.9 * mm});
            skCircle(sketch, "E7.0.22.36", {"center": v(235.92, -83.52) * mm, "radius": 5.9 * mm});
            skCircle(sketch, "E7.0.22.37", {"center": v(235.92, -108.92) * mm, "radius": 5.9 * mm});
            skCircle(sketch, "E7.0.22.38", {"center": v(235.92, -134.32) * mm, "radius": 5.9 * mm});
            skCircle(sketch, "E7.0.22.39", {"center": v(235.92, -159.72) * mm, "radius": 5.9 * mm});
            skCircle(sketch, "E7.0.22.40", {"center": v(235.92, -185.12) * mm, "radius": 5.9 * mm});
            skCircle(sketch, "E7.0.22.41", {"center": v(235.92, -210.52) * mm, "radius": 5.9 * mm});
            skCircle(sketch, "E7.0.22.42", {"center": v(235.92, -235.92) * mm, "radius": 5.9 * mm});
            skCircle(sketch, "E7.0.22.43", {"center": v(235.92, -261.32) * mm, "radius": 5.9 * mm});
            skCircle(sketch, "E7.0.22.44", {"center": v(235.92, -286.72) * mm, "radius": 5.9 * mm});
            skCircle(sketch, "E7.0.22.45", {"center": v(235.92, -312.12) * mm, "radius": 5.9 * mm});
            skCircle(sketch, "E7.0.22.46", {"center": v(235.92, -337.52) * mm, "radius": 5.9 * mm});
            skCircle(sketch, "E7.0.22.47", {"center": v(235.92, -362.92) * mm, "radius": 5.9 * mm});
            skCircle(sketch, "E7.0.22.48", {"center": v(235.92, -388.32) * mm, "radius": 5.9 * mm});
            skCircle(sketch, "E7.0.22.49", {"center": v(235.92, -413.72) * mm, "radius": 5.9 * mm});
            skCircle(sketch, "E7.0.22.50", {"center": v(235.92, -439.12) * mm, "radius": 5.9 * mm});
            skCircle(sketch, "E7.0.22.51", {"center": v(235.92, -464.52) * mm, "radius": 5.9 * mm});
            skCircle(sketch, "E7.0.22.52", {"center": v(235.92, -489.92) * mm, "radius": 5.9 * mm});
            skCircle(sketch, "E7.0.22.53", {"center": v(235.92, -515.32) * mm, "radius": 5.9 * mm});
            skCircle(sketch, "E7.0.22.54", {"center": v(235.92, -540.72) * mm, "radius": 5.9 * mm});
            skCircle(sketch, "E7.0.22.55", {"center": v(235.92, -566.12) * mm, "radius": 5.9 * mm});
            skCircle(sketch, "E7.0.22.56", {"center": v(235.92, -591.52) * mm, "radius": 5.9 * mm});
            skCircle(sketch, "E7.0.22.57", {"center": v(235.92, -616.92) * mm, "radius": 5.9 * mm});
            skCircle(sketch, "E7.0.22.58", {"center": v(235.92, -642.32) * mm, "radius": 5.9 * mm});
            skCircle(sketch, "E7.0.22.59", {"center": v(235.92, -667.72) * mm, "radius": 5.9 * mm});
            skCircle(sketch, "E7.0.22.60", {"center": v(235.92, -693.12) * mm, "radius": 5.9 * mm});
            skCircle(sketch, "E7.0.22.61", {"center": v(235.92, -718.52) * mm, "radius": 5.9 * mm});
            skCircle(sketch, "E7.0.22.62", {"center": v(235.92, -743.92) * mm, "radius": 5.9 * mm});
            skCircle(sketch, "E7.0.22.63", {"center": v(235.92, -769.32) * mm, "radius": 5.9 * mm});
            skCircle(sketch, "E7.0.22.64", {"center": v(235.92, -794.72) * mm, "radius": 5.9 * mm});
            skCircle(sketch, "E7.0.23.25", {"center": v(261.32, 195.88) * mm, "radius": 5.9 * mm});
            skCircle(sketch, "E7.0.23.26", {"center": v(261.32, 170.48) * mm, "radius": 5.9 * mm});
            skCircle(sketch, "E7.0.23.27", {"center": v(261.32, 145.08) * mm, "radius": 5.9 * mm});
            skCircle(sketch, "E7.0.23.28", {"center": v(261.32, 119.68) * mm, "radius": 5.9 * mm});
            skCircle(sketch, "E7.0.23.29", {"center": v(261.32, 94.28) * mm, "radius": 5.9 * mm});
            skCircle(sketch, "E7.0.23.30", {"center": v(261.32, 68.88) * mm, "radius": 5.9 * mm});
            skCircle(sketch, "E7.0.23.31", {"center": v(261.32, 43.48) * mm, "radius": 5.9 * mm});
            skCircle(sketch, "E7.0.23.32", {"center": v(261.32, 18.08) * mm, "radius": 5.9 * mm});
            skCircle(sketch, "E7.0.23.33", {"center": v(261.32, -7.32) * mm, "radius": 5.9 * mm});
            skCircle(sketch, "E7.0.23.34", {"center": v(261.32, -32.72) * mm, "radius": 5.9 * mm});
            skCircle(sketch, "E7.0.23.35", {"center": v(261.32, -58.12) * mm, "radius": 5.9 * mm});
            skCircle(sketch, "E7.0.23.36", {"center": v(261.32, -83.52) * mm, "radius": 5.9 * mm});
            skCircle(sketch, "E7.0.23.37", {"center": v(261.32, -108.92) * mm, "radius": 5.9 * mm});
            skCircle(sketch, "E7.0.23.38", {"center": v(261.32, -134.32) * mm, "radius": 5.9 * mm});
            skCircle(sketch, "E7.0.23.39", {"center": v(261.32, -159.72) * mm, "radius": 5.9 * mm});
            skCircle(sketch, "E7.0.23.40", {"center": v(261.32, -185.12) * mm, "radius": 5.9 * mm});
            skCircle(sketch, "E7.0.23.41", {"center": v(261.32, -210.52) * mm, "radius": 5.9 * mm});
            skCircle(sketch, "E7.0.23.42", {"center": v(261.32, -235.92) * mm, "radius": 5.9 * mm});
            skCircle(sketch, "E7.0.23.43", {"center": v(261.32, -261.32) * mm, "radius": 5.9 * mm});
            skCircle(sketch, "E7.0.23.44", {"center": v(261.32, -286.72) * mm, "radius": 5.9 * mm});
            skCircle(sketch, "E7.0.23.45", {"center": v(261.32, -312.12) * mm, "radius": 5.9 * mm});
            skCircle(sketch, "E7.0.23.46", {"center": v(261.32, -337.52) * mm, "radius": 5.9 * mm});
            skCircle(sketch, "E7.0.23.47", {"center": v(261.32, -362.92) * mm, "radius": 5.9 * mm});
            skCircle(sketch, "E7.0.23.48", {"center": v(261.32, -388.32) * mm, "radius": 5.9 * mm});
            skCircle(sketch, "E7.0.23.49", {"center": v(261.32, -413.72) * mm, "radius": 5.9 * mm});
            skCircle(sketch, "E7.0.23.50", {"center": v(261.32, -439.12) * mm, "radius": 5.9 * mm});
            skCircle(sketch, "E7.0.23.51", {"center": v(261.32, -464.52) * mm, "radius": 5.9 * mm});
            skCircle(sketch, "E7.0.23.52", {"center": v(261.32, -489.92) * mm, "radius": 5.9 * mm});
            skCircle(sketch, "E7.0.23.53", {"center": v(261.32, -515.32) * mm, "radius": 5.9 * mm});
            skCircle(sketch, "E7.0.23.54", {"center": v(261.32, -540.72) * mm, "radius": 5.9 * mm});
            skCircle(sketch, "E7.0.23.55", {"center": v(261.32, -566.12) * mm, "radius": 5.9 * mm});
            skCircle(sketch, "E7.0.23.56", {"center": v(261.32, -591.52) * mm, "radius": 5.9 * mm});
            skCircle(sketch, "E7.0.23.57", {"center": v(261.32, -616.92) * mm, "radius": 5.9 * mm});
            skCircle(sketch, "E7.0.23.58", {"center": v(261.32, -642.32) * mm, "radius": 5.9 * mm});
            skCircle(sketch, "E7.0.23.59", {"center": v(261.32, -667.72) * mm, "radius": 5.9 * mm});
            skCircle(sketch, "E7.0.23.60", {"center": v(261.32, -693.12) * mm, "radius": 5.9 * mm});
            skCircle(sketch, "E7.0.23.61", {"center": v(261.32, -718.52) * mm, "radius": 5.9 * mm});
            skCircle(sketch, "E7.0.23.62", {"center": v(261.32, -743.92) * mm, "radius": 5.9 * mm});
            skCircle(sketch, "E7.0.23.63", {"center": v(261.32, -769.32) * mm, "radius": 5.9 * mm});
            skCircle(sketch, "E7.0.23.64", {"center": v(261.32, -794.72) * mm, "radius": 5.9 * mm});
            skCircle(sketch, "E7.0.24.25", {"center": v(286.72, 195.88) * mm, "radius": 5.9 * mm});
            skCircle(sketch, "E7.0.24.26", {"center": v(286.72, 170.48) * mm, "radius": 5.9 * mm});
            skCircle(sketch, "E7.0.24.27", {"center": v(286.72, 145.08) * mm, "radius": 5.9 * mm});
            skCircle(sketch, "E7.0.24.28", {"center": v(286.72, 119.68) * mm, "radius": 5.9 * mm});
            skCircle(sketch, "E7.0.24.29", {"center": v(286.72, 94.28) * mm, "radius": 5.9 * mm});
            skCircle(sketch, "E7.0.24.30", {"center": v(286.72, 68.88) * mm, "radius": 5.9 * mm});
            skCircle(sketch, "E7.0.24.31", {"center": v(286.72, 43.48) * mm, "radius": 5.9 * mm});
            skCircle(sketch, "E7.0.24.32", {"center": v(286.72, 18.08) * mm, "radius": 5.9 * mm});
            skCircle(sketch, "E7.0.24.33", {"center": v(286.72, -7.32) * mm, "radius": 5.9 * mm});
            skCircle(sketch, "E7.0.24.34", {"center": v(286.72, -32.72) * mm, "radius": 5.9 * mm});
            skCircle(sketch, "E7.0.24.35", {"center": v(286.72, -58.12) * mm, "radius": 5.9 * mm});
            skCircle(sketch, "E7.0.24.36", {"center": v(286.72, -83.52) * mm, "radius": 5.9 * mm});
            skCircle(sketch, "E7.0.24.37", {"center": v(286.72, -108.92) * mm, "radius": 5.9 * mm});
            skCircle(sketch, "E7.0.24.38", {"center": v(286.72, -134.32) * mm, "radius": 5.9 * mm});
            skCircle(sketch, "E7.0.24.39", {"center": v(286.72, -159.72) * mm, "radius": 5.9 * mm});
            skCircle(sketch, "E7.0.24.40", {"center": v(286.72, -185.12) * mm, "radius": 5.9 * mm});
            skCircle(sketch, "E7.0.24.41", {"center": v(286.72, -210.52) * mm, "radius": 5.9 * mm});
            skCircle(sketch, "E7.0.24.42", {"center": v(286.72, -235.92) * mm, "radius": 5.9 * mm});
            skCircle(sketch, "E7.0.24.43", {"center": v(286.72, -261.32) * mm, "radius": 5.9 * mm});
            skCircle(sketch, "E7.0.24.44", {"center": v(286.72, -286.72) * mm, "radius": 5.9 * mm});
            skCircle(sketch, "E7.0.24.45", {"center": v(286.72, -312.12) * mm, "radius": 5.9 * mm});
            skCircle(sketch, "E7.0.24.46", {"center": v(286.72, -337.52) * mm, "radius": 5.9 * mm});
            skCircle(sketch, "E7.0.24.47", {"center": v(286.72, -362.92) * mm, "radius": 5.9 * mm});
            skCircle(sketch, "E7.0.24.48", {"center": v(286.72, -388.32) * mm, "radius": 5.9 * mm});
            skCircle(sketch, "E7.0.24.49", {"center": v(286.72, -413.72) * mm, "radius": 5.9 * mm});
            skCircle(sketch, "E7.0.24.50", {"center": v(286.72, -439.12) * mm, "radius": 5.9 * mm});
            skCircle(sketch, "E7.0.24.51", {"center": v(286.72, -464.52) * mm, "radius": 5.9 * mm});
            skCircle(sketch, "E7.0.24.52", {"center": v(286.72, -489.92) * mm, "radius": 5.9 * mm});
            skCircle(sketch, "E7.0.24.53", {"center": v(286.72, -515.32) * mm, "radius": 5.9 * mm});
            skCircle(sketch, "E7.0.24.54", {"center": v(286.72, -540.72) * mm, "radius": 5.9 * mm});
            skCircle(sketch, "E7.0.24.55", {"center": v(286.72, -566.12) * mm, "radius": 5.9 * mm});
            skCircle(sketch, "E7.0.24.56", {"center": v(286.72, -591.52) * mm, "radius": 5.9 * mm});
            skCircle(sketch, "E7.0.24.57", {"center": v(286.72, -616.92) * mm, "radius": 5.9 * mm});
            skCircle(sketch, "E7.0.24.58", {"center": v(286.72, -642.32) * mm, "radius": 5.9 * mm});
            skCircle(sketch, "E7.0.24.59", {"center": v(286.72, -667.72) * mm, "radius": 5.9 * mm});
            skCircle(sketch, "E7.0.24.60", {"center": v(286.72, -693.12) * mm, "radius": 5.9 * mm});
            skCircle(sketch, "E7.0.24.61", {"center": v(286.72, -718.52) * mm, "radius": 5.9 * mm});
            skCircle(sketch, "E7.0.24.62", {"center": v(286.72, -743.92) * mm, "radius": 5.9 * mm});
            skCircle(sketch, "E7.0.24.63", {"center": v(286.72, -769.32) * mm, "radius": 5.9 * mm});
            skCircle(sketch, "E7.0.24.64", {"center": v(286.72, -794.72) * mm, "radius": 5.9 * mm});
            skCircle(sketch, "E7.0.25.25", {"center": v(312.12, 195.88) * mm, "radius": 5.9 * mm});
            skCircle(sketch, "E7.0.25.26", {"center": v(312.12, 170.48) * mm, "radius": 5.9 * mm});
            skCircle(sketch, "E7.0.25.27", {"center": v(312.12, 145.08) * mm, "radius": 5.9 * mm});
            skCircle(sketch, "E7.0.25.28", {"center": v(312.12, 119.68) * mm, "radius": 5.9 * mm});
            skCircle(sketch, "E7.0.25.29", {"center": v(312.12, 94.28) * mm, "radius": 5.9 * mm});
            skCircle(sketch, "E7.0.25.30", {"center": v(312.12, 68.88) * mm, "radius": 5.9 * mm});
            skCircle(sketch, "E7.0.25.31", {"center": v(312.12, 43.48) * mm, "radius": 5.9 * mm});
            skCircle(sketch, "E7.0.25.32", {"center": v(312.12, 18.08) * mm, "radius": 5.9 * mm});
            skCircle(sketch, "E7.0.25.33", {"center": v(312.12, -7.32) * mm, "radius": 5.9 * mm});
            skCircle(sketch, "E7.0.25.34", {"center": v(312.12, -32.72) * mm, "radius": 5.9 * mm});
            skCircle(sketch, "E7.0.25.35", {"center": v(312.12, -58.12) * mm, "radius": 5.9 * mm});
            skCircle(sketch, "E7.0.25.36", {"center": v(312.12, -83.52) * mm, "radius": 5.9 * mm});
            skCircle(sketch, "E7.0.25.37", {"center": v(312.12, -108.92) * mm, "radius": 5.9 * mm});
            skCircle(sketch, "E7.0.25.38", {"center": v(312.12, -134.32) * mm, "radius": 5.9 * mm});
            skCircle(sketch, "E7.0.25.39", {"center": v(312.12, -159.72) * mm, "radius": 5.9 * mm});
            skCircle(sketch, "E7.0.25.40", {"center": v(312.12, -185.12) * mm, "radius": 5.9 * mm});
            skCircle(sketch, "E7.0.25.41", {"center": v(312.12, -210.52) * mm, "radius": 5.9 * mm});
            skCircle(sketch, "E7.0.25.42", {"center": v(312.12, -235.92) * mm, "radius": 5.9 * mm});
            skCircle(sketch, "E7.0.25.43", {"center": v(312.12, -261.32) * mm, "radius": 5.9 * mm});
            skCircle(sketch, "E7.0.25.44", {"center": v(312.12, -286.72) * mm, "radius": 5.9 * mm});
            skCircle(sketch, "E7.0.25.45", {"center": v(312.12, -312.12) * mm, "radius": 5.9 * mm});
            skCircle(sketch, "E7.0.25.46", {"center": v(312.12, -337.52) * mm, "radius": 5.9 * mm});
            skCircle(sketch, "E7.0.25.47", {"center": v(312.12, -362.92) * mm, "radius": 5.9 * mm});
            skCircle(sketch, "E7.0.25.48", {"center": v(312.12, -388.32) * mm, "radius": 5.9 * mm});
            skCircle(sketch, "E7.0.25.49", {"center": v(312.12, -413.72) * mm, "radius": 5.9 * mm});
            skCircle(sketch, "E7.0.25.50", {"center": v(312.12, -439.12) * mm, "radius": 5.9 * mm});
            skCircle(sketch, "E7.0.25.51", {"center": v(312.12, -464.52) * mm, "radius": 5.9 * mm});
            skCircle(sketch, "E7.0.25.52", {"center": v(312.12, -489.92) * mm, "radius": 5.9 * mm});
            skCircle(sketch, "E7.0.25.53", {"center": v(312.12, -515.32) * mm, "radius": 5.9 * mm});
            skCircle(sketch, "E7.0.25.54", {"center": v(312.12, -540.72) * mm, "radius": 5.9 * mm});
            skCircle(sketch, "E7.0.25.55", {"center": v(312.12, -566.12) * mm, "radius": 5.9 * mm});
            skCircle(sketch, "E7.0.25.56", {"center": v(312.12, -591.52) * mm, "radius": 5.9 * mm});
            skCircle(sketch, "E7.0.25.57", {"center": v(312.12, -616.92) * mm, "radius": 5.9 * mm});
            skCircle(sketch, "E7.0.25.58", {"center": v(312.12, -642.32) * mm, "radius": 5.9 * mm});
            skCircle(sketch, "E7.0.25.59", {"center": v(312.12, -667.72) * mm, "radius": 5.9 * mm});
            skCircle(sketch, "E7.0.25.60", {"center": v(312.12, -693.12) * mm, "radius": 5.9 * mm});
            skCircle(sketch, "E7.0.25.61", {"center": v(312.12, -718.52) * mm, "radius": 5.9 * mm});
            skCircle(sketch, "E7.0.25.62", {"center": v(312.12, -743.92) * mm, "radius": 5.9 * mm});
            skCircle(sketch, "E7.0.25.63", {"center": v(312.12, -769.32) * mm, "radius": 5.9 * mm});
            skCircle(sketch, "E7.0.25.64", {"center": v(312.12, -794.72) * mm, "radius": 5.9 * mm});
            skCircle(sketch, "E8.0.0.65", {"center": v(-322.88, -820.12) * mm, "radius": 5.9 * mm});
            skCircle(sketch, "E8.0.1.65", {"center": v(-297.48, -820.12) * mm, "radius": 5.9 * mm});
            skCircle(sketch, "E8.0.2.65", {"center": v(-272.08, -820.12) * mm, "radius": 5.9 * mm});
            skCircle(sketch, "E8.0.3.65", {"center": v(-246.68, -820.12) * mm, "radius": 5.9 * mm});
            skCircle(sketch, "E8.0.4.65", {"center": v(-221.28, -820.12) * mm, "radius": 5.9 * mm});
            skCircle(sketch, "E8.0.5.65", {"center": v(-195.88, -820.12) * mm, "radius": 5.9 * mm});
            skCircle(sketch, "E8.0.6.65", {"center": v(-170.48, -820.12) * mm, "radius": 5.9 * mm});
            skCircle(sketch, "E8.0.7.65", {"center": v(-145.08, -820.12) * mm, "radius": 5.9 * mm});
            skCircle(sketch, "E8.0.8.65", {"center": v(-119.68, -820.12) * mm, "radius": 5.9 * mm});
            skCircle(sketch, "E8.0.9.65", {"center": v(-94.28, -820.12) * mm, "radius": 5.9 * mm});
            skCircle(sketch, "E8.0.10.65", {"center": v(-68.88, -820.12) * mm, "radius": 5.9 * mm});
            skCircle(sketch, "E8.0.11.65", {"center": v(-43.48, -820.12) * mm, "radius": 5.9 * mm});
            skCircle(sketch, "E8.0.12.65", {"center": v(-18.08, -820.12) * mm, "radius": 5.9 * mm});
            skCircle(sketch, "E8.0.13.65", {"center": v(7.32, -820.12) * mm, "radius": 5.9 * mm});
            skCircle(sketch, "E8.0.14.65", {"center": v(32.72, -820.12) * mm, "radius": 5.9 * mm});
            skCircle(sketch, "E8.0.15.65", {"center": v(58.12, -820.12) * mm, "radius": 5.9 * mm});
            skCircle(sketch, "E8.0.16.65", {"center": v(83.52, -820.12) * mm, "radius": 5.9 * mm});
            skCircle(sketch, "E8.0.17.65", {"center": v(108.92, -820.12) * mm, "radius": 5.9 * mm});
            skCircle(sketch, "E8.0.18.65", {"center": v(134.32, -820.12) * mm, "radius": 5.9 * mm});
            skCircle(sketch, "E8.0.19.65", {"center": v(159.72, -820.12) * mm, "radius": 5.9 * mm});
            skCircle(sketch, "E8.0.20.65", {"center": v(185.12, -820.12) * mm, "radius": 5.9 * mm});
            skCircle(sketch, "E8.0.21.65", {"center": v(210.52, -820.12) * mm, "radius": 5.9 * mm});
            skCircle(sketch, "E8.0.22.65", {"center": v(235.92, -820.12) * mm, "radius": 5.9 * mm});
            skCircle(sketch, "E8.0.23.65", {"center": v(261.32, -820.12) * mm, "radius": 5.9 * mm});
            skCircle(sketch, "E8.0.24.65", {"center": v(286.72, -820.12) * mm, "radius": 5.9 * mm});
            skCircle(sketch, "E8.0.25.65", {"center": v(312.12, -820.12) * mm, "radius": 5.9 * mm});
            skSolve(sketch);
        }
        {
            var Q0;
            Q0 = qSketchRegion(id + "F2", true);
            extrude(context, id + "F3", {"entities" : qUnion([Q0]), "operationType" : NewBodyOperationType.REMOVE, "oppositeDirection" : true, "depth" : 6.35 * mm, "offsetDistance" : 25.4 * mm});
        }
        {
            var Q0;
            Q0 = qSketchRegion(id + "F0", true);
            extrude(context, id + "F4", {"entities" : qUnion([Q0]), "endBound" : BoundingType.SYMMETRIC, "depth" : 44.45 * mm, "offsetDistance" : 25.4 * mm});
        }
    });
